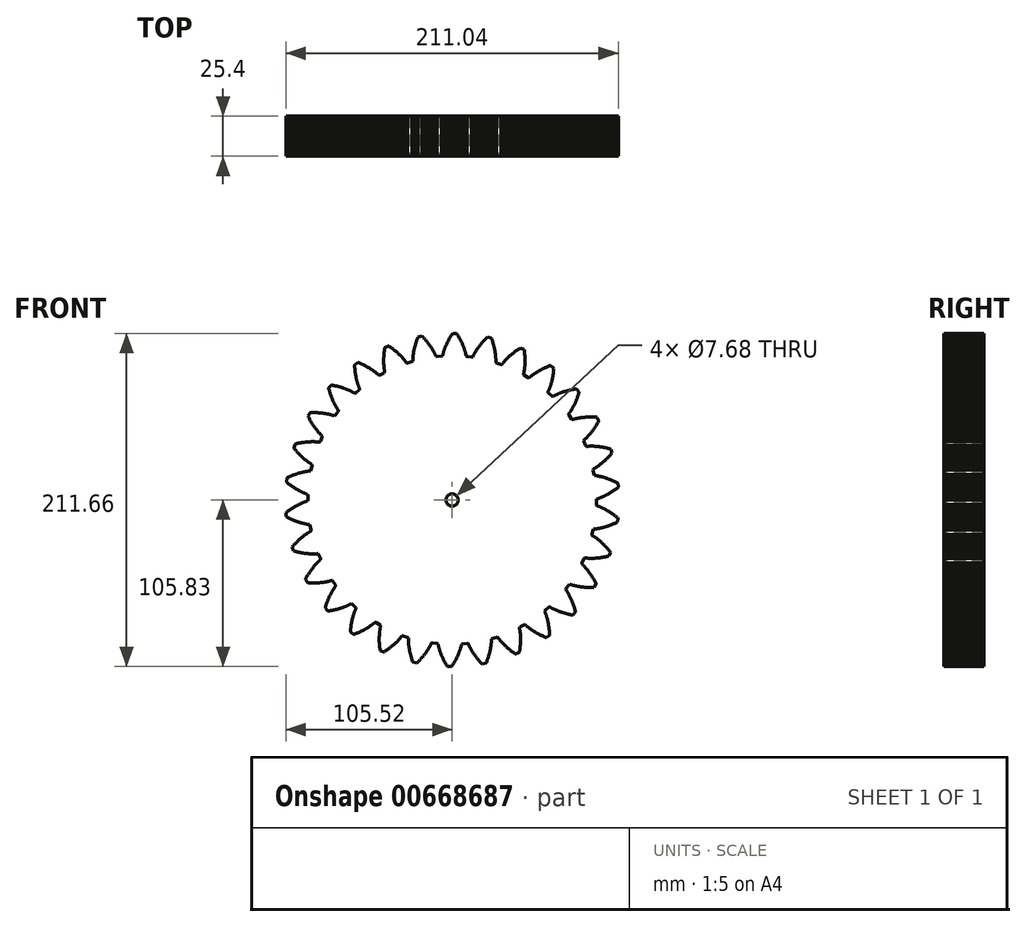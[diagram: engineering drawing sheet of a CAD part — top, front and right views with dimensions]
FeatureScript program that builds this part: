
annotation { "Feature Type Name" : "Feature", "Feature Type Description" : "" }
export const myFeature = defineFeature(function(context is Context, id is Id, definition is map)
    precondition{}
    {
        {
            var Q0;
            Q0=qCreatedBy(makeId("Front.planeOp"),FACE);
            var sketch = newSketch(context, id + "F0", { "sketchPlane" : qUnion([Q0])});
            skLineSegment(sketch, "E0", {"start": v(91.61, 0) * mm, "end": v(91.78, 0.64) * mm});
            skLineSegment(sketch, "E1", {"start": v(91.78, 0.64) * mm, "end": v(92.07, 0.72) * mm});
            skLineSegment(sketch, "E2", {"start": v(92.07, 0.72) * mm, "end": v(92.36, 0.8) * mm});
            skLineSegment(sketch, "E3", {"start": v(92.36, 0.8) * mm, "end": v(92.66, 0.9) * mm});
            skLineSegment(sketch, "E4", {"start": v(92.66, 0.9) * mm, "end": v(92.97, 1) * mm});
            skLineSegment(sketch, "E5", {"start": v(92.97, 1) * mm, "end": v(93.3, 1.12) * mm});
            skLineSegment(sketch, "E6", {"start": v(93.3, 1.12) * mm, "end": v(93.63, 1.24) * mm});
            skLineSegment(sketch, "E7", {"start": v(93.63, 1.24) * mm, "end": v(93.97, 1.37) * mm});
            skLineSegment(sketch, "E8", {"start": v(93.97, 1.37) * mm, "end": v(94.32, 1.5) * mm});
            skLineSegment(sketch, "E9", {"start": v(94.32, 1.5) * mm, "end": v(94.68, 1.64) * mm});
            skLineSegment(sketch, "E10", {"start": v(94.68, 1.64) * mm, "end": v(95.05, 1.8) * mm});
            skLineSegment(sketch, "E11", {"start": v(95.05, 1.8) * mm, "end": v(95.43, 1.96) * mm});
            skLineSegment(sketch, "E12", {"start": v(95.43, 1.96) * mm, "end": v(95.82, 2.13) * mm});
            skLineSegment(sketch, "E13", {"start": v(95.82, 2.13) * mm, "end": v(96.22, 2.3) * mm});
            skLineSegment(sketch, "E14", {"start": v(96.22, 2.3) * mm, "end": v(96.63, 2.5) * mm});
            skLineSegment(sketch, "E15", {"start": v(96.63, 2.5) * mm, "end": v(97.04, 2.7) * mm});
            skLineSegment(sketch, "E16", {"start": v(97.04, 2.7) * mm, "end": v(97.47, 2.9) * mm});
            skLineSegment(sketch, "E17", {"start": v(97.47, 2.9) * mm, "end": v(97.9, 3.13) * mm});
            skLineSegment(sketch, "E18", {"start": v(97.9, 3.13) * mm, "end": v(98.34, 3.36) * mm});
            skLineSegment(sketch, "E19", {"start": v(98.34, 3.36) * mm, "end": v(98.79, 3.6) * mm});
            skLineSegment(sketch, "E20", {"start": v(98.79, 3.6) * mm, "end": v(99.24, 3.85) * mm});
            skLineSegment(sketch, "E21", {"start": v(99.24, 3.85) * mm, "end": v(99.7, 4.11) * mm});
            skLineSegment(sketch, "E22", {"start": v(99.7, 4.11) * mm, "end": v(100.18, 4.4) * mm});
            skLineSegment(sketch, "E23", {"start": v(100.18, 4.4) * mm, "end": v(100.65, 4.68) * mm});
            skLineSegment(sketch, "E24", {"start": v(100.65, 4.68) * mm, "end": v(101.14, 4.97) * mm});
            skLineSegment(sketch, "E25", {"start": v(101.14, 4.97) * mm, "end": v(101.63, 5.29) * mm});
            skLineSegment(sketch, "E26", {"start": v(101.63, 5.29) * mm, "end": v(102.12, 5.6) * mm});
            skLineSegment(sketch, "E27", {"start": v(102.12, 5.6) * mm, "end": v(102.63, 5.94) * mm});
            skLineSegment(sketch, "E28", {"start": v(102.63, 5.94) * mm, "end": v(103.14, 6.3) * mm});
            skLineSegment(sketch, "E29", {"start": v(103.14, 6.3) * mm, "end": v(103.65, 6.65) * mm});
            skLineSegment(sketch, "E30", {"start": v(103.65, 6.65) * mm, "end": v(104.17, 7.03) * mm});
            skLineSegment(sketch, "E31", {"start": v(104.17, 7.03) * mm, "end": v(104.7, 7.41) * mm});
            skLineSegment(sketch, "E32", {"start": v(104.7, 7.41) * mm, "end": v(105.23, 7.81) * mm});
            skLineSegment(sketch, "E33", {"start": v(105.23, 7.81) * mm, "end": v(105.52, 8.2) * mm});
            skLineSegment(sketch, "E34", {"start": v(105.52, 8.2) * mm, "end": v(105.3, 10.56) * mm});
            skLineSegment(sketch, "E35", {"start": v(105.3, 10.56) * mm, "end": v(104.95, 10.9) * mm});
            skLineSegment(sketch, "E36", {"start": v(104.95, 10.9) * mm, "end": v(104.36, 11.2) * mm});
            skLineSegment(sketch, "E37", {"start": v(104.36, 11.2) * mm, "end": v(103.77, 11.48) * mm});
            skLineSegment(sketch, "E38", {"start": v(103.77, 11.48) * mm, "end": v(103.2, 11.76) * mm});
            skLineSegment(sketch, "E39", {"start": v(103.2, 11.76) * mm, "end": v(102.63, 12.02) * mm});
            skLineSegment(sketch, "E40", {"start": v(102.63, 12.02) * mm, "end": v(102.06, 12.28) * mm});
            skLineSegment(sketch, "E41", {"start": v(102.06, 12.28) * mm, "end": v(101.5, 12.52) * mm});
            skLineSegment(sketch, "E42", {"start": v(101.5, 12.52) * mm, "end": v(100.96, 12.75) * mm});
            skLineSegment(sketch, "E43", {"start": v(100.96, 12.75) * mm, "end": v(100.42, 12.97) * mm});
            skLineSegment(sketch, "E44", {"start": v(100.42, 12.97) * mm, "end": v(99.9, 13.17) * mm});
            skLineSegment(sketch, "E45", {"start": v(99.9, 13.17) * mm, "end": v(99.38, 13.37) * mm});
            skLineSegment(sketch, "E46", {"start": v(99.38, 13.37) * mm, "end": v(98.86, 13.56) * mm});
            skLineSegment(sketch, "E47", {"start": v(98.86, 13.56) * mm, "end": v(98.36, 13.74) * mm});
            skLineSegment(sketch, "E48", {"start": v(98.36, 13.74) * mm, "end": v(97.87, 13.9) * mm});
            skLineSegment(sketch, "E49", {"start": v(97.87, 13.9) * mm, "end": v(97.39, 14.06) * mm});
            skLineSegment(sketch, "E50", {"start": v(97.39, 14.06) * mm, "end": v(96.91, 14.21) * mm});
            skLineSegment(sketch, "E51", {"start": v(96.91, 14.21) * mm, "end": v(96.45, 14.35) * mm});
            skLineSegment(sketch, "E52", {"start": v(96.45, 14.35) * mm, "end": v(96, 14.49) * mm});
            skLineSegment(sketch, "E53", {"start": v(96, 14.49) * mm, "end": v(95.55, 14.6) * mm});
            skLineSegment(sketch, "E54", {"start": v(95.55, 14.6) * mm, "end": v(95.12, 14.72) * mm});
            skLineSegment(sketch, "E55", {"start": v(95.12, 14.72) * mm, "end": v(94.7, 14.83) * mm});
            skLineSegment(sketch, "E56", {"start": v(94.7, 14.83) * mm, "end": v(94.28, 14.93) * mm});
            skLineSegment(sketch, "E57", {"start": v(94.28, 14.93) * mm, "end": v(93.88, 15.02) * mm});
            skLineSegment(sketch, "E58", {"start": v(93.88, 15.02) * mm, "end": v(93.48, 15.1) * mm});
            skLineSegment(sketch, "E59", {"start": v(93.48, 15.1) * mm, "end": v(93.1, 15.18) * mm});
            skLineSegment(sketch, "E60", {"start": v(93.1, 15.18) * mm, "end": v(92.73, 15.25) * mm});
            skLineSegment(sketch, "E61", {"start": v(92.73, 15.25) * mm, "end": v(92.37, 15.32) * mm});
            skLineSegment(sketch, "E62", {"start": v(92.37, 15.32) * mm, "end": v(92.03, 15.38) * mm});
            skLineSegment(sketch, "E63", {"start": v(92.03, 15.38) * mm, "end": v(91.69, 15.43) * mm});
            skLineSegment(sketch, "E64", {"start": v(91.69, 15.43) * mm, "end": v(91.36, 15.48) * mm});
            skLineSegment(sketch, "E65", {"start": v(91.36, 15.48) * mm, "end": v(91.05, 15.52) * mm});
            skLineSegment(sketch, "E66", {"start": v(91.05, 15.52) * mm, "end": v(90.75, 15.55) * mm});
            skLineSegment(sketch, "E67", {"start": v(90.75, 15.55) * mm, "end": v(90.45, 15.58) * mm});
            skLineSegment(sketch, "E68", {"start": v(90.45, 15.58) * mm, "end": v(90.17, 16.18) * mm});
            skLineSegment(sketch, "E69", {"start": v(90.17, 16.18) * mm, "end": v(89.6, 19.05) * mm});
            skLineSegment(sketch, "E70", {"start": v(89.6, 19.05) * mm, "end": v(89.65, 19.7) * mm});
            skLineSegment(sketch, "E71", {"start": v(89.65, 19.7) * mm, "end": v(89.9, 19.85) * mm});
            skLineSegment(sketch, "E72", {"start": v(89.9, 19.85) * mm, "end": v(90.17, 20) * mm});
            skLineSegment(sketch, "E73", {"start": v(90.17, 20) * mm, "end": v(90.45, 20.15) * mm});
            skLineSegment(sketch, "E74", {"start": v(90.45, 20.15) * mm, "end": v(90.73, 20.32) * mm});
            skLineSegment(sketch, "E75", {"start": v(90.73, 20.32) * mm, "end": v(91.02, 20.5) * mm});
            skLineSegment(sketch, "E76", {"start": v(91.02, 20.5) * mm, "end": v(91.32, 20.68) * mm});
            skLineSegment(sketch, "E77", {"start": v(91.32, 20.68) * mm, "end": v(91.63, 20.87) * mm});
            skLineSegment(sketch, "E78", {"start": v(91.63, 20.87) * mm, "end": v(91.95, 21.08) * mm});
            skLineSegment(sketch, "E79", {"start": v(91.95, 21.08) * mm, "end": v(92.27, 21.3) * mm});
            skLineSegment(sketch, "E80", {"start": v(92.27, 21.3) * mm, "end": v(92.6, 21.52) * mm});
            skLineSegment(sketch, "E81", {"start": v(92.6, 21.52) * mm, "end": v(92.94, 21.76) * mm});
            skLineSegment(sketch, "E82", {"start": v(92.94, 21.76) * mm, "end": v(93.29, 22) * mm});
            skLineSegment(sketch, "E83", {"start": v(93.29, 22) * mm, "end": v(93.64, 22.26) * mm});
            skLineSegment(sketch, "E84", {"start": v(93.64, 22.26) * mm, "end": v(94, 22.53) * mm});
            skLineSegment(sketch, "E85", {"start": v(94, 22.53) * mm, "end": v(94.36, 22.81) * mm});
            skLineSegment(sketch, "E86", {"start": v(94.36, 22.81) * mm, "end": v(94.73, 23.1) * mm});
            skLineSegment(sketch, "E87", {"start": v(94.73, 23.1) * mm, "end": v(95.1, 23.41) * mm});
            skLineSegment(sketch, "E88", {"start": v(95.1, 23.41) * mm, "end": v(95.5, 23.73) * mm});
            skLineSegment(sketch, "E89", {"start": v(95.5, 23.73) * mm, "end": v(95.88, 24.06) * mm});
            skLineSegment(sketch, "E90", {"start": v(95.88, 24.06) * mm, "end": v(96.27, 24.4) * mm});
            skLineSegment(sketch, "E91", {"start": v(96.27, 24.4) * mm, "end": v(96.67, 24.76) * mm});
            skLineSegment(sketch, "E92", {"start": v(96.67, 24.76) * mm, "end": v(97.07, 25.12) * mm});
            skLineSegment(sketch, "E93", {"start": v(97.07, 25.12) * mm, "end": v(97.48, 25.5) * mm});
            skLineSegment(sketch, "E94", {"start": v(97.48, 25.5) * mm, "end": v(97.9, 25.9) * mm});
            skLineSegment(sketch, "E95", {"start": v(97.9, 25.9) * mm, "end": v(98.3, 26.3) * mm});
            skLineSegment(sketch, "E96", {"start": v(98.3, 26.3) * mm, "end": v(98.73, 26.72) * mm});
            skLineSegment(sketch, "E97", {"start": v(98.73, 26.72) * mm, "end": v(99.15, 27.15) * mm});
            skLineSegment(sketch, "E98", {"start": v(99.15, 27.15) * mm, "end": v(99.57, 27.6) * mm});
            skLineSegment(sketch, "E99", {"start": v(99.57, 27.6) * mm, "end": v(100, 28.06) * mm});
            skLineSegment(sketch, "E100", {"start": v(100, 28.06) * mm, "end": v(100.43, 28.53) * mm});
            skLineSegment(sketch, "E101", {"start": v(100.43, 28.53) * mm, "end": v(100.87, 29.02) * mm});
            skLineSegment(sketch, "E102", {"start": v(100.87, 29.02) * mm, "end": v(101.3, 29.52) * mm});
            skLineSegment(sketch, "E103", {"start": v(101.3, 29.52) * mm, "end": v(101.5, 29.96) * mm});
            skLineSegment(sketch, "E104", {"start": v(101.5, 29.96) * mm, "end": v(100.8, 32.22) * mm});
            skLineSegment(sketch, "E105", {"start": v(100.8, 32.22) * mm, "end": v(100.4, 32.48) * mm});
            skLineSegment(sketch, "E106", {"start": v(100.4, 32.48) * mm, "end": v(99.75, 32.65) * mm});
            skLineSegment(sketch, "E107", {"start": v(99.75, 32.65) * mm, "end": v(99.12, 32.8) * mm});
            skLineSegment(sketch, "E108", {"start": v(99.12, 32.8) * mm, "end": v(98.5, 32.96) * mm});
            skLineSegment(sketch, "E109", {"start": v(98.5, 32.96) * mm, "end": v(97.88, 33.1) * mm});
            skLineSegment(sketch, "E110", {"start": v(97.88, 33.1) * mm, "end": v(97.28, 33.23) * mm});
            skLineSegment(sketch, "E111", {"start": v(97.28, 33.23) * mm, "end": v(96.69, 33.35) * mm});
            skLineSegment(sketch, "E112", {"start": v(96.69, 33.35) * mm, "end": v(96.1, 33.46) * mm});
            skLineSegment(sketch, "E113", {"start": v(96.1, 33.46) * mm, "end": v(95.53, 33.56) * mm});
            skLineSegment(sketch, "E114", {"start": v(95.53, 33.56) * mm, "end": v(94.97, 33.66) * mm});
            skLineSegment(sketch, "E115", {"start": v(94.97, 33.66) * mm, "end": v(94.42, 33.74) * mm});
            skLineSegment(sketch, "E116", {"start": v(94.42, 33.74) * mm, "end": v(93.88, 33.82) * mm});
            skLineSegment(sketch, "E117", {"start": v(93.88, 33.82) * mm, "end": v(93.36, 33.89) * mm});
            skLineSegment(sketch, "E118", {"start": v(93.36, 33.89) * mm, "end": v(92.84, 33.95) * mm});
            skLineSegment(sketch, "E119", {"start": v(92.84, 33.95) * mm, "end": v(92.33, 34) * mm});
            skLineSegment(sketch, "E120", {"start": v(92.33, 34) * mm, "end": v(91.84, 34.05) * mm});
            skLineSegment(sketch, "E121", {"start": v(91.84, 34.05) * mm, "end": v(91.36, 34.1) * mm});
            skLineSegment(sketch, "E122", {"start": v(91.36, 34.1) * mm, "end": v(90.88, 34.13) * mm});
            skLineSegment(sketch, "E123", {"start": v(90.88, 34.13) * mm, "end": v(90.43, 34.15) * mm});
            skLineSegment(sketch, "E124", {"start": v(90.43, 34.15) * mm, "end": v(89.98, 34.18) * mm});
            skLineSegment(sketch, "E125", {"start": v(89.98, 34.18) * mm, "end": v(89.54, 34.2) * mm});
            skLineSegment(sketch, "E126", {"start": v(89.54, 34.2) * mm, "end": v(89.11, 34.2) * mm});
            skLineSegment(sketch, "E127", {"start": v(89.11, 34.2) * mm, "end": v(88.7, 34.21) * mm});
            skLineSegment(sketch, "E128", {"start": v(88.7, 34.21) * mm, "end": v(88.3, 34.21) * mm});
            skLineSegment(sketch, "E129", {"start": v(88.3, 34.21) * mm, "end": v(87.91, 34.2) * mm});
            skLineSegment(sketch, "E130", {"start": v(87.91, 34.2) * mm, "end": v(87.54, 34.2) * mm});
            skLineSegment(sketch, "E131", {"start": v(87.54, 34.2) * mm, "end": v(87.17, 34.19) * mm});
            skLineSegment(sketch, "E132", {"start": v(87.17, 34.19) * mm, "end": v(86.82, 34.17) * mm});
            skLineSegment(sketch, "E133", {"start": v(86.82, 34.17) * mm, "end": v(86.48, 34.15) * mm});
            skLineSegment(sketch, "E134", {"start": v(86.48, 34.15) * mm, "end": v(86.15, 34.13) * mm});
            skLineSegment(sketch, "E135", {"start": v(86.15, 34.13) * mm, "end": v(85.83, 34.1) * mm});
            skLineSegment(sketch, "E136", {"start": v(85.83, 34.1) * mm, "end": v(85.53, 34.08) * mm});
            skLineSegment(sketch, "E137", {"start": v(85.53, 34.08) * mm, "end": v(85.24, 34.05) * mm});
            skLineSegment(sketch, "E138", {"start": v(85.24, 34.05) * mm, "end": v(84.84, 34.58) * mm});
            skLineSegment(sketch, "E139", {"start": v(84.84, 34.58) * mm, "end": v(83.7, 37.26) * mm});
            skLineSegment(sketch, "E140", {"start": v(83.7, 37.26) * mm, "end": v(83.6, 37.91) * mm});
            skLineSegment(sketch, "E141", {"start": v(83.6, 37.91) * mm, "end": v(83.81, 38.1) * mm});
            skLineSegment(sketch, "E142", {"start": v(83.81, 38.1) * mm, "end": v(84.04, 38.3) * mm});
            skLineSegment(sketch, "E143", {"start": v(84.04, 38.3) * mm, "end": v(84.28, 38.51) * mm});
            skLineSegment(sketch, "E144", {"start": v(84.28, 38.51) * mm, "end": v(84.52, 38.74) * mm});
            skLineSegment(sketch, "E145", {"start": v(84.52, 38.74) * mm, "end": v(84.77, 38.97) * mm});
            skLineSegment(sketch, "E146", {"start": v(84.77, 38.97) * mm, "end": v(85.03, 39.21) * mm});
            skLineSegment(sketch, "E147", {"start": v(85.03, 39.21) * mm, "end": v(85.3, 39.47) * mm});
            skLineSegment(sketch, "E148", {"start": v(85.3, 39.47) * mm, "end": v(85.56, 39.73) * mm});
            skLineSegment(sketch, "E149", {"start": v(85.56, 39.73) * mm, "end": v(85.83, 40.01) * mm});
            skLineSegment(sketch, "E150", {"start": v(85.83, 40.01) * mm, "end": v(86.1, 40.3) * mm});
            skLineSegment(sketch, "E151", {"start": v(86.1, 40.3) * mm, "end": v(86.39, 40.6) * mm});
            skLineSegment(sketch, "E152", {"start": v(86.39, 40.6) * mm, "end": v(86.67, 40.92) * mm});
            skLineSegment(sketch, "E153", {"start": v(86.67, 40.92) * mm, "end": v(86.96, 41.24) * mm});
            skLineSegment(sketch, "E154", {"start": v(86.96, 41.24) * mm, "end": v(87.26, 41.58) * mm});
            skLineSegment(sketch, "E155", {"start": v(87.26, 41.58) * mm, "end": v(87.56, 41.93) * mm});
            skLineSegment(sketch, "E156", {"start": v(87.56, 41.93) * mm, "end": v(87.86, 42.3) * mm});
            skLineSegment(sketch, "E157", {"start": v(87.86, 42.3) * mm, "end": v(88.16, 42.68) * mm});
            skLineSegment(sketch, "E158", {"start": v(88.16, 42.68) * mm, "end": v(88.47, 43.07) * mm});
            skLineSegment(sketch, "E159", {"start": v(88.47, 43.07) * mm, "end": v(88.78, 43.47) * mm});
            skLineSegment(sketch, "E160", {"start": v(88.78, 43.47) * mm, "end": v(89.1, 43.88) * mm});
            skLineSegment(sketch, "E161", {"start": v(89.1, 43.88) * mm, "end": v(89.41, 44.31) * mm});
            skLineSegment(sketch, "E162", {"start": v(89.41, 44.31) * mm, "end": v(89.73, 44.76) * mm});
            skLineSegment(sketch, "E163", {"start": v(89.73, 44.76) * mm, "end": v(90.05, 45.21) * mm});
            skLineSegment(sketch, "E164", {"start": v(90.05, 45.21) * mm, "end": v(90.37, 45.68) * mm});
            skLineSegment(sketch, "E165", {"start": v(90.37, 45.68) * mm, "end": v(90.69, 46.16) * mm});
            skLineSegment(sketch, "E166", {"start": v(90.69, 46.16) * mm, "end": v(91.01, 46.66) * mm});
            skLineSegment(sketch, "E167", {"start": v(91.01, 46.66) * mm, "end": v(91.34, 47.17) * mm});
            skLineSegment(sketch, "E168", {"start": v(91.34, 47.17) * mm, "end": v(91.66, 47.7) * mm});
            skLineSegment(sketch, "E169", {"start": v(91.66, 47.7) * mm, "end": v(91.98, 48.24) * mm});
            skLineSegment(sketch, "E170", {"start": v(91.98, 48.24) * mm, "end": v(92.3, 48.79) * mm});
            skLineSegment(sketch, "E171", {"start": v(92.3, 48.79) * mm, "end": v(92.63, 49.35) * mm});
            skLineSegment(sketch, "E172", {"start": v(92.63, 49.35) * mm, "end": v(92.95, 49.93) * mm});
            skLineSegment(sketch, "E173", {"start": v(92.95, 49.93) * mm, "end": v(93.05, 50.41) * mm});
            skLineSegment(sketch, "E174", {"start": v(93.05, 50.41) * mm, "end": v(91.9, 52.48) * mm});
            skLineSegment(sketch, "E175", {"start": v(91.9, 52.48) * mm, "end": v(91.45, 52.64) * mm});
            skLineSegment(sketch, "E176", {"start": v(91.45, 52.64) * mm, "end": v(90.78, 52.68) * mm});
            skLineSegment(sketch, "E177", {"start": v(90.78, 52.68) * mm, "end": v(90.13, 52.7) * mm});
            skLineSegment(sketch, "E178", {"start": v(90.13, 52.7) * mm, "end": v(89.49, 52.72) * mm});
            skLineSegment(sketch, "E179", {"start": v(89.49, 52.72) * mm, "end": v(88.86, 52.73) * mm});
            skLineSegment(sketch, "E180", {"start": v(88.86, 52.73) * mm, "end": v(88.25, 52.73) * mm});
            skLineSegment(sketch, "E181", {"start": v(88.25, 52.73) * mm, "end": v(87.64, 52.72) * mm});
            skLineSegment(sketch, "E182", {"start": v(87.64, 52.72) * mm, "end": v(87.05, 52.7) * mm});
            skLineSegment(sketch, "E183", {"start": v(87.05, 52.7) * mm, "end": v(86.47, 52.7) * mm});
            skLineSegment(sketch, "E184", {"start": v(86.47, 52.7) * mm, "end": v(85.9, 52.67) * mm});
            skLineSegment(sketch, "E185", {"start": v(85.9, 52.67) * mm, "end": v(85.34, 52.64) * mm});
            skLineSegment(sketch, "E186", {"start": v(85.34, 52.64) * mm, "end": v(84.8, 52.6) * mm});
            skLineSegment(sketch, "E187", {"start": v(84.8, 52.6) * mm, "end": v(84.27, 52.56) * mm});
            skLineSegment(sketch, "E188", {"start": v(84.27, 52.56) * mm, "end": v(83.75, 52.51) * mm});
            skLineSegment(sketch, "E189", {"start": v(83.75, 52.51) * mm, "end": v(83.25, 52.46) * mm});
            skLineSegment(sketch, "E190", {"start": v(83.25, 52.46) * mm, "end": v(82.75, 52.4) * mm});
            skLineSegment(sketch, "E191", {"start": v(82.75, 52.4) * mm, "end": v(82.27, 52.34) * mm});
            skLineSegment(sketch, "E192", {"start": v(82.27, 52.34) * mm, "end": v(81.8, 52.28) * mm});
            skLineSegment(sketch, "E193", {"start": v(81.8, 52.28) * mm, "end": v(81.35, 52.2) * mm});
            skLineSegment(sketch, "E194", {"start": v(81.35, 52.2) * mm, "end": v(80.9, 52.14) * mm});
            skLineSegment(sketch, "E195", {"start": v(80.9, 52.14) * mm, "end": v(80.47, 52.06) * mm});
            skLineSegment(sketch, "E196", {"start": v(80.47, 52.06) * mm, "end": v(80.06, 51.98) * mm});
            skLineSegment(sketch, "E197", {"start": v(80.06, 51.98) * mm, "end": v(79.65, 51.9) * mm});
            skLineSegment(sketch, "E198", {"start": v(79.65, 51.9) * mm, "end": v(79.26, 51.82) * mm});
            skLineSegment(sketch, "E199", {"start": v(79.26, 51.82) * mm, "end": v(78.88, 51.74) * mm});
            skLineSegment(sketch, "E200", {"start": v(78.88, 51.74) * mm, "end": v(78.51, 51.65) * mm});
            skLineSegment(sketch, "E201", {"start": v(78.51, 51.65) * mm, "end": v(78.16, 51.57) * mm});
            skLineSegment(sketch, "E202", {"start": v(78.16, 51.57) * mm, "end": v(77.82, 51.48) * mm});
            skLineSegment(sketch, "E203", {"start": v(77.82, 51.48) * mm, "end": v(77.49, 51.39) * mm});
            skLineSegment(sketch, "E204", {"start": v(77.49, 51.39) * mm, "end": v(77.17, 51.3) * mm});
            skLineSegment(sketch, "E205", {"start": v(77.17, 51.3) * mm, "end": v(76.87, 51.2) * mm});
            skLineSegment(sketch, "E206", {"start": v(76.87, 51.2) * mm, "end": v(76.57, 51.12) * mm});
            skLineSegment(sketch, "E207", {"start": v(76.57, 51.12) * mm, "end": v(76.3, 51.03) * mm});
            skLineSegment(sketch, "E208", {"start": v(76.3, 51.03) * mm, "end": v(75.8, 51.46) * mm});
            skLineSegment(sketch, "E209", {"start": v(75.8, 51.46) * mm, "end": v(74.11, 53.85) * mm});
            skLineSegment(sketch, "E210", {"start": v(74.11, 53.85) * mm, "end": v(73.88, 54.46) * mm});
            skLineSegment(sketch, "E211", {"start": v(73.88, 54.46) * mm, "end": v(74.06, 54.7) * mm});
            skLineSegment(sketch, "E212", {"start": v(74.06, 54.7) * mm, "end": v(74.24, 54.94) * mm});
            skLineSegment(sketch, "E213", {"start": v(74.24, 54.94) * mm, "end": v(74.43, 55.2) * mm});
            skLineSegment(sketch, "E214", {"start": v(74.43, 55.2) * mm, "end": v(74.62, 55.46) * mm});
            skLineSegment(sketch, "E215", {"start": v(74.62, 55.46) * mm, "end": v(74.82, 55.74) * mm});
            skLineSegment(sketch, "E216", {"start": v(74.82, 55.74) * mm, "end": v(75.02, 56.04) * mm});
            skLineSegment(sketch, "E217", {"start": v(75.02, 56.04) * mm, "end": v(75.22, 56.34) * mm});
            skLineSegment(sketch, "E218", {"start": v(75.22, 56.34) * mm, "end": v(75.43, 56.65) * mm});
            skLineSegment(sketch, "E219", {"start": v(75.43, 56.65) * mm, "end": v(75.63, 56.98) * mm});
            skLineSegment(sketch, "E220", {"start": v(75.63, 56.98) * mm, "end": v(75.84, 57.33) * mm});
            skLineSegment(sketch, "E221", {"start": v(75.84, 57.33) * mm, "end": v(76.06, 57.68) * mm});
            skLineSegment(sketch, "E222", {"start": v(76.06, 57.68) * mm, "end": v(76.27, 58.05) * mm});
            skLineSegment(sketch, "E223", {"start": v(76.27, 58.05) * mm, "end": v(76.49, 58.42) * mm});
            skLineSegment(sketch, "E224", {"start": v(76.49, 58.42) * mm, "end": v(76.7, 58.82) * mm});
            skLineSegment(sketch, "E225", {"start": v(76.7, 58.82) * mm, "end": v(76.92, 59.22) * mm});
            skLineSegment(sketch, "E226", {"start": v(76.92, 59.22) * mm, "end": v(77.14, 59.64) * mm});
            skLineSegment(sketch, "E227", {"start": v(77.14, 59.64) * mm, "end": v(77.36, 60.07) * mm});
            skLineSegment(sketch, "E228", {"start": v(77.36, 60.07) * mm, "end": v(77.58, 60.52) * mm});
            skLineSegment(sketch, "E229", {"start": v(77.58, 60.52) * mm, "end": v(77.8, 60.98) * mm});
            skLineSegment(sketch, "E230", {"start": v(77.8, 60.98) * mm, "end": v(78.02, 61.45) * mm});
            skLineSegment(sketch, "E231", {"start": v(78.02, 61.45) * mm, "end": v(78.24, 61.93) * mm});
            skLineSegment(sketch, "E232", {"start": v(78.24, 61.93) * mm, "end": v(78.46, 62.43) * mm});
            skLineSegment(sketch, "E233", {"start": v(78.46, 62.43) * mm, "end": v(78.68, 62.95) * mm});
            skLineSegment(sketch, "E234", {"start": v(78.68, 62.95) * mm, "end": v(78.9, 63.47) * mm});
            skLineSegment(sketch, "E235", {"start": v(78.9, 63.47) * mm, "end": v(79.11, 64.01) * mm});
            skLineSegment(sketch, "E236", {"start": v(79.11, 64.01) * mm, "end": v(79.32, 64.56) * mm});
            skLineSegment(sketch, "E237", {"start": v(79.32, 64.56) * mm, "end": v(79.53, 65.13) * mm});
            skLineSegment(sketch, "E238", {"start": v(79.53, 65.13) * mm, "end": v(79.74, 65.71) * mm});
            skLineSegment(sketch, "E239", {"start": v(79.74, 65.71) * mm, "end": v(79.94, 66.3) * mm});
            skLineSegment(sketch, "E240", {"start": v(79.94, 66.3) * mm, "end": v(80.15, 66.91) * mm});
            skLineSegment(sketch, "E241", {"start": v(80.15, 66.91) * mm, "end": v(80.34, 67.54) * mm});
            skLineSegment(sketch, "E242", {"start": v(80.34, 67.54) * mm, "end": v(80.54, 68.17) * mm});
            skLineSegment(sketch, "E243", {"start": v(80.54, 68.17) * mm, "end": v(80.54, 68.66) * mm});
            skLineSegment(sketch, "E244", {"start": v(80.54, 68.66) * mm, "end": v(78.99, 70.44) * mm});
            skLineSegment(sketch, "E245", {"start": v(78.99, 70.44) * mm, "end": v(78.5, 70.5) * mm});
            skLineSegment(sketch, "E246", {"start": v(78.5, 70.5) * mm, "end": v(77.85, 70.4) * mm});
            skLineSegment(sketch, "E247", {"start": v(77.85, 70.4) * mm, "end": v(77.2, 70.29) * mm});
            skLineSegment(sketch, "E248", {"start": v(77.2, 70.29) * mm, "end": v(76.57, 70.17) * mm});
            skLineSegment(sketch, "E249", {"start": v(76.57, 70.17) * mm, "end": v(75.96, 70.05) * mm});
            skLineSegment(sketch, "E250", {"start": v(75.96, 70.05) * mm, "end": v(75.35, 69.92) * mm});
            skLineSegment(sketch, "E251", {"start": v(75.35, 69.92) * mm, "end": v(74.76, 69.8) * mm});
            skLineSegment(sketch, "E252", {"start": v(74.76, 69.8) * mm, "end": v(74.19, 69.66) * mm});
            skLineSegment(sketch, "E253", {"start": v(74.19, 69.66) * mm, "end": v(73.62, 69.52) * mm});
            skLineSegment(sketch, "E254", {"start": v(73.62, 69.52) * mm, "end": v(73.07, 69.37) * mm});
            skLineSegment(sketch, "E255", {"start": v(73.07, 69.37) * mm, "end": v(72.54, 69.23) * mm});
            skLineSegment(sketch, "E256", {"start": v(72.54, 69.23) * mm, "end": v(72.01, 69.08) * mm});
            skLineSegment(sketch, "E257", {"start": v(72.01, 69.08) * mm, "end": v(71.5, 68.93) * mm});
            skLineSegment(sketch, "E258", {"start": v(71.5, 68.93) * mm, "end": v(71, 68.78) * mm});
            skLineSegment(sketch, "E259", {"start": v(71, 68.78) * mm, "end": v(70.52, 68.62) * mm});
            skLineSegment(sketch, "E260", {"start": v(70.52, 68.62) * mm, "end": v(70.05, 68.46) * mm});
            skLineSegment(sketch, "E261", {"start": v(70.05, 68.46) * mm, "end": v(69.6, 68.3) * mm});
            skLineSegment(sketch, "E262", {"start": v(69.6, 68.3) * mm, "end": v(69.15, 68.14) * mm});
            skLineSegment(sketch, "E263", {"start": v(69.15, 68.14) * mm, "end": v(68.71, 67.98) * mm});
            skLineSegment(sketch, "E264", {"start": v(68.71, 67.98) * mm, "end": v(68.3, 67.82) * mm});
            skLineSegment(sketch, "E265", {"start": v(68.3, 67.82) * mm, "end": v(67.9, 67.66) * mm});
            skLineSegment(sketch, "E266", {"start": v(67.9, 67.66) * mm, "end": v(67.5, 67.5) * mm});
            skLineSegment(sketch, "E267", {"start": v(67.5, 67.5) * mm, "end": v(67.12, 67.33) * mm});
            skLineSegment(sketch, "E268", {"start": v(67.12, 67.33) * mm, "end": v(66.75, 67.17) * mm});
            skLineSegment(sketch, "E269", {"start": v(66.75, 67.17) * mm, "end": v(66.4, 67) * mm});
            skLineSegment(sketch, "E270", {"start": v(66.4, 67) * mm, "end": v(66.06, 66.85) * mm});
            skLineSegment(sketch, "E271", {"start": v(66.06, 66.85) * mm, "end": v(65.73, 66.69) * mm});
            skLineSegment(sketch, "E272", {"start": v(65.73, 66.69) * mm, "end": v(65.41, 66.53) * mm});
            skLineSegment(sketch, "E273", {"start": v(65.41, 66.53) * mm, "end": v(65.1, 66.38) * mm});
            skLineSegment(sketch, "E274", {"start": v(65.1, 66.38) * mm, "end": v(64.82, 66.22) * mm});
            skLineSegment(sketch, "E275", {"start": v(64.82, 66.22) * mm, "end": v(64.54, 66.07) * mm});
            skLineSegment(sketch, "E276", {"start": v(64.54, 66.07) * mm, "end": v(64.27, 65.92) * mm});
            skLineSegment(sketch, "E277", {"start": v(64.27, 65.92) * mm, "end": v(64.02, 65.78) * mm});
            skLineSegment(sketch, "E278", {"start": v(64.02, 65.78) * mm, "end": v(63.44, 66.1) * mm});
            skLineSegment(sketch, "E279", {"start": v(63.44, 66.1) * mm, "end": v(61.3, 68.08) * mm});
            skLineSegment(sketch, "E280", {"start": v(61.3, 68.08) * mm, "end": v(60.94, 68.64) * mm});
            skLineSegment(sketch, "E281", {"start": v(60.94, 68.64) * mm, "end": v(61.07, 68.9) * mm});
            skLineSegment(sketch, "E282", {"start": v(61.07, 68.9) * mm, "end": v(61.2, 69.18) * mm});
            skLineSegment(sketch, "E283", {"start": v(61.2, 69.18) * mm, "end": v(61.33, 69.47) * mm});
            skLineSegment(sketch, "E284", {"start": v(61.33, 69.47) * mm, "end": v(61.46, 69.77) * mm});
            skLineSegment(sketch, "E285", {"start": v(61.46, 69.77) * mm, "end": v(61.6, 70.08) * mm});
            skLineSegment(sketch, "E286", {"start": v(61.6, 70.08) * mm, "end": v(61.73, 70.4) * mm});
            skLineSegment(sketch, "E287", {"start": v(61.73, 70.4) * mm, "end": v(61.86, 70.75) * mm});
            skLineSegment(sketch, "E288", {"start": v(61.86, 70.75) * mm, "end": v(62, 71.1) * mm});
            skLineSegment(sketch, "E289", {"start": v(62, 71.1) * mm, "end": v(62.13, 71.46) * mm});
            skLineSegment(sketch, "E290", {"start": v(62.13, 71.46) * mm, "end": v(62.27, 71.84) * mm});
            skLineSegment(sketch, "E291", {"start": v(62.27, 71.84) * mm, "end": v(62.4, 72.23) * mm});
            skLineSegment(sketch, "E292", {"start": v(62.4, 72.23) * mm, "end": v(62.54, 72.64) * mm});
            skLineSegment(sketch, "E293", {"start": v(62.54, 72.64) * mm, "end": v(62.67, 73.05) * mm});
            skLineSegment(sketch, "E294", {"start": v(62.67, 73.05) * mm, "end": v(62.8, 73.48) * mm});
            skLineSegment(sketch, "E295", {"start": v(62.8, 73.48) * mm, "end": v(62.93, 73.92) * mm});
            skLineSegment(sketch, "E296", {"start": v(62.93, 73.92) * mm, "end": v(63.06, 74.38) * mm});
            skLineSegment(sketch, "E297", {"start": v(63.06, 74.38) * mm, "end": v(63.18, 74.85) * mm});
            skLineSegment(sketch, "E298", {"start": v(63.18, 74.85) * mm, "end": v(63.3, 75.33) * mm});
            skLineSegment(sketch, "E299", {"start": v(63.3, 75.33) * mm, "end": v(63.43, 75.82) * mm});
            skLineSegment(sketch, "E300", {"start": v(63.43, 75.82) * mm, "end": v(63.54, 76.33) * mm});
            skLineSegment(sketch, "E301", {"start": v(63.54, 76.33) * mm, "end": v(63.66, 76.85) * mm});
            skLineSegment(sketch, "E302", {"start": v(63.66, 76.85) * mm, "end": v(63.77, 77.38) * mm});
            skLineSegment(sketch, "E303", {"start": v(63.77, 77.38) * mm, "end": v(63.87, 77.93) * mm});
            skLineSegment(sketch, "E304", {"start": v(63.87, 77.93) * mm, "end": v(63.98, 78.49) * mm});
            skLineSegment(sketch, "E305", {"start": v(63.98, 78.49) * mm, "end": v(64.07, 79.06) * mm});
            skLineSegment(sketch, "E306", {"start": v(64.07, 79.06) * mm, "end": v(64.17, 79.65) * mm});
            skLineSegment(sketch, "E307", {"start": v(64.17, 79.65) * mm, "end": v(64.25, 80.24) * mm});
            skLineSegment(sketch, "E308", {"start": v(64.25, 80.24) * mm, "end": v(64.33, 80.85) * mm});
            skLineSegment(sketch, "E309", {"start": v(64.33, 80.85) * mm, "end": v(64.41, 81.48) * mm});
            skLineSegment(sketch, "E310", {"start": v(64.41, 81.48) * mm, "end": v(64.48, 82.11) * mm});
            skLineSegment(sketch, "E311", {"start": v(64.48, 82.11) * mm, "end": v(64.55, 82.76) * mm});
            skLineSegment(sketch, "E312", {"start": v(64.55, 82.76) * mm, "end": v(64.6, 83.42) * mm});
            skLineSegment(sketch, "E313", {"start": v(64.6, 83.42) * mm, "end": v(64.5, 83.9) * mm});
            skLineSegment(sketch, "E314", {"start": v(64.5, 83.9) * mm, "end": v(62.62, 85.32) * mm});
            skLineSegment(sketch, "E315", {"start": v(62.62, 85.32) * mm, "end": v(62.13, 85.29) * mm});
            skLineSegment(sketch, "E316", {"start": v(62.13, 85.29) * mm, "end": v(61.5, 85.05) * mm});
            skLineSegment(sketch, "E317", {"start": v(61.5, 85.05) * mm, "end": v(60.9, 84.8) * mm});
            skLineSegment(sketch, "E318", {"start": v(60.9, 84.8) * mm, "end": v(60.31, 84.56) * mm});
            skLineSegment(sketch, "E319", {"start": v(60.31, 84.56) * mm, "end": v(59.73, 84.31) * mm});
            skLineSegment(sketch, "E320", {"start": v(59.73, 84.31) * mm, "end": v(59.17, 84.06) * mm});
            skLineSegment(sketch, "E321", {"start": v(59.17, 84.06) * mm, "end": v(58.62, 83.81) * mm});
            skLineSegment(sketch, "E322", {"start": v(58.62, 83.81) * mm, "end": v(58.08, 83.56) * mm});
            skLineSegment(sketch, "E323", {"start": v(58.08, 83.56) * mm, "end": v(57.56, 83.3) * mm});
            skLineSegment(sketch, "E324", {"start": v(57.56, 83.3) * mm, "end": v(57.05, 83.05) * mm});
            skLineSegment(sketch, "E325", {"start": v(57.05, 83.05) * mm, "end": v(56.56, 82.8) * mm});
            skLineSegment(sketch, "E326", {"start": v(56.56, 82.8) * mm, "end": v(56.08, 82.54) * mm});
            skLineSegment(sketch, "E327", {"start": v(56.08, 82.54) * mm, "end": v(55.6, 82.29) * mm});
            skLineSegment(sketch, "E328", {"start": v(55.6, 82.29) * mm, "end": v(55.15, 82.04) * mm});
            skLineSegment(sketch, "E329", {"start": v(55.15, 82.04) * mm, "end": v(54.71, 81.78) * mm});
            skLineSegment(sketch, "E330", {"start": v(54.71, 81.78) * mm, "end": v(54.29, 81.53) * mm});
            skLineSegment(sketch, "E331", {"start": v(54.29, 81.53) * mm, "end": v(53.87, 81.28) * mm});
            skLineSegment(sketch, "E332", {"start": v(53.87, 81.28) * mm, "end": v(53.47, 81.03) * mm});
            skLineSegment(sketch, "E333", {"start": v(53.47, 81.03) * mm, "end": v(53.08, 80.78) * mm});
            skLineSegment(sketch, "E334", {"start": v(53.08, 80.78) * mm, "end": v(52.7, 80.54) * mm});
            skLineSegment(sketch, "E335", {"start": v(52.7, 80.54) * mm, "end": v(52.34, 80.3) * mm});
            skLineSegment(sketch, "E336", {"start": v(52.34, 80.3) * mm, "end": v(52, 80.05) * mm});
            skLineSegment(sketch, "E337", {"start": v(52, 80.05) * mm, "end": v(51.65, 79.81) * mm});
            skLineSegment(sketch, "E338", {"start": v(51.65, 79.81) * mm, "end": v(51.33, 79.58) * mm});
            skLineSegment(sketch, "E339", {"start": v(51.33, 79.58) * mm, "end": v(51.01, 79.35) * mm});
            skLineSegment(sketch, "E340", {"start": v(51.01, 79.35) * mm, "end": v(50.71, 79.12) * mm});
            skLineSegment(sketch, "E341", {"start": v(50.71, 79.12) * mm, "end": v(50.43, 78.9) * mm});
            skLineSegment(sketch, "E342", {"start": v(50.43, 78.9) * mm, "end": v(50.15, 78.68) * mm});
            skLineSegment(sketch, "E343", {"start": v(50.15, 78.68) * mm, "end": v(49.89, 78.46) * mm});
            skLineSegment(sketch, "E344", {"start": v(49.89, 78.46) * mm, "end": v(49.63, 78.25) * mm});
            skLineSegment(sketch, "E345", {"start": v(49.63, 78.25) * mm, "end": v(49.4, 78.05) * mm});
            skLineSegment(sketch, "E346", {"start": v(49.4, 78.05) * mm, "end": v(49.16, 77.84) * mm});
            skLineSegment(sketch, "E347", {"start": v(49.16, 77.84) * mm, "end": v(48.94, 77.65) * mm});
            skLineSegment(sketch, "E348", {"start": v(48.94, 77.65) * mm, "end": v(48.31, 77.84) * mm});
            skLineSegment(sketch, "E349", {"start": v(48.31, 77.84) * mm, "end": v(45.8, 79.34) * mm});
            skLineSegment(sketch, "E350", {"start": v(45.8, 79.34) * mm, "end": v(45.34, 79.8) * mm});
            skLineSegment(sketch, "E351", {"start": v(45.34, 79.8) * mm, "end": v(45.41, 80.1) * mm});
            skLineSegment(sketch, "E352", {"start": v(45.41, 80.1) * mm, "end": v(45.48, 80.39) * mm});
            skLineSegment(sketch, "E353", {"start": v(45.48, 80.39) * mm, "end": v(45.55, 80.7) * mm});
            skLineSegment(sketch, "E354", {"start": v(45.55, 80.7) * mm, "end": v(45.61, 81.02) * mm});
            skLineSegment(sketch, "E355", {"start": v(45.61, 81.02) * mm, "end": v(45.68, 81.36) * mm});
            skLineSegment(sketch, "E356", {"start": v(45.68, 81.36) * mm, "end": v(45.74, 81.7) * mm});
            skLineSegment(sketch, "E357", {"start": v(45.74, 81.7) * mm, "end": v(45.8, 82.06) * mm});
            skLineSegment(sketch, "E358", {"start": v(45.8, 82.06) * mm, "end": v(45.86, 82.44) * mm});
            skLineSegment(sketch, "E359", {"start": v(45.86, 82.44) * mm, "end": v(45.92, 82.82) * mm});
            skLineSegment(sketch, "E360", {"start": v(45.92, 82.82) * mm, "end": v(45.97, 83.22) * mm});
            skLineSegment(sketch, "E361", {"start": v(45.97, 83.22) * mm, "end": v(46.02, 83.63) * mm});
            skLineSegment(sketch, "E362", {"start": v(46.02, 83.63) * mm, "end": v(46.07, 84.05) * mm});
            skLineSegment(sketch, "E363", {"start": v(46.07, 84.05) * mm, "end": v(46.11, 84.48) * mm});
            skLineSegment(sketch, "E364", {"start": v(46.11, 84.48) * mm, "end": v(46.15, 84.93) * mm});
            skLineSegment(sketch, "E365", {"start": v(46.15, 84.93) * mm, "end": v(46.19, 85.4) * mm});
            skLineSegment(sketch, "E366", {"start": v(46.19, 85.4) * mm, "end": v(46.22, 85.86) * mm});
            skLineSegment(sketch, "E367", {"start": v(46.22, 85.86) * mm, "end": v(46.24, 86.35) * mm});
            skLineSegment(sketch, "E368", {"start": v(46.24, 86.35) * mm, "end": v(46.26, 86.84) * mm});
            skLineSegment(sketch, "E369", {"start": v(46.26, 86.84) * mm, "end": v(46.28, 87.35) * mm});
            skLineSegment(sketch, "E370", {"start": v(46.28, 87.35) * mm, "end": v(46.29, 87.87) * mm});
            skLineSegment(sketch, "E371", {"start": v(46.29, 87.87) * mm, "end": v(46.29, 88.4) * mm});
            skLineSegment(sketch, "E372", {"start": v(46.29, 88.4) * mm, "end": v(46.29, 88.95) * mm});
            skLineSegment(sketch, "E373", {"start": v(46.29, 88.95) * mm, "end": v(46.28, 89.5) * mm});
            skLineSegment(sketch, "E374", {"start": v(46.28, 89.5) * mm, "end": v(46.26, 90.07) * mm});
            skLineSegment(sketch, "E375", {"start": v(46.26, 90.07) * mm, "end": v(46.24, 90.65) * mm});
            skLineSegment(sketch, "E376", {"start": v(46.24, 90.65) * mm, "end": v(46.2, 91.25) * mm});
            skLineSegment(sketch, "E377", {"start": v(46.2, 91.25) * mm, "end": v(46.17, 91.85) * mm});
            skLineSegment(sketch, "E378", {"start": v(46.17, 91.85) * mm, "end": v(46.12, 92.46) * mm});
            skLineSegment(sketch, "E379", {"start": v(46.12, 92.46) * mm, "end": v(46.06, 93.09) * mm});
            skLineSegment(sketch, "E380", {"start": v(46.06, 93.09) * mm, "end": v(46, 93.73) * mm});
            skLineSegment(sketch, "E381", {"start": v(46, 93.73) * mm, "end": v(45.93, 94.38) * mm});
            skLineSegment(sketch, "E382", {"start": v(45.93, 94.38) * mm, "end": v(45.85, 95.03) * mm});
            skLineSegment(sketch, "E383", {"start": v(45.85, 95.03) * mm, "end": v(45.65, 95.48) * mm});
            skLineSegment(sketch, "E384", {"start": v(45.65, 95.48) * mm, "end": v(43.5, 96.48) * mm});
            skLineSegment(sketch, "E385", {"start": v(43.5, 96.48) * mm, "end": v(43.04, 96.34) * mm});
            skLineSegment(sketch, "E386", {"start": v(43.04, 96.34) * mm, "end": v(42.48, 95.98) * mm});
            skLineSegment(sketch, "E387", {"start": v(42.48, 95.98) * mm, "end": v(41.94, 95.61) * mm});
            skLineSegment(sketch, "E388", {"start": v(41.94, 95.61) * mm, "end": v(41.41, 95.25) * mm});
            skLineSegment(sketch, "E389", {"start": v(41.41, 95.25) * mm, "end": v(40.9, 94.89) * mm});
            skLineSegment(sketch, "E390", {"start": v(40.9, 94.89) * mm, "end": v(40.4, 94.53) * mm});
            skLineSegment(sketch, "E391", {"start": v(40.4, 94.53) * mm, "end": v(39.91, 94.17) * mm});
            skLineSegment(sketch, "E392", {"start": v(39.91, 94.17) * mm, "end": v(39.44, 93.8) * mm});
            skLineSegment(sketch, "E393", {"start": v(39.44, 93.8) * mm, "end": v(38.98, 93.45) * mm});
            skLineSegment(sketch, "E394", {"start": v(38.98, 93.45) * mm, "end": v(38.54, 93.1) * mm});
            skLineSegment(sketch, "E395", {"start": v(38.54, 93.1) * mm, "end": v(38.1, 92.75) * mm});
            skLineSegment(sketch, "E396", {"start": v(38.1, 92.75) * mm, "end": v(37.69, 92.4) * mm});
            skLineSegment(sketch, "E397", {"start": v(37.69, 92.4) * mm, "end": v(37.28, 92.05) * mm});
            skLineSegment(sketch, "E398", {"start": v(37.28, 92.05) * mm, "end": v(36.9, 91.7) * mm});
            skLineSegment(sketch, "E399", {"start": v(36.9, 91.7) * mm, "end": v(36.51, 91.37) * mm});
            skLineSegment(sketch, "E400", {"start": v(36.51, 91.37) * mm, "end": v(36.15, 91.03) * mm});
            skLineSegment(sketch, "E401", {"start": v(36.15, 91.03) * mm, "end": v(35.8, 90.7) * mm});
            skLineSegment(sketch, "E402", {"start": v(35.8, 90.7) * mm, "end": v(35.45, 90.38) * mm});
            skLineSegment(sketch, "E403", {"start": v(35.45, 90.38) * mm, "end": v(35.12, 90.05) * mm});
            skLineSegment(sketch, "E404", {"start": v(35.12, 90.05) * mm, "end": v(34.8, 89.73) * mm});
            skLineSegment(sketch, "E405", {"start": v(34.8, 89.73) * mm, "end": v(34.5, 89.42) * mm});
            skLineSegment(sketch, "E406", {"start": v(34.5, 89.42) * mm, "end": v(34.21, 89.11) * mm});
            skLineSegment(sketch, "E407", {"start": v(34.21, 89.11) * mm, "end": v(33.93, 88.81) * mm});
            skLineSegment(sketch, "E408", {"start": v(33.93, 88.81) * mm, "end": v(33.66, 88.51) * mm});
            skLineSegment(sketch, "E409", {"start": v(33.66, 88.51) * mm, "end": v(33.4, 88.22) * mm});
            skLineSegment(sketch, "E410", {"start": v(33.4, 88.22) * mm, "end": v(33.16, 87.94) * mm});
            skLineSegment(sketch, "E411", {"start": v(33.16, 87.94) * mm, "end": v(32.92, 87.66) * mm});
            skLineSegment(sketch, "E412", {"start": v(32.92, 87.66) * mm, "end": v(32.7, 87.39) * mm});
            skLineSegment(sketch, "E413", {"start": v(32.7, 87.39) * mm, "end": v(32.48, 87.12) * mm});
            skLineSegment(sketch, "E414", {"start": v(32.48, 87.12) * mm, "end": v(32.28, 86.86) * mm});
            skLineSegment(sketch, "E415", {"start": v(32.28, 86.86) * mm, "end": v(32.09, 86.6) * mm});
            skLineSegment(sketch, "E416", {"start": v(32.09, 86.6) * mm, "end": v(31.9, 86.36) * mm});
            skLineSegment(sketch, "E417", {"start": v(31.9, 86.36) * mm, "end": v(31.73, 86.13) * mm});
            skLineSegment(sketch, "E418", {"start": v(31.73, 86.13) * mm, "end": v(31.07, 86.18) * mm});
            skLineSegment(sketch, "E419", {"start": v(31.07, 86.18) * mm, "end": v(28.3, 87.13) * mm});
            skLineSegment(sketch, "E420", {"start": v(28.3, 87.13) * mm, "end": v(27.76, 87.49) * mm});
            skLineSegment(sketch, "E421", {"start": v(27.76, 87.49) * mm, "end": v(27.77, 87.78) * mm});
            skLineSegment(sketch, "E422", {"start": v(27.77, 87.78) * mm, "end": v(27.77, 88.09) * mm});
            skLineSegment(sketch, "E423", {"start": v(27.77, 88.09) * mm, "end": v(27.77, 88.4) * mm});
            skLineSegment(sketch, "E424", {"start": v(27.77, 88.4) * mm, "end": v(27.77, 88.73) * mm});
            skLineSegment(sketch, "E425", {"start": v(27.77, 88.73) * mm, "end": v(27.76, 89.08) * mm});
            skLineSegment(sketch, "E426", {"start": v(27.76, 89.08) * mm, "end": v(27.76, 89.43) * mm});
            skLineSegment(sketch, "E427", {"start": v(27.76, 89.43) * mm, "end": v(27.74, 89.8) * mm});
            skLineSegment(sketch, "E428", {"start": v(27.74, 89.8) * mm, "end": v(27.72, 90.17) * mm});
            skLineSegment(sketch, "E429", {"start": v(27.72, 90.17) * mm, "end": v(27.7, 90.56) * mm});
            skLineSegment(sketch, "E430", {"start": v(27.7, 90.56) * mm, "end": v(27.67, 90.96) * mm});
            skLineSegment(sketch, "E431", {"start": v(27.67, 90.96) * mm, "end": v(27.63, 91.37) * mm});
            skLineSegment(sketch, "E432", {"start": v(27.63, 91.37) * mm, "end": v(27.59, 91.8) * mm});
            skLineSegment(sketch, "E433", {"start": v(27.59, 91.8) * mm, "end": v(27.54, 92.23) * mm});
            skLineSegment(sketch, "E434", {"start": v(27.54, 92.23) * mm, "end": v(27.48, 92.67) * mm});
            skLineSegment(sketch, "E435", {"start": v(27.48, 92.67) * mm, "end": v(27.42, 93.13) * mm});
            skLineSegment(sketch, "E436", {"start": v(27.42, 93.13) * mm, "end": v(27.35, 93.6) * mm});
            skLineSegment(sketch, "E437", {"start": v(27.35, 93.6) * mm, "end": v(27.28, 94.07) * mm});
            skLineSegment(sketch, "E438", {"start": v(27.28, 94.07) * mm, "end": v(27.2, 94.56) * mm});
            skLineSegment(sketch, "E439", {"start": v(27.2, 94.56) * mm, "end": v(27.1, 95.06) * mm});
            skLineSegment(sketch, "E440", {"start": v(27.1, 95.06) * mm, "end": v(27, 95.58) * mm});
            skLineSegment(sketch, "E441", {"start": v(27, 95.58) * mm, "end": v(26.9, 96.1) * mm});
            skLineSegment(sketch, "E442", {"start": v(26.9, 96.1) * mm, "end": v(26.78, 96.63) * mm});
            skLineSegment(sketch, "E443", {"start": v(26.78, 96.63) * mm, "end": v(26.66, 97.17) * mm});
            skLineSegment(sketch, "E444", {"start": v(26.66, 97.17) * mm, "end": v(26.52, 97.72) * mm});
            skLineSegment(sketch, "E445", {"start": v(26.52, 97.72) * mm, "end": v(26.38, 98.29) * mm});
            skLineSegment(sketch, "E446", {"start": v(26.38, 98.29) * mm, "end": v(26.22, 98.86) * mm});
            skLineSegment(sketch, "E447", {"start": v(26.22, 98.86) * mm, "end": v(26.06, 99.44) * mm});
            skLineSegment(sketch, "E448", {"start": v(26.06, 99.44) * mm, "end": v(25.89, 100.03) * mm});
            skLineSegment(sketch, "E449", {"start": v(25.89, 100.03) * mm, "end": v(25.7, 100.63) * mm});
            skLineSegment(sketch, "E450", {"start": v(25.7, 100.63) * mm, "end": v(25.5, 101.24) * mm});
            skLineSegment(sketch, "E451", {"start": v(25.5, 101.24) * mm, "end": v(25.3, 101.86) * mm});
            skLineSegment(sketch, "E452", {"start": v(25.3, 101.86) * mm, "end": v(25.09, 102.5) * mm});
            skLineSegment(sketch, "E453", {"start": v(25.09, 102.5) * mm, "end": v(24.8, 102.89) * mm});
            skLineSegment(sketch, "E454", {"start": v(24.8, 102.89) * mm, "end": v(22.5, 103.42) * mm});
            skLineSegment(sketch, "E455", {"start": v(22.5, 103.42) * mm, "end": v(22.07, 103.18) * mm});
            skLineSegment(sketch, "E456", {"start": v(22.07, 103.18) * mm, "end": v(21.6, 102.71) * mm});
            skLineSegment(sketch, "E457", {"start": v(21.6, 102.71) * mm, "end": v(21.15, 102.24) * mm});
            skLineSegment(sketch, "E458", {"start": v(21.15, 102.24) * mm, "end": v(20.7, 101.78) * mm});
            skLineSegment(sketch, "E459", {"start": v(20.7, 101.78) * mm, "end": v(20.28, 101.32) * mm});
            skLineSegment(sketch, "E460", {"start": v(20.28, 101.32) * mm, "end": v(19.86, 100.86) * mm});
            skLineSegment(sketch, "E461", {"start": v(19.86, 100.86) * mm, "end": v(19.46, 100.4) * mm});
            skLineSegment(sketch, "E462", {"start": v(19.46, 100.4) * mm, "end": v(19.08, 99.96) * mm});
            skLineSegment(sketch, "E463", {"start": v(19.08, 99.96) * mm, "end": v(18.7, 99.52) * mm});
            skLineSegment(sketch, "E464", {"start": v(18.7, 99.52) * mm, "end": v(18.34, 99.08) * mm});
            skLineSegment(sketch, "E465", {"start": v(18.34, 99.08) * mm, "end": v(18, 98.64) * mm});
            skLineSegment(sketch, "E466", {"start": v(18, 98.64) * mm, "end": v(17.65, 98.22) * mm});
            skLineSegment(sketch, "E467", {"start": v(17.65, 98.22) * mm, "end": v(17.33, 97.8) * mm});
            skLineSegment(sketch, "E468", {"start": v(17.33, 97.8) * mm, "end": v(17.02, 97.38) * mm});
            skLineSegment(sketch, "E469", {"start": v(17.02, 97.38) * mm, "end": v(16.72, 96.97) * mm});
            skLineSegment(sketch, "E470", {"start": v(16.72, 96.97) * mm, "end": v(16.43, 96.56) * mm});
            skLineSegment(sketch, "E471", {"start": v(16.43, 96.56) * mm, "end": v(16.15, 96.16) * mm});
            skLineSegment(sketch, "E472", {"start": v(16.15, 96.16) * mm, "end": v(15.89, 95.77) * mm});
            skLineSegment(sketch, "E473", {"start": v(15.89, 95.77) * mm, "end": v(15.63, 95.39) * mm});
            skLineSegment(sketch, "E474", {"start": v(15.63, 95.39) * mm, "end": v(15.39, 95.01) * mm});
            skLineSegment(sketch, "E475", {"start": v(15.39, 95.01) * mm, "end": v(15.16, 94.64) * mm});
            skLineSegment(sketch, "E476", {"start": v(15.16, 94.64) * mm, "end": v(14.94, 94.28) * mm});
            skLineSegment(sketch, "E477", {"start": v(14.94, 94.28) * mm, "end": v(14.72, 93.92) * mm});
            skLineSegment(sketch, "E478", {"start": v(14.72, 93.92) * mm, "end": v(14.52, 93.58) * mm});
            skLineSegment(sketch, "E479", {"start": v(14.52, 93.58) * mm, "end": v(14.33, 93.24) * mm});
            skLineSegment(sketch, "E480", {"start": v(14.33, 93.24) * mm, "end": v(14.15, 92.9) * mm});
            skLineSegment(sketch, "E481", {"start": v(14.15, 92.9) * mm, "end": v(13.98, 92.59) * mm});
            skLineSegment(sketch, "E482", {"start": v(13.98, 92.59) * mm, "end": v(13.81, 92.27) * mm});
            skLineSegment(sketch, "E483", {"start": v(13.81, 92.27) * mm, "end": v(13.66, 91.97) * mm});
            skLineSegment(sketch, "E484", {"start": v(13.66, 91.97) * mm, "end": v(13.51, 91.67) * mm});
            skLineSegment(sketch, "E485", {"start": v(13.51, 91.67) * mm, "end": v(13.38, 91.39) * mm});
            skLineSegment(sketch, "E486", {"start": v(13.38, 91.39) * mm, "end": v(13.25, 91.11) * mm});
            skLineSegment(sketch, "E487", {"start": v(13.25, 91.11) * mm, "end": v(13.13, 90.84) * mm});
            skLineSegment(sketch, "E488", {"start": v(13.13, 90.84) * mm, "end": v(12.48, 90.76) * mm});
            skLineSegment(sketch, "E489", {"start": v(12.48, 90.76) * mm, "end": v(9.58, 91.11) * mm});
            skLineSegment(sketch, "E490", {"start": v(9.58, 91.11) * mm, "end": v(8.96, 91.35) * mm});
            skLineSegment(sketch, "E491", {"start": v(8.96, 91.35) * mm, "end": v(8.9, 91.64) * mm});
            skLineSegment(sketch, "E492", {"start": v(8.9, 91.64) * mm, "end": v(8.85, 91.94) * mm});
            skLineSegment(sketch, "E493", {"start": v(8.85, 91.94) * mm, "end": v(8.79, 92.25) * mm});
            skLineSegment(sketch, "E494", {"start": v(8.79, 92.25) * mm, "end": v(8.72, 92.57) * mm});
            skLineSegment(sketch, "E495", {"start": v(8.72, 92.57) * mm, "end": v(8.64, 92.9) * mm});
            skLineSegment(sketch, "E496", {"start": v(8.64, 92.9) * mm, "end": v(8.55, 93.24) * mm});
            skLineSegment(sketch, "E497", {"start": v(8.55, 93.24) * mm, "end": v(8.47, 93.6) * mm});
            skLineSegment(sketch, "E498", {"start": v(8.47, 93.6) * mm, "end": v(8.37, 93.96) * mm});
            skLineSegment(sketch, "E499", {"start": v(8.37, 93.96) * mm, "end": v(8.26, 94.34) * mm});
            skLineSegment(sketch, "E500", {"start": v(8.26, 94.34) * mm, "end": v(8.15, 94.72) * mm});
            skLineSegment(sketch, "E501", {"start": v(8.15, 94.72) * mm, "end": v(8.03, 95.12) * mm});
            skLineSegment(sketch, "E502", {"start": v(8.03, 95.12) * mm, "end": v(7.9, 95.52) * mm});
            skLineSegment(sketch, "E503", {"start": v(7.9, 95.52) * mm, "end": v(7.76, 95.93) * mm});
            skLineSegment(sketch, "E504", {"start": v(7.76, 95.93) * mm, "end": v(7.62, 96.36) * mm});
            skLineSegment(sketch, "E505", {"start": v(7.62, 96.36) * mm, "end": v(7.46, 96.8) * mm});
            skLineSegment(sketch, "E506", {"start": v(7.46, 96.8) * mm, "end": v(7.3, 97.24) * mm});
            skLineSegment(sketch, "E507", {"start": v(7.3, 97.24) * mm, "end": v(7.12, 97.69) * mm});
            skLineSegment(sketch, "E508", {"start": v(7.12, 97.69) * mm, "end": v(6.94, 98.15) * mm});
            skLineSegment(sketch, "E509", {"start": v(6.94, 98.15) * mm, "end": v(6.75, 98.62) * mm});
            skLineSegment(sketch, "E510", {"start": v(6.75, 98.62) * mm, "end": v(6.54, 99.1) * mm});
            skLineSegment(sketch, "E511", {"start": v(6.54, 99.1) * mm, "end": v(6.33, 99.59) * mm});
            skLineSegment(sketch, "E512", {"start": v(6.33, 99.59) * mm, "end": v(6.1, 100.09) * mm});
            skLineSegment(sketch, "E513", {"start": v(6.1, 100.09) * mm, "end": v(5.87, 100.59) * mm});
            skLineSegment(sketch, "E514", {"start": v(5.87, 100.59) * mm, "end": v(5.62, 101.1) * mm});
            skLineSegment(sketch, "E515", {"start": v(5.62, 101.1) * mm, "end": v(5.37, 101.62) * mm});
            skLineSegment(sketch, "E516", {"start": v(5.37, 101.62) * mm, "end": v(5.1, 102.15) * mm});
            skLineSegment(sketch, "E517", {"start": v(5.1, 102.15) * mm, "end": v(4.82, 102.69) * mm});
            skLineSegment(sketch, "E518", {"start": v(4.82, 102.69) * mm, "end": v(4.52, 103.23) * mm});
            skLineSegment(sketch, "E519", {"start": v(4.52, 103.23) * mm, "end": v(4.22, 103.78) * mm});
            skLineSegment(sketch, "E520", {"start": v(4.22, 103.78) * mm, "end": v(3.9, 104.33) * mm});
            skLineSegment(sketch, "E521", {"start": v(3.9, 104.33) * mm, "end": v(3.57, 104.9) * mm});
            skLineSegment(sketch, "E522", {"start": v(3.57, 104.9) * mm, "end": v(3.23, 105.47) * mm});
            skLineSegment(sketch, "E523", {"start": v(3.23, 105.47) * mm, "end": v(2.87, 105.8) * mm});
            skLineSegment(sketch, "E524", {"start": v(2.87, 105.8) * mm, "end": v(0.5, 105.83) * mm});
            skLineSegment(sketch, "E525", {"start": v(0.5, 105.83) * mm, "end": v(0.13, 105.52) * mm});
            skLineSegment(sketch, "E526", {"start": v(0.13, 105.52) * mm, "end": v(-0.23, 104.96) * mm});
            skLineSegment(sketch, "E527", {"start": v(-0.23, 104.96) * mm, "end": v(-0.57, 104.4) * mm});
            skLineSegment(sketch, "E528", {"start": v(-0.57, 104.4) * mm, "end": v(-0.9, 103.86) * mm});
            skLineSegment(sketch, "E529", {"start": v(-0.9, 103.86) * mm, "end": v(-1.23, 103.32) * mm});
            skLineSegment(sketch, "E530", {"start": v(-1.23, 103.32) * mm, "end": v(-1.54, 102.79) * mm});
            skLineSegment(sketch, "E531", {"start": v(-1.54, 102.79) * mm, "end": v(-1.84, 102.26) * mm});
            skLineSegment(sketch, "E532", {"start": v(-1.84, 102.26) * mm, "end": v(-2.12, 101.74) * mm});
            skLineSegment(sketch, "E533", {"start": v(-2.12, 101.74) * mm, "end": v(-2.4, 101.23) * mm});
            skLineSegment(sketch, "E534", {"start": v(-2.4, 101.23) * mm, "end": v(-2.66, 100.73) * mm});
            skLineSegment(sketch, "E535", {"start": v(-2.66, 100.73) * mm, "end": v(-2.91, 100.23) * mm});
            skLineSegment(sketch, "E536", {"start": v(-2.91, 100.23) * mm, "end": v(-3.15, 99.74) * mm});
            skLineSegment(sketch, "E537", {"start": v(-3.15, 99.74) * mm, "end": v(-3.38, 99.26) * mm});
            skLineSegment(sketch, "E538", {"start": v(-3.38, 99.26) * mm, "end": v(-3.6, 98.79) * mm});
            skLineSegment(sketch, "E539", {"start": v(-3.6, 98.79) * mm, "end": v(-3.8, 98.32) * mm});
            skLineSegment(sketch, "E540", {"start": v(-3.8, 98.32) * mm, "end": v(-4, 97.87) * mm});
            skLineSegment(sketch, "E541", {"start": v(-4, 97.87) * mm, "end": v(-4.2, 97.42) * mm});
            skLineSegment(sketch, "E542", {"start": v(-4.2, 97.42) * mm, "end": v(-4.37, 96.98) * mm});
            skLineSegment(sketch, "E543", {"start": v(-4.37, 96.98) * mm, "end": v(-4.54, 96.55) * mm});
            skLineSegment(sketch, "E544", {"start": v(-4.54, 96.55) * mm, "end": v(-4.7, 96.13) * mm});
            skLineSegment(sketch, "E545", {"start": v(-4.7, 96.13) * mm, "end": v(-4.85, 95.72) * mm});
            skLineSegment(sketch, "E546", {"start": v(-4.85, 95.72) * mm, "end": v(-5, 95.32) * mm});
            skLineSegment(sketch, "E547", {"start": v(-5, 95.32) * mm, "end": v(-5.13, 94.93) * mm});
            skLineSegment(sketch, "E548", {"start": v(-5.13, 94.93) * mm, "end": v(-5.25, 94.55) * mm});
            skLineSegment(sketch, "E549", {"start": v(-5.25, 94.55) * mm, "end": v(-5.37, 94.18) * mm});
            skLineSegment(sketch, "E550", {"start": v(-5.37, 94.18) * mm, "end": v(-5.48, 93.82) * mm});
            skLineSegment(sketch, "E551", {"start": v(-5.48, 93.82) * mm, "end": v(-5.58, 93.47) * mm});
            skLineSegment(sketch, "E552", {"start": v(-5.58, 93.47) * mm, "end": v(-5.67, 93.13) * mm});
            skLineSegment(sketch, "E553", {"start": v(-5.67, 93.13) * mm, "end": v(-5.76, 92.8) * mm});
            skLineSegment(sketch, "E554", {"start": v(-5.76, 92.8) * mm, "end": v(-5.84, 92.48) * mm});
            skLineSegment(sketch, "E555", {"start": v(-5.84, 92.48) * mm, "end": v(-5.91, 92.17) * mm});
            skLineSegment(sketch, "E556", {"start": v(-5.91, 92.17) * mm, "end": v(-5.98, 91.87) * mm});
            skLineSegment(sketch, "E557", {"start": v(-5.98, 91.87) * mm, "end": v(-6.04, 91.59) * mm});
            skLineSegment(sketch, "E558", {"start": v(-6.04, 91.59) * mm, "end": v(-6.67, 91.37) * mm});
            skLineSegment(sketch, "E559", {"start": v(-6.67, 91.37) * mm, "end": v(-9.58, 91.11) * mm});
            skLineSegment(sketch, "E560", {"start": v(-9.58, 91.11) * mm, "end": v(-10.23, 91.22) * mm});
            skLineSegment(sketch, "E561", {"start": v(-10.23, 91.22) * mm, "end": v(-10.34, 91.49) * mm});
            skLineSegment(sketch, "E562", {"start": v(-10.34, 91.49) * mm, "end": v(-10.46, 91.77) * mm});
            skLineSegment(sketch, "E563", {"start": v(-10.46, 91.77) * mm, "end": v(-10.58, 92.06) * mm});
            skLineSegment(sketch, "E564", {"start": v(-10.58, 92.06) * mm, "end": v(-10.72, 92.36) * mm});
            skLineSegment(sketch, "E565", {"start": v(-10.72, 92.36) * mm, "end": v(-10.87, 92.67) * mm});
            skLineSegment(sketch, "E566", {"start": v(-10.87, 92.67) * mm, "end": v(-11.02, 92.98) * mm});
            skLineSegment(sketch, "E567", {"start": v(-11.02, 92.98) * mm, "end": v(-11.18, 93.31) * mm});
            skLineSegment(sketch, "E568", {"start": v(-11.18, 93.31) * mm, "end": v(-11.35, 93.65) * mm});
            skLineSegment(sketch, "E569", {"start": v(-11.35, 93.65) * mm, "end": v(-11.53, 94) * mm});
            skLineSegment(sketch, "E570", {"start": v(-11.53, 94) * mm, "end": v(-11.72, 94.35) * mm});
            skLineSegment(sketch, "E571", {"start": v(-11.72, 94.35) * mm, "end": v(-11.92, 94.7) * mm});
            skLineSegment(sketch, "E572", {"start": v(-11.92, 94.7) * mm, "end": v(-12.13, 95.08) * mm});
            skLineSegment(sketch, "E573", {"start": v(-12.13, 95.08) * mm, "end": v(-12.35, 95.45) * mm});
            skLineSegment(sketch, "E574", {"start": v(-12.35, 95.45) * mm, "end": v(-12.58, 95.84) * mm});
            skLineSegment(sketch, "E575", {"start": v(-12.58, 95.84) * mm, "end": v(-12.83, 96.23) * mm});
            skLineSegment(sketch, "E576", {"start": v(-12.83, 96.23) * mm, "end": v(-13.08, 96.63) * mm});
            skLineSegment(sketch, "E577", {"start": v(-13.08, 96.63) * mm, "end": v(-13.34, 97.04) * mm});
            skLineSegment(sketch, "E578", {"start": v(-13.34, 97.04) * mm, "end": v(-13.62, 97.45) * mm});
            skLineSegment(sketch, "E579", {"start": v(-13.62, 97.45) * mm, "end": v(-13.9, 97.87) * mm});
            skLineSegment(sketch, "E580", {"start": v(-13.9, 97.87) * mm, "end": v(-14.2, 98.3) * mm});
            skLineSegment(sketch, "E581", {"start": v(-14.2, 98.3) * mm, "end": v(-14.52, 98.73) * mm});
            skLineSegment(sketch, "E582", {"start": v(-14.52, 98.73) * mm, "end": v(-14.84, 99.17) * mm});
            skLineSegment(sketch, "E583", {"start": v(-14.84, 99.17) * mm, "end": v(-15.17, 99.61) * mm});
            skLineSegment(sketch, "E584", {"start": v(-15.17, 99.61) * mm, "end": v(-15.52, 100.06) * mm});
            skLineSegment(sketch, "E585", {"start": v(-15.52, 100.06) * mm, "end": v(-15.88, 100.52) * mm});
            skLineSegment(sketch, "E586", {"start": v(-15.88, 100.52) * mm, "end": v(-16.25, 100.98) * mm});
            skLineSegment(sketch, "E587", {"start": v(-16.25, 100.98) * mm, "end": v(-16.64, 101.44) * mm});
            skLineSegment(sketch, "E588", {"start": v(-16.64, 101.44) * mm, "end": v(-17.04, 101.91) * mm});
            skLineSegment(sketch, "E589", {"start": v(-17.04, 101.91) * mm, "end": v(-17.45, 102.39) * mm});
            skLineSegment(sketch, "E590", {"start": v(-17.45, 102.39) * mm, "end": v(-17.88, 102.86) * mm});
            skLineSegment(sketch, "E591", {"start": v(-17.88, 102.86) * mm, "end": v(-18.31, 103.35) * mm});
            skLineSegment(sketch, "E592", {"start": v(-18.31, 103.35) * mm, "end": v(-18.77, 103.83) * mm});
            skLineSegment(sketch, "E593", {"start": v(-18.77, 103.83) * mm, "end": v(-19.19, 104.08) * mm});
            skLineSegment(sketch, "E594", {"start": v(-19.19, 104.08) * mm, "end": v(-21.51, 103.62) * mm});
            skLineSegment(sketch, "E595", {"start": v(-21.51, 103.62) * mm, "end": v(-21.8, 103.24) * mm});
            skLineSegment(sketch, "E596", {"start": v(-21.8, 103.24) * mm, "end": v(-22.04, 102.62) * mm});
            skLineSegment(sketch, "E597", {"start": v(-22.04, 102.62) * mm, "end": v(-22.27, 102) * mm});
            skLineSegment(sketch, "E598", {"start": v(-22.27, 102) * mm, "end": v(-22.48, 101.4) * mm});
            skLineSegment(sketch, "E599", {"start": v(-22.48, 101.4) * mm, "end": v(-22.69, 100.8) * mm});
            skLineSegment(sketch, "E600", {"start": v(-22.69, 100.8) * mm, "end": v(-22.88, 100.22) * mm});
            skLineSegment(sketch, "E601", {"start": v(-22.88, 100.22) * mm, "end": v(-23.06, 99.64) * mm});
            skLineSegment(sketch, "E602", {"start": v(-23.06, 99.64) * mm, "end": v(-23.23, 99.08) * mm});
            skLineSegment(sketch, "E603", {"start": v(-23.23, 99.08) * mm, "end": v(-23.4, 98.52) * mm});
            skLineSegment(sketch, "E604", {"start": v(-23.4, 98.52) * mm, "end": v(-23.54, 97.97) * mm});
            skLineSegment(sketch, "E605", {"start": v(-23.54, 97.97) * mm, "end": v(-23.69, 97.43) * mm});
            skLineSegment(sketch, "E606", {"start": v(-23.69, 97.43) * mm, "end": v(-23.82, 96.9) * mm});
            skLineSegment(sketch, "E607", {"start": v(-23.82, 96.9) * mm, "end": v(-23.94, 96.39) * mm});
            skLineSegment(sketch, "E608", {"start": v(-23.94, 96.39) * mm, "end": v(-24.06, 95.88) * mm});
            skLineSegment(sketch, "E609", {"start": v(-24.06, 95.88) * mm, "end": v(-24.17, 95.38) * mm});
            skLineSegment(sketch, "E610", {"start": v(-24.17, 95.38) * mm, "end": v(-24.27, 94.9) * mm});
            skLineSegment(sketch, "E611", {"start": v(-24.27, 94.9) * mm, "end": v(-24.36, 94.42) * mm});
            skLineSegment(sketch, "E612", {"start": v(-24.36, 94.42) * mm, "end": v(-24.44, 93.95) * mm});
            skLineSegment(sketch, "E613", {"start": v(-24.44, 93.95) * mm, "end": v(-24.52, 93.5) * mm});
            skLineSegment(sketch, "E614", {"start": v(-24.52, 93.5) * mm, "end": v(-24.59, 93.06) * mm});
            skLineSegment(sketch, "E615", {"start": v(-24.59, 93.06) * mm, "end": v(-24.65, 92.62) * mm});
            skLineSegment(sketch, "E616", {"start": v(-24.65, 92.62) * mm, "end": v(-24.7, 92.2) * mm});
            skLineSegment(sketch, "E617", {"start": v(-24.7, 92.2) * mm, "end": v(-24.75, 91.8) * mm});
            skLineSegment(sketch, "E618", {"start": v(-24.75, 91.8) * mm, "end": v(-24.8, 91.4) * mm});
            skLineSegment(sketch, "E619", {"start": v(-24.8, 91.4) * mm, "end": v(-24.83, 91) * mm});
            skLineSegment(sketch, "E620", {"start": v(-24.83, 91) * mm, "end": v(-24.86, 90.63) * mm});
            skLineSegment(sketch, "E621", {"start": v(-24.86, 90.63) * mm, "end": v(-24.9, 90.27) * mm});
            skLineSegment(sketch, "E622", {"start": v(-24.9, 90.27) * mm, "end": v(-24.91, 89.91) * mm});
            skLineSegment(sketch, "E623", {"start": v(-24.91, 89.91) * mm, "end": v(-24.93, 89.57) * mm});
            skLineSegment(sketch, "E624", {"start": v(-24.93, 89.57) * mm, "end": v(-24.94, 89.24) * mm});
            skLineSegment(sketch, "E625", {"start": v(-24.94, 89.24) * mm, "end": v(-24.95, 88.93) * mm});
            skLineSegment(sketch, "E626", {"start": v(-24.95, 88.93) * mm, "end": v(-24.95, 88.62) * mm});
            skLineSegment(sketch, "E627", {"start": v(-24.95, 88.62) * mm, "end": v(-24.96, 88.33) * mm});
            skLineSegment(sketch, "E628", {"start": v(-24.96, 88.33) * mm, "end": v(-25.52, 87.99) * mm});
            skLineSegment(sketch, "E629", {"start": v(-25.52, 87.99) * mm, "end": v(-28.3, 87.13) * mm});
            skLineSegment(sketch, "E630", {"start": v(-28.3, 87.13) * mm, "end": v(-28.97, 87.1) * mm});
            skLineSegment(sketch, "E631", {"start": v(-28.97, 87.1) * mm, "end": v(-29.13, 87.34) * mm});
            skLineSegment(sketch, "E632", {"start": v(-29.13, 87.34) * mm, "end": v(-29.3, 87.59) * mm});
            skLineSegment(sketch, "E633", {"start": v(-29.3, 87.59) * mm, "end": v(-29.5, 87.85) * mm});
            skLineSegment(sketch, "E634", {"start": v(-29.5, 87.85) * mm, "end": v(-29.69, 88.11) * mm});
            skLineSegment(sketch, "E635", {"start": v(-29.69, 88.11) * mm, "end": v(-29.9, 88.38) * mm});
            skLineSegment(sketch, "E636", {"start": v(-29.9, 88.38) * mm, "end": v(-30.11, 88.66) * mm});
            skLineSegment(sketch, "E637", {"start": v(-30.11, 88.66) * mm, "end": v(-30.34, 88.95) * mm});
            skLineSegment(sketch, "E638", {"start": v(-30.34, 88.95) * mm, "end": v(-30.57, 89.24) * mm});
            skLineSegment(sketch, "E639", {"start": v(-30.57, 89.24) * mm, "end": v(-30.82, 89.54) * mm});
            skLineSegment(sketch, "E640", {"start": v(-30.82, 89.54) * mm, "end": v(-31.08, 89.85) * mm});
            skLineSegment(sketch, "E641", {"start": v(-31.08, 89.85) * mm, "end": v(-31.35, 90.16) * mm});
            skLineSegment(sketch, "E642", {"start": v(-31.35, 90.16) * mm, "end": v(-31.63, 90.48) * mm});
            skLineSegment(sketch, "E643", {"start": v(-31.63, 90.48) * mm, "end": v(-31.93, 90.8) * mm});
            skLineSegment(sketch, "E644", {"start": v(-31.93, 90.8) * mm, "end": v(-32.24, 91.13) * mm});
            skLineSegment(sketch, "E645", {"start": v(-32.24, 91.13) * mm, "end": v(-32.55, 91.46) * mm});
            skLineSegment(sketch, "E646", {"start": v(-32.55, 91.46) * mm, "end": v(-32.88, 91.8) * mm});
            skLineSegment(sketch, "E647", {"start": v(-32.88, 91.8) * mm, "end": v(-33.23, 92.14) * mm});
            skLineSegment(sketch, "E648", {"start": v(-33.23, 92.14) * mm, "end": v(-33.58, 92.49) * mm});
            skLineSegment(sketch, "E649", {"start": v(-33.58, 92.49) * mm, "end": v(-33.95, 92.84) * mm});
            skLineSegment(sketch, "E650", {"start": v(-33.95, 92.84) * mm, "end": v(-34.33, 93.2) * mm});
            skLineSegment(sketch, "E651", {"start": v(-34.33, 93.2) * mm, "end": v(-34.72, 93.55) * mm});
            skLineSegment(sketch, "E652", {"start": v(-34.72, 93.55) * mm, "end": v(-35.13, 93.91) * mm});
            skLineSegment(sketch, "E653", {"start": v(-35.13, 93.91) * mm, "end": v(-35.55, 94.28) * mm});
            skLineSegment(sketch, "E654", {"start": v(-35.55, 94.28) * mm, "end": v(-35.98, 94.65) * mm});
            skLineSegment(sketch, "E655", {"start": v(-35.98, 94.65) * mm, "end": v(-36.43, 95.02) * mm});
            skLineSegment(sketch, "E656", {"start": v(-36.43, 95.02) * mm, "end": v(-36.9, 95.4) * mm});
            skLineSegment(sketch, "E657", {"start": v(-36.9, 95.4) * mm, "end": v(-37.37, 95.77) * mm});
            skLineSegment(sketch, "E658", {"start": v(-37.37, 95.77) * mm, "end": v(-37.85, 96.14) * mm});
            skLineSegment(sketch, "E659", {"start": v(-37.85, 96.14) * mm, "end": v(-38.36, 96.52) * mm});
            skLineSegment(sketch, "E660", {"start": v(-38.36, 96.52) * mm, "end": v(-38.87, 96.9) * mm});
            skLineSegment(sketch, "E661", {"start": v(-38.87, 96.9) * mm, "end": v(-39.4, 97.28) * mm});
            skLineSegment(sketch, "E662", {"start": v(-39.4, 97.28) * mm, "end": v(-39.95, 97.66) * mm});
            skLineSegment(sketch, "E663", {"start": v(-39.95, 97.66) * mm, "end": v(-40.4, 97.81) * mm});
            skLineSegment(sketch, "E664", {"start": v(-40.4, 97.81) * mm, "end": v(-42.58, 96.89) * mm});
            skLineSegment(sketch, "E665", {"start": v(-42.58, 96.89) * mm, "end": v(-42.8, 96.45) * mm});
            skLineSegment(sketch, "E666", {"start": v(-42.8, 96.45) * mm, "end": v(-42.9, 95.8) * mm});
            skLineSegment(sketch, "E667", {"start": v(-42.9, 95.8) * mm, "end": v(-42.99, 95.15) * mm});
            skLineSegment(sketch, "E668", {"start": v(-42.99, 95.15) * mm, "end": v(-43.07, 94.5) * mm});
            skLineSegment(sketch, "E669", {"start": v(-43.07, 94.5) * mm, "end": v(-43.15, 93.89) * mm});
            skLineSegment(sketch, "E670", {"start": v(-43.15, 93.89) * mm, "end": v(-43.21, 93.27) * mm});
            skLineSegment(sketch, "E671", {"start": v(-43.21, 93.27) * mm, "end": v(-43.27, 92.67) * mm});
            skLineSegment(sketch, "E672", {"start": v(-43.27, 92.67) * mm, "end": v(-43.32, 92.08) * mm});
            skLineSegment(sketch, "E673", {"start": v(-43.32, 92.08) * mm, "end": v(-43.36, 91.5) * mm});
            skLineSegment(sketch, "E674", {"start": v(-43.36, 91.5) * mm, "end": v(-43.4, 90.94) * mm});
            skLineSegment(sketch, "E675", {"start": v(-43.4, 90.94) * mm, "end": v(-43.43, 90.38) * mm});
            skLineSegment(sketch, "E676", {"start": v(-43.43, 90.38) * mm, "end": v(-43.45, 89.84) * mm});
            skLineSegment(sketch, "E677", {"start": v(-43.45, 89.84) * mm, "end": v(-43.46, 89.3) * mm});
            skLineSegment(sketch, "E678", {"start": v(-43.46, 89.3) * mm, "end": v(-43.47, 88.78) * mm});
            skLineSegment(sketch, "E679", {"start": v(-43.47, 88.78) * mm, "end": v(-43.47, 88.27) * mm});
            skLineSegment(sketch, "E680", {"start": v(-43.47, 88.27) * mm, "end": v(-43.46, 87.78) * mm});
            skLineSegment(sketch, "E681", {"start": v(-43.46, 87.78) * mm, "end": v(-43.46, 87.3) * mm});
            skLineSegment(sketch, "E682", {"start": v(-43.46, 87.3) * mm, "end": v(-43.44, 86.82) * mm});
            skLineSegment(sketch, "E683", {"start": v(-43.44, 86.82) * mm, "end": v(-43.42, 86.36) * mm});
            skLineSegment(sketch, "E684", {"start": v(-43.42, 86.36) * mm, "end": v(-43.4, 85.91) * mm});
            skLineSegment(sketch, "E685", {"start": v(-43.4, 85.91) * mm, "end": v(-43.37, 85.48) * mm});
            skLineSegment(sketch, "E686", {"start": v(-43.37, 85.48) * mm, "end": v(-43.33, 85.05) * mm});
            skLineSegment(sketch, "E687", {"start": v(-43.33, 85.05) * mm, "end": v(-43.3, 84.64) * mm});
            skLineSegment(sketch, "E688", {"start": v(-43.3, 84.64) * mm, "end": v(-43.26, 84.24) * mm});
            skLineSegment(sketch, "E689", {"start": v(-43.26, 84.24) * mm, "end": v(-43.21, 83.85) * mm});
            skLineSegment(sketch, "E690", {"start": v(-43.21, 83.85) * mm, "end": v(-43.16, 83.48) * mm});
            skLineSegment(sketch, "E691", {"start": v(-43.16, 83.48) * mm, "end": v(-43.11, 83.12) * mm});
            skLineSegment(sketch, "E692", {"start": v(-43.11, 83.12) * mm, "end": v(-43.06, 82.77) * mm});
            skLineSegment(sketch, "E693", {"start": v(-43.06, 82.77) * mm, "end": v(-43, 82.43) * mm});
            skLineSegment(sketch, "E694", {"start": v(-43, 82.43) * mm, "end": v(-42.95, 82.1) * mm});
            skLineSegment(sketch, "E695", {"start": v(-42.95, 82.1) * mm, "end": v(-42.9, 81.8) * mm});
            skLineSegment(sketch, "E696", {"start": v(-42.9, 81.8) * mm, "end": v(-42.83, 81.5) * mm});
            skLineSegment(sketch, "E697", {"start": v(-42.83, 81.5) * mm, "end": v(-42.77, 81.21) * mm});
            skLineSegment(sketch, "E698", {"start": v(-42.77, 81.21) * mm, "end": v(-43.25, 80.76) * mm});
            skLineSegment(sketch, "E699", {"start": v(-43.25, 80.76) * mm, "end": v(-45.8, 79.34) * mm});
            skLineSegment(sketch, "E700", {"start": v(-45.8, 79.34) * mm, "end": v(-46.44, 79.17) * mm});
            skLineSegment(sketch, "E701", {"start": v(-46.44, 79.17) * mm, "end": v(-46.66, 79.37) * mm});
            skLineSegment(sketch, "E702", {"start": v(-46.66, 79.37) * mm, "end": v(-46.88, 79.58) * mm});
            skLineSegment(sketch, "E703", {"start": v(-46.88, 79.58) * mm, "end": v(-47.11, 79.8) * mm});
            skLineSegment(sketch, "E704", {"start": v(-47.11, 79.8) * mm, "end": v(-47.36, 80.01) * mm});
            skLineSegment(sketch, "E705", {"start": v(-47.36, 80.01) * mm, "end": v(-47.62, 80.24) * mm});
            skLineSegment(sketch, "E706", {"start": v(-47.62, 80.24) * mm, "end": v(-47.89, 80.46) * mm});
            skLineSegment(sketch, "E707", {"start": v(-47.89, 80.46) * mm, "end": v(-48.17, 80.7) * mm});
            skLineSegment(sketch, "E708", {"start": v(-48.17, 80.7) * mm, "end": v(-48.46, 80.93) * mm});
            skLineSegment(sketch, "E709", {"start": v(-48.46, 80.93) * mm, "end": v(-48.76, 81.18) * mm});
            skLineSegment(sketch, "E710", {"start": v(-48.76, 81.18) * mm, "end": v(-49.08, 81.42) * mm});
            skLineSegment(sketch, "E711", {"start": v(-49.08, 81.42) * mm, "end": v(-49.41, 81.67) * mm});
            skLineSegment(sketch, "E712", {"start": v(-49.41, 81.67) * mm, "end": v(-49.75, 81.92) * mm});
            skLineSegment(sketch, "E713", {"start": v(-49.75, 81.92) * mm, "end": v(-50.1, 82.18) * mm});
            skLineSegment(sketch, "E714", {"start": v(-50.1, 82.18) * mm, "end": v(-50.48, 82.43) * mm});
            skLineSegment(sketch, "E715", {"start": v(-50.48, 82.43) * mm, "end": v(-50.86, 82.7) * mm});
            skLineSegment(sketch, "E716", {"start": v(-50.86, 82.7) * mm, "end": v(-51.25, 82.95) * mm});
            skLineSegment(sketch, "E717", {"start": v(-51.25, 82.95) * mm, "end": v(-51.66, 83.22) * mm});
            skLineSegment(sketch, "E718", {"start": v(-51.66, 83.22) * mm, "end": v(-52.08, 83.49) * mm});
            skLineSegment(sketch, "E719", {"start": v(-52.08, 83.49) * mm, "end": v(-52.51, 83.75) * mm});
            skLineSegment(sketch, "E720", {"start": v(-52.51, 83.75) * mm, "end": v(-52.96, 84.02) * mm});
            skLineSegment(sketch, "E721", {"start": v(-52.96, 84.02) * mm, "end": v(-53.42, 84.29) * mm});
            skLineSegment(sketch, "E722", {"start": v(-53.42, 84.29) * mm, "end": v(-53.89, 84.56) * mm});
            skLineSegment(sketch, "E723", {"start": v(-53.89, 84.56) * mm, "end": v(-54.38, 84.83) * mm});
            skLineSegment(sketch, "E724", {"start": v(-54.38, 84.83) * mm, "end": v(-54.88, 85.1) * mm});
            skLineSegment(sketch, "E725", {"start": v(-54.88, 85.1) * mm, "end": v(-55.4, 85.37) * mm});
            skLineSegment(sketch, "E726", {"start": v(-55.4, 85.37) * mm, "end": v(-55.92, 85.64) * mm});
            skLineSegment(sketch, "E727", {"start": v(-55.92, 85.64) * mm, "end": v(-56.46, 85.9) * mm});
            skLineSegment(sketch, "E728", {"start": v(-56.46, 85.9) * mm, "end": v(-57.02, 86.17) * mm});
            skLineSegment(sketch, "E729", {"start": v(-57.02, 86.17) * mm, "end": v(-57.59, 86.44) * mm});
            skLineSegment(sketch, "E730", {"start": v(-57.59, 86.44) * mm, "end": v(-58.17, 86.7) * mm});
            skLineSegment(sketch, "E731", {"start": v(-58.17, 86.7) * mm, "end": v(-58.77, 86.96) * mm});
            skLineSegment(sketch, "E732", {"start": v(-58.77, 86.96) * mm, "end": v(-59.38, 87.22) * mm});
            skLineSegment(sketch, "E733", {"start": v(-59.38, 87.22) * mm, "end": v(-59.86, 87.28) * mm});
            skLineSegment(sketch, "E734", {"start": v(-59.86, 87.28) * mm, "end": v(-61.8, 85.92) * mm});
            skLineSegment(sketch, "E735", {"start": v(-61.8, 85.92) * mm, "end": v(-61.91, 85.44) * mm});
            skLineSegment(sketch, "E736", {"start": v(-61.91, 85.44) * mm, "end": v(-61.88, 84.78) * mm});
            skLineSegment(sketch, "E737", {"start": v(-61.88, 84.78) * mm, "end": v(-61.83, 84.13) * mm});
            skLineSegment(sketch, "E738", {"start": v(-61.83, 84.13) * mm, "end": v(-61.78, 83.49) * mm});
            skLineSegment(sketch, "E739", {"start": v(-61.78, 83.49) * mm, "end": v(-61.73, 82.86) * mm});
            skLineSegment(sketch, "E740", {"start": v(-61.73, 82.86) * mm, "end": v(-61.66, 82.25) * mm});
            skLineSegment(sketch, "E741", {"start": v(-61.66, 82.25) * mm, "end": v(-61.6, 81.65) * mm});
            skLineSegment(sketch, "E742", {"start": v(-61.6, 81.65) * mm, "end": v(-61.52, 81.06) * mm});
            skLineSegment(sketch, "E743", {"start": v(-61.52, 81.06) * mm, "end": v(-61.44, 80.49) * mm});
            skLineSegment(sketch, "E744", {"start": v(-61.44, 80.49) * mm, "end": v(-61.36, 79.92) * mm});
            skLineSegment(sketch, "E745", {"start": v(-61.36, 79.92) * mm, "end": v(-61.27, 79.38) * mm});
            skLineSegment(sketch, "E746", {"start": v(-61.27, 79.38) * mm, "end": v(-61.18, 78.84) * mm});
            skLineSegment(sketch, "E747", {"start": v(-61.18, 78.84) * mm, "end": v(-61.08, 78.32) * mm});
            skLineSegment(sketch, "E748", {"start": v(-61.08, 78.32) * mm, "end": v(-60.98, 77.8) * mm});
            skLineSegment(sketch, "E749", {"start": v(-60.98, 77.8) * mm, "end": v(-60.87, 77.3) * mm});
            skLineSegment(sketch, "E750", {"start": v(-60.87, 77.3) * mm, "end": v(-60.77, 76.82) * mm});
            skLineSegment(sketch, "E751", {"start": v(-60.77, 76.82) * mm, "end": v(-60.65, 76.35) * mm});
            skLineSegment(sketch, "E752", {"start": v(-60.65, 76.35) * mm, "end": v(-60.54, 75.9) * mm});
            skLineSegment(sketch, "E753", {"start": v(-60.54, 75.9) * mm, "end": v(-60.43, 75.44) * mm});
            skLineSegment(sketch, "E754", {"start": v(-60.43, 75.44) * mm, "end": v(-60.3, 75.01) * mm});
            skLineSegment(sketch, "E755", {"start": v(-60.3, 75.01) * mm, "end": v(-60.19, 74.6) * mm});
            skLineSegment(sketch, "E756", {"start": v(-60.19, 74.6) * mm, "end": v(-60.07, 74.18) * mm});
            skLineSegment(sketch, "E757", {"start": v(-60.07, 74.18) * mm, "end": v(-59.95, 73.79) * mm});
            skLineSegment(sketch, "E758", {"start": v(-59.95, 73.79) * mm, "end": v(-59.82, 73.4) * mm});
            skLineSegment(sketch, "E759", {"start": v(-59.82, 73.4) * mm, "end": v(-59.7, 73.04) * mm});
            skLineSegment(sketch, "E760", {"start": v(-59.7, 73.04) * mm, "end": v(-59.58, 72.68) * mm});
            skLineSegment(sketch, "E761", {"start": v(-59.58, 72.68) * mm, "end": v(-59.45, 72.34) * mm});
            skLineSegment(sketch, "E762", {"start": v(-59.45, 72.34) * mm, "end": v(-59.33, 72) * mm});
            skLineSegment(sketch, "E763", {"start": v(-59.33, 72) * mm, "end": v(-59.2, 71.7) * mm});
            skLineSegment(sketch, "E764", {"start": v(-59.2, 71.7) * mm, "end": v(-59.08, 71.39) * mm});
            skLineSegment(sketch, "E765", {"start": v(-59.08, 71.39) * mm, "end": v(-58.96, 71.1) * mm});
            skLineSegment(sketch, "E766", {"start": v(-58.96, 71.1) * mm, "end": v(-58.84, 70.81) * mm});
            skLineSegment(sketch, "E767", {"start": v(-58.84, 70.81) * mm, "end": v(-58.72, 70.54) * mm});
            skLineSegment(sketch, "E768", {"start": v(-58.72, 70.54) * mm, "end": v(-59.1, 70) * mm});
            skLineSegment(sketch, "E769", {"start": v(-59.1, 70) * mm, "end": v(-61.3, 68.08) * mm});
            skLineSegment(sketch, "E770", {"start": v(-61.3, 68.08) * mm, "end": v(-61.89, 67.78) * mm});
            skLineSegment(sketch, "E771", {"start": v(-61.89, 67.78) * mm, "end": v(-62.14, 67.94) * mm});
            skLineSegment(sketch, "E772", {"start": v(-62.14, 67.94) * mm, "end": v(-62.4, 68.1) * mm});
            skLineSegment(sketch, "E773", {"start": v(-62.4, 68.1) * mm, "end": v(-62.67, 68.25) * mm});
            skLineSegment(sketch, "E774", {"start": v(-62.67, 68.25) * mm, "end": v(-62.96, 68.42) * mm});
            skLineSegment(sketch, "E775", {"start": v(-62.96, 68.42) * mm, "end": v(-63.26, 68.58) * mm});
            skLineSegment(sketch, "E776", {"start": v(-63.26, 68.58) * mm, "end": v(-63.57, 68.75) * mm});
            skLineSegment(sketch, "E777", {"start": v(-63.57, 68.75) * mm, "end": v(-63.9, 68.92) * mm});
            skLineSegment(sketch, "E778", {"start": v(-63.9, 68.92) * mm, "end": v(-64.23, 69.1) * mm});
            skLineSegment(sketch, "E779", {"start": v(-64.23, 69.1) * mm, "end": v(-64.58, 69.26) * mm});
            skLineSegment(sketch, "E780", {"start": v(-64.58, 69.26) * mm, "end": v(-64.94, 69.44) * mm});
            skLineSegment(sketch, "E781", {"start": v(-64.94, 69.44) * mm, "end": v(-65.31, 69.61) * mm});
            skLineSegment(sketch, "E782", {"start": v(-65.31, 69.61) * mm, "end": v(-65.7, 69.79) * mm});
            skLineSegment(sketch, "E783", {"start": v(-65.7, 69.79) * mm, "end": v(-66.1, 69.96) * mm});
            skLineSegment(sketch, "E784", {"start": v(-66.1, 69.96) * mm, "end": v(-66.51, 70.14) * mm});
            skLineSegment(sketch, "E785", {"start": v(-66.51, 70.14) * mm, "end": v(-66.94, 70.31) * mm});
            skLineSegment(sketch, "E786", {"start": v(-66.94, 70.31) * mm, "end": v(-67.38, 70.49) * mm});
            skLineSegment(sketch, "E787", {"start": v(-67.38, 70.49) * mm, "end": v(-67.83, 70.66) * mm});
            skLineSegment(sketch, "E788", {"start": v(-67.83, 70.66) * mm, "end": v(-68.3, 70.83) * mm});
            skLineSegment(sketch, "E789", {"start": v(-68.3, 70.83) * mm, "end": v(-68.78, 71) * mm});
            skLineSegment(sketch, "E790", {"start": v(-68.78, 71) * mm, "end": v(-69.27, 71.17) * mm});
            skLineSegment(sketch, "E791", {"start": v(-69.27, 71.17) * mm, "end": v(-69.77, 71.34) * mm});
            skLineSegment(sketch, "E792", {"start": v(-69.77, 71.34) * mm, "end": v(-70.3, 71.5) * mm});
            skLineSegment(sketch, "E793", {"start": v(-70.3, 71.5) * mm, "end": v(-70.82, 71.67) * mm});
            skLineSegment(sketch, "E794", {"start": v(-70.82, 71.67) * mm, "end": v(-71.37, 71.83) * mm});
            skLineSegment(sketch, "E795", {"start": v(-71.37, 71.83) * mm, "end": v(-71.93, 71.99) * mm});
            skLineSegment(sketch, "E796", {"start": v(-71.93, 71.99) * mm, "end": v(-72.5, 72.14) * mm});
            skLineSegment(sketch, "E797", {"start": v(-72.5, 72.14) * mm, "end": v(-73.09, 72.29) * mm});
            skLineSegment(sketch, "E798", {"start": v(-73.09, 72.29) * mm, "end": v(-73.69, 72.44) * mm});
            skLineSegment(sketch, "E799", {"start": v(-73.69, 72.44) * mm, "end": v(-74.3, 72.58) * mm});
            skLineSegment(sketch, "E800", {"start": v(-74.3, 72.58) * mm, "end": v(-74.92, 72.71) * mm});
            skLineSegment(sketch, "E801", {"start": v(-74.92, 72.71) * mm, "end": v(-75.56, 72.84) * mm});
            skLineSegment(sketch, "E802", {"start": v(-75.56, 72.84) * mm, "end": v(-76.22, 72.97) * mm});
            skLineSegment(sketch, "E803", {"start": v(-76.22, 72.97) * mm, "end": v(-76.7, 72.92) * mm});
            skLineSegment(sketch, "E804", {"start": v(-76.7, 72.92) * mm, "end": v(-78.31, 71.2) * mm});
            skLineSegment(sketch, "E805", {"start": v(-78.31, 71.2) * mm, "end": v(-78.32, 70.7) * mm});
            skLineSegment(sketch, "E806", {"start": v(-78.32, 70.7) * mm, "end": v(-78.15, 70.06) * mm});
            skLineSegment(sketch, "E807", {"start": v(-78.15, 70.06) * mm, "end": v(-77.97, 69.43) * mm});
            skLineSegment(sketch, "E808", {"start": v(-77.97, 69.43) * mm, "end": v(-77.8, 68.82) * mm});
            skLineSegment(sketch, "E809", {"start": v(-77.8, 68.82) * mm, "end": v(-77.6, 68.22) * mm});
            skLineSegment(sketch, "E810", {"start": v(-77.6, 68.22) * mm, "end": v(-77.42, 67.63) * mm});
            skLineSegment(sketch, "E811", {"start": v(-77.42, 67.63) * mm, "end": v(-77.22, 67.06) * mm});
            skLineSegment(sketch, "E812", {"start": v(-77.22, 67.06) * mm, "end": v(-77.03, 66.5) * mm});
            skLineSegment(sketch, "E813", {"start": v(-77.03, 66.5) * mm, "end": v(-76.83, 65.95) * mm});
            skLineSegment(sketch, "E814", {"start": v(-76.83, 65.95) * mm, "end": v(-76.63, 65.42) * mm});
            skLineSegment(sketch, "E815", {"start": v(-76.63, 65.42) * mm, "end": v(-76.43, 64.9) * mm});
            skLineSegment(sketch, "E816", {"start": v(-76.43, 64.9) * mm, "end": v(-76.23, 64.4) * mm});
            skLineSegment(sketch, "E817", {"start": v(-76.23, 64.4) * mm, "end": v(-76.03, 63.9) * mm});
            skLineSegment(sketch, "E818", {"start": v(-76.03, 63.9) * mm, "end": v(-75.82, 63.43) * mm});
            skLineSegment(sketch, "E819", {"start": v(-75.82, 63.43) * mm, "end": v(-75.62, 62.96) * mm});
            skLineSegment(sketch, "E820", {"start": v(-75.62, 62.96) * mm, "end": v(-75.4, 62.5) * mm});
            skLineSegment(sketch, "E821", {"start": v(-75.4, 62.5) * mm, "end": v(-75.2, 62.07) * mm});
            skLineSegment(sketch, "E822", {"start": v(-75.2, 62.07) * mm, "end": v(-75, 61.65) * mm});
            skLineSegment(sketch, "E823", {"start": v(-75, 61.65) * mm, "end": v(-74.8, 61.23) * mm});
            skLineSegment(sketch, "E824", {"start": v(-74.8, 61.23) * mm, "end": v(-74.59, 60.83) * mm});
            skLineSegment(sketch, "E825", {"start": v(-74.59, 60.83) * mm, "end": v(-74.38, 60.45) * mm});
            skLineSegment(sketch, "E826", {"start": v(-74.38, 60.45) * mm, "end": v(-74.18, 60.07) * mm});
            skLineSegment(sketch, "E827", {"start": v(-74.18, 60.07) * mm, "end": v(-73.98, 59.71) * mm});
            skLineSegment(sketch, "E828", {"start": v(-73.98, 59.71) * mm, "end": v(-73.78, 59.37) * mm});
            skLineSegment(sketch, "E829", {"start": v(-73.78, 59.37) * mm, "end": v(-73.58, 59.03) * mm});
            skLineSegment(sketch, "E830", {"start": v(-73.58, 59.03) * mm, "end": v(-73.39, 58.7) * mm});
            skLineSegment(sketch, "E831", {"start": v(-73.39, 58.7) * mm, "end": v(-73.2, 58.4) * mm});
            skLineSegment(sketch, "E832", {"start": v(-73.2, 58.4) * mm, "end": v(-73, 58.1) * mm});
            skLineSegment(sketch, "E833", {"start": v(-73, 58.1) * mm, "end": v(-72.82, 57.81) * mm});
            skLineSegment(sketch, "E834", {"start": v(-72.82, 57.81) * mm, "end": v(-72.64, 57.54) * mm});
            skLineSegment(sketch, "E835", {"start": v(-72.64, 57.54) * mm, "end": v(-72.45, 57.28) * mm});
            skLineSegment(sketch, "E836", {"start": v(-72.45, 57.28) * mm, "end": v(-72.28, 57.03) * mm});
            skLineSegment(sketch, "E837", {"start": v(-72.28, 57.03) * mm, "end": v(-72.1, 56.8) * mm});
            skLineSegment(sketch, "E838", {"start": v(-72.1, 56.8) * mm, "end": v(-72.36, 56.18) * mm});
            skLineSegment(sketch, "E839", {"start": v(-72.36, 56.18) * mm, "end": v(-74.12, 53.85) * mm});
            skLineSegment(sketch, "E840", {"start": v(-74.12, 53.85) * mm, "end": v(-74.63, 53.43) * mm});
            skLineSegment(sketch, "E841", {"start": v(-74.63, 53.43) * mm, "end": v(-74.9, 53.53) * mm});
            skLineSegment(sketch, "E842", {"start": v(-74.9, 53.53) * mm, "end": v(-75.2, 53.63) * mm});
            skLineSegment(sketch, "E843", {"start": v(-75.2, 53.63) * mm, "end": v(-75.5, 53.73) * mm});
            skLineSegment(sketch, "E844", {"start": v(-75.5, 53.73) * mm, "end": v(-75.8, 53.83) * mm});
            skLineSegment(sketch, "E845", {"start": v(-75.8, 53.83) * mm, "end": v(-76.14, 53.93) * mm});
            skLineSegment(sketch, "E846", {"start": v(-76.14, 53.93) * mm, "end": v(-76.47, 54.03) * mm});
            skLineSegment(sketch, "E847", {"start": v(-76.47, 54.03) * mm, "end": v(-76.83, 54.13) * mm});
            skLineSegment(sketch, "E848", {"start": v(-76.83, 54.13) * mm, "end": v(-77.19, 54.23) * mm});
            skLineSegment(sketch, "E849", {"start": v(-77.19, 54.23) * mm, "end": v(-77.57, 54.32) * mm});
            skLineSegment(sketch, "E850", {"start": v(-77.57, 54.32) * mm, "end": v(-77.96, 54.42) * mm});
            skLineSegment(sketch, "E851", {"start": v(-77.96, 54.42) * mm, "end": v(-78.36, 54.51) * mm});
            skLineSegment(sketch, "E852", {"start": v(-78.36, 54.51) * mm, "end": v(-78.77, 54.6) * mm});
            skLineSegment(sketch, "E853", {"start": v(-78.77, 54.6) * mm, "end": v(-79.2, 54.7) * mm});
            skLineSegment(sketch, "E854", {"start": v(-79.2, 54.7) * mm, "end": v(-79.64, 54.78) * mm});
            skLineSegment(sketch, "E855", {"start": v(-79.64, 54.78) * mm, "end": v(-80.1, 54.86) * mm});
            skLineSegment(sketch, "E856", {"start": v(-80.1, 54.86) * mm, "end": v(-80.56, 54.94) * mm});
            skLineSegment(sketch, "E857", {"start": v(-80.56, 54.94) * mm, "end": v(-81.04, 55.01) * mm});
            skLineSegment(sketch, "E858", {"start": v(-81.04, 55.01) * mm, "end": v(-81.53, 55.09) * mm});
            skLineSegment(sketch, "E859", {"start": v(-81.53, 55.09) * mm, "end": v(-82.04, 55.15) * mm});
            skLineSegment(sketch, "E860", {"start": v(-82.04, 55.15) * mm, "end": v(-82.55, 55.22) * mm});
            skLineSegment(sketch, "E861", {"start": v(-82.55, 55.22) * mm, "end": v(-83.08, 55.28) * mm});
            skLineSegment(sketch, "E862", {"start": v(-83.08, 55.28) * mm, "end": v(-83.62, 55.33) * mm});
            skLineSegment(sketch, "E863", {"start": v(-83.62, 55.33) * mm, "end": v(-84.18, 55.38) * mm});
            skLineSegment(sketch, "E864", {"start": v(-84.18, 55.38) * mm, "end": v(-84.75, 55.42) * mm});
            skLineSegment(sketch, "E865", {"start": v(-84.75, 55.42) * mm, "end": v(-85.32, 55.46) * mm});
            skLineSegment(sketch, "E866", {"start": v(-85.32, 55.46) * mm, "end": v(-85.92, 55.49) * mm});
            skLineSegment(sketch, "E867", {"start": v(-85.92, 55.49) * mm, "end": v(-86.52, 55.51) * mm});
            skLineSegment(sketch, "E868", {"start": v(-86.52, 55.51) * mm, "end": v(-87.14, 55.53) * mm});
            skLineSegment(sketch, "E869", {"start": v(-87.14, 55.53) * mm, "end": v(-87.76, 55.54) * mm});
            skLineSegment(sketch, "E870", {"start": v(-87.76, 55.54) * mm, "end": v(-88.4, 55.55) * mm});
            skLineSegment(sketch, "E871", {"start": v(-88.4, 55.55) * mm, "end": v(-89.06, 55.54) * mm});
            skLineSegment(sketch, "E872", {"start": v(-89.06, 55.54) * mm, "end": v(-89.72, 55.53) * mm});
            skLineSegment(sketch, "E873", {"start": v(-89.72, 55.53) * mm, "end": v(-90.19, 55.38) * mm});
            skLineSegment(sketch, "E874", {"start": v(-90.19, 55.38) * mm, "end": v(-91.4, 53.35) * mm});
            skLineSegment(sketch, "E875", {"start": v(-91.4, 53.35) * mm, "end": v(-91.31, 52.87) * mm});
            skLineSegment(sketch, "E876", {"start": v(-91.31, 52.87) * mm, "end": v(-91, 52.28) * mm});
            skLineSegment(sketch, "E877", {"start": v(-91, 52.28) * mm, "end": v(-90.7, 51.7) * mm});
            skLineSegment(sketch, "E878", {"start": v(-90.7, 51.7) * mm, "end": v(-90.4, 51.14) * mm});
            skLineSegment(sketch, "E879", {"start": v(-90.4, 51.14) * mm, "end": v(-90.1, 50.6) * mm});
            skLineSegment(sketch, "E880", {"start": v(-90.1, 50.6) * mm, "end": v(-89.79, 50.06) * mm});
            skLineSegment(sketch, "E881", {"start": v(-89.79, 50.06) * mm, "end": v(-89.48, 49.54) * mm});
            skLineSegment(sketch, "E882", {"start": v(-89.48, 49.54) * mm, "end": v(-89.17, 49.03) * mm});
            skLineSegment(sketch, "E883", {"start": v(-89.17, 49.03) * mm, "end": v(-88.87, 48.54) * mm});
            skLineSegment(sketch, "E884", {"start": v(-88.87, 48.54) * mm, "end": v(-88.56, 48.06) * mm});
            skLineSegment(sketch, "E885", {"start": v(-88.56, 48.06) * mm, "end": v(-88.26, 47.6) * mm});
            skLineSegment(sketch, "E886", {"start": v(-88.26, 47.6) * mm, "end": v(-87.95, 47.14) * mm});
            skLineSegment(sketch, "E887", {"start": v(-87.95, 47.14) * mm, "end": v(-87.65, 46.7) * mm});
            skLineSegment(sketch, "E888", {"start": v(-87.65, 46.7) * mm, "end": v(-87.35, 46.28) * mm});
            skLineSegment(sketch, "E889", {"start": v(-87.35, 46.28) * mm, "end": v(-87.05, 45.86) * mm});
            skLineSegment(sketch, "E890", {"start": v(-87.05, 45.86) * mm, "end": v(-86.76, 45.46) * mm});
            skLineSegment(sketch, "E891", {"start": v(-86.76, 45.46) * mm, "end": v(-86.47, 45.08) * mm});
            skLineSegment(sketch, "E892", {"start": v(-86.47, 45.08) * mm, "end": v(-86.18, 44.7) * mm});
            skLineSegment(sketch, "E893", {"start": v(-86.18, 44.7) * mm, "end": v(-85.89, 44.34) * mm});
            skLineSegment(sketch, "E894", {"start": v(-85.89, 44.34) * mm, "end": v(-85.6, 44) * mm});
            skLineSegment(sketch, "E895", {"start": v(-85.6, 44) * mm, "end": v(-85.33, 43.66) * mm});
            skLineSegment(sketch, "E896", {"start": v(-85.33, 43.66) * mm, "end": v(-85.05, 43.34) * mm});
            skLineSegment(sketch, "E897", {"start": v(-85.05, 43.34) * mm, "end": v(-84.78, 43.03) * mm});
            skLineSegment(sketch, "E898", {"start": v(-84.78, 43.03) * mm, "end": v(-84.5, 42.73) * mm});
            skLineSegment(sketch, "E899", {"start": v(-84.5, 42.73) * mm, "end": v(-84.25, 42.44) * mm});
            skLineSegment(sketch, "E900", {"start": v(-84.25, 42.44) * mm, "end": v(-83.99, 42.17) * mm});
            skLineSegment(sketch, "E901", {"start": v(-83.99, 42.17) * mm, "end": v(-83.74, 41.9) * mm});
            skLineSegment(sketch, "E902", {"start": v(-83.74, 41.9) * mm, "end": v(-83.49, 41.65) * mm});
            skLineSegment(sketch, "E903", {"start": v(-83.49, 41.65) * mm, "end": v(-83.25, 41.41) * mm});
            skLineSegment(sketch, "E904", {"start": v(-83.25, 41.41) * mm, "end": v(-83.01, 41.18) * mm});
            skLineSegment(sketch, "E905", {"start": v(-83.01, 41.18) * mm, "end": v(-82.78, 40.96) * mm});
            skLineSegment(sketch, "E906", {"start": v(-82.78, 40.96) * mm, "end": v(-82.56, 40.76) * mm});
            skLineSegment(sketch, "E907", {"start": v(-82.56, 40.76) * mm, "end": v(-82.34, 40.56) * mm});
            skLineSegment(sketch, "E908", {"start": v(-82.34, 40.56) * mm, "end": v(-82.46, 39.91) * mm});
            skLineSegment(sketch, "E909", {"start": v(-82.46, 39.91) * mm, "end": v(-83.7, 37.26) * mm});
            skLineSegment(sketch, "E910", {"start": v(-83.7, 37.26) * mm, "end": v(-84.1, 36.75) * mm});
            skLineSegment(sketch, "E911", {"start": v(-84.1, 36.75) * mm, "end": v(-84.4, 36.79) * mm});
            skLineSegment(sketch, "E912", {"start": v(-84.4, 36.79) * mm, "end": v(-84.7, 36.83) * mm});
            skLineSegment(sketch, "E913", {"start": v(-84.7, 36.83) * mm, "end": v(-85.02, 36.86) * mm});
            skLineSegment(sketch, "E914", {"start": v(-85.02, 36.86) * mm, "end": v(-85.34, 36.9) * mm});
            skLineSegment(sketch, "E915", {"start": v(-85.34, 36.9) * mm, "end": v(-85.69, 36.92) * mm});
            skLineSegment(sketch, "E916", {"start": v(-85.69, 36.92) * mm, "end": v(-86.04, 36.95) * mm});
            skLineSegment(sketch, "E917", {"start": v(-86.04, 36.95) * mm, "end": v(-86.4, 36.97) * mm});
            skLineSegment(sketch, "E918", {"start": v(-86.4, 36.97) * mm, "end": v(-86.78, 37) * mm});
            skLineSegment(sketch, "E919", {"start": v(-86.78, 37) * mm, "end": v(-87.17, 37) * mm});
            skLineSegment(sketch, "E920", {"start": v(-87.17, 37) * mm, "end": v(-87.57, 37.02) * mm});
            skLineSegment(sketch, "E921", {"start": v(-87.57, 37.02) * mm, "end": v(-87.98, 37.03) * mm});
            skLineSegment(sketch, "E922", {"start": v(-87.98, 37.03) * mm, "end": v(-88.4, 37.03) * mm});
            skLineSegment(sketch, "E923", {"start": v(-88.4, 37.03) * mm, "end": v(-88.84, 37.03) * mm});
            skLineSegment(sketch, "E924", {"start": v(-88.84, 37.03) * mm, "end": v(-89.3, 37.02) * mm});
            skLineSegment(sketch, "E925", {"start": v(-89.3, 37.02) * mm, "end": v(-89.75, 37) * mm});
            skLineSegment(sketch, "E926", {"start": v(-89.75, 37) * mm, "end": v(-90.22, 36.99) * mm});
            skLineSegment(sketch, "E927", {"start": v(-90.22, 36.99) * mm, "end": v(-90.7, 36.96) * mm});
            skLineSegment(sketch, "E928", {"start": v(-90.7, 36.96) * mm, "end": v(-91.2, 36.93) * mm});
            skLineSegment(sketch, "E929", {"start": v(-91.2, 36.93) * mm, "end": v(-91.7, 36.9) * mm});
            skLineSegment(sketch, "E930", {"start": v(-91.7, 36.9) * mm, "end": v(-92.23, 36.85) * mm});
            skLineSegment(sketch, "E931", {"start": v(-92.23, 36.85) * mm, "end": v(-92.76, 36.8) * mm});
            skLineSegment(sketch, "E932", {"start": v(-92.76, 36.8) * mm, "end": v(-93.3, 36.73) * mm});
            skLineSegment(sketch, "E933", {"start": v(-93.3, 36.73) * mm, "end": v(-93.85, 36.67) * mm});
            skLineSegment(sketch, "E934", {"start": v(-93.85, 36.67) * mm, "end": v(-94.42, 36.6) * mm});
            skLineSegment(sketch, "E935", {"start": v(-94.42, 36.6) * mm, "end": v(-94.99, 36.5) * mm});
            skLineSegment(sketch, "E936", {"start": v(-94.99, 36.5) * mm, "end": v(-95.58, 36.41) * mm});
            skLineSegment(sketch, "E937", {"start": v(-95.58, 36.41) * mm, "end": v(-96.17, 36.31) * mm});
            skLineSegment(sketch, "E938", {"start": v(-96.17, 36.31) * mm, "end": v(-96.78, 36.2) * mm});
            skLineSegment(sketch, "E939", {"start": v(-96.78, 36.2) * mm, "end": v(-97.4, 36.08) * mm});
            skLineSegment(sketch, "E940", {"start": v(-97.4, 36.08) * mm, "end": v(-98.02, 35.95) * mm});
            skLineSegment(sketch, "E941", {"start": v(-98.02, 35.95) * mm, "end": v(-98.66, 35.81) * mm});
            skLineSegment(sketch, "E942", {"start": v(-98.66, 35.81) * mm, "end": v(-99.3, 35.66) * mm});
            skLineSegment(sketch, "E943", {"start": v(-99.3, 35.66) * mm, "end": v(-99.73, 35.42) * mm});
            skLineSegment(sketch, "E944", {"start": v(-99.73, 35.42) * mm, "end": v(-100.5, 33.18) * mm});
            skLineSegment(sketch, "E945", {"start": v(-100.5, 33.18) * mm, "end": v(-100.31, 32.73) * mm});
            skLineSegment(sketch, "E946", {"start": v(-100.31, 32.73) * mm, "end": v(-99.89, 32.22) * mm});
            skLineSegment(sketch, "E947", {"start": v(-99.89, 32.22) * mm, "end": v(-99.47, 31.72) * mm});
            skLineSegment(sketch, "E948", {"start": v(-99.47, 31.72) * mm, "end": v(-99.06, 31.23) * mm});
            skLineSegment(sketch, "E949", {"start": v(-99.06, 31.23) * mm, "end": v(-98.64, 30.76) * mm});
            skLineSegment(sketch, "E950", {"start": v(-98.64, 30.76) * mm, "end": v(-98.23, 30.3) * mm});
            skLineSegment(sketch, "E951", {"start": v(-98.23, 30.3) * mm, "end": v(-97.82, 29.85) * mm});
            skLineSegment(sketch, "E952", {"start": v(-97.82, 29.85) * mm, "end": v(-97.42, 29.42) * mm});
            skLineSegment(sketch, "E953", {"start": v(-97.42, 29.42) * mm, "end": v(-97.02, 29) * mm});
            skLineSegment(sketch, "E954", {"start": v(-97.02, 29) * mm, "end": v(-96.62, 28.6) * mm});
            skLineSegment(sketch, "E955", {"start": v(-96.62, 28.6) * mm, "end": v(-96.22, 28.2) * mm});
            skLineSegment(sketch, "E956", {"start": v(-96.22, 28.2) * mm, "end": v(-95.83, 27.82) * mm});
            skLineSegment(sketch, "E957", {"start": v(-95.83, 27.82) * mm, "end": v(-95.45, 27.46) * mm});
            skLineSegment(sketch, "E958", {"start": v(-95.45, 27.46) * mm, "end": v(-95.06, 27.1) * mm});
            skLineSegment(sketch, "E959", {"start": v(-95.06, 27.1) * mm, "end": v(-94.69, 26.76) * mm});
            skLineSegment(sketch, "E960", {"start": v(-94.69, 26.76) * mm, "end": v(-94.31, 26.43) * mm});
            skLineSegment(sketch, "E961", {"start": v(-94.31, 26.43) * mm, "end": v(-93.95, 26.12) * mm});
            skLineSegment(sketch, "E962", {"start": v(-93.95, 26.12) * mm, "end": v(-93.59, 25.81) * mm});
            skLineSegment(sketch, "E963", {"start": v(-93.59, 25.81) * mm, "end": v(-93.23, 25.52) * mm});
            skLineSegment(sketch, "E964", {"start": v(-93.23, 25.52) * mm, "end": v(-92.88, 25.24) * mm});
            skLineSegment(sketch, "E965", {"start": v(-92.88, 25.24) * mm, "end": v(-92.54, 24.97) * mm});
            skLineSegment(sketch, "E966", {"start": v(-92.54, 24.97) * mm, "end": v(-92.2, 24.7) * mm});
            skLineSegment(sketch, "E967", {"start": v(-92.2, 24.7) * mm, "end": v(-91.87, 24.46) * mm});
            skLineSegment(sketch, "E968", {"start": v(-91.87, 24.46) * mm, "end": v(-91.55, 24.22) * mm});
            skLineSegment(sketch, "E969", {"start": v(-91.55, 24.22) * mm, "end": v(-91.23, 24) * mm});
            skLineSegment(sketch, "E970", {"start": v(-91.23, 24) * mm, "end": v(-90.92, 23.78) * mm});
            skLineSegment(sketch, "E971", {"start": v(-90.92, 23.78) * mm, "end": v(-90.62, 23.58) * mm});
            skLineSegment(sketch, "E972", {"start": v(-90.62, 23.58) * mm, "end": v(-90.32, 23.38) * mm});
            skLineSegment(sketch, "E973", {"start": v(-90.32, 23.38) * mm, "end": v(-90.04, 23.2) * mm});
            skLineSegment(sketch, "E974", {"start": v(-90.04, 23.2) * mm, "end": v(-89.76, 23.02) * mm});
            skLineSegment(sketch, "E975", {"start": v(-89.76, 23.02) * mm, "end": v(-89.49, 22.86) * mm});
            skLineSegment(sketch, "E976", {"start": v(-89.49, 22.86) * mm, "end": v(-89.23, 22.7) * mm});
            skLineSegment(sketch, "E977", {"start": v(-89.23, 22.7) * mm, "end": v(-88.97, 22.55) * mm});
            skLineSegment(sketch, "E978", {"start": v(-88.97, 22.55) * mm, "end": v(-88.96, 21.9) * mm});
            skLineSegment(sketch, "E979", {"start": v(-88.96, 21.9) * mm, "end": v(-89.6, 19.05) * mm});
            skLineSegment(sketch, "E980", {"start": v(-89.6, 19.05) * mm, "end": v(-89.91, 18.46) * mm});
            skLineSegment(sketch, "E981", {"start": v(-89.91, 18.46) * mm, "end": v(-90.2, 18.44) * mm});
            skLineSegment(sketch, "E982", {"start": v(-90.2, 18.44) * mm, "end": v(-90.5, 18.41) * mm});
            skLineSegment(sketch, "E983", {"start": v(-90.5, 18.41) * mm, "end": v(-90.82, 18.38) * mm});
            skLineSegment(sketch, "E984", {"start": v(-90.82, 18.38) * mm, "end": v(-91.15, 18.34) * mm});
            skLineSegment(sketch, "E985", {"start": v(-91.15, 18.34) * mm, "end": v(-91.49, 18.3) * mm});
            skLineSegment(sketch, "E986", {"start": v(-91.49, 18.3) * mm, "end": v(-91.84, 18.25) * mm});
            skLineSegment(sketch, "E987", {"start": v(-91.84, 18.25) * mm, "end": v(-92.2, 18.2) * mm});
            skLineSegment(sketch, "E988", {"start": v(-92.2, 18.2) * mm, "end": v(-92.57, 18.14) * mm});
            skLineSegment(sketch, "E989", {"start": v(-92.57, 18.14) * mm, "end": v(-92.96, 18.08) * mm});
            skLineSegment(sketch, "E990", {"start": v(-92.96, 18.08) * mm, "end": v(-93.35, 18) * mm});
            skLineSegment(sketch, "E991", {"start": v(-93.35, 18) * mm, "end": v(-93.76, 17.93) * mm});
            skLineSegment(sketch, "E992", {"start": v(-93.76, 17.93) * mm, "end": v(-94.17, 17.84) * mm});
            skLineSegment(sketch, "E993", {"start": v(-94.17, 17.84) * mm, "end": v(-94.6, 17.75) * mm});
            skLineSegment(sketch, "E994", {"start": v(-94.6, 17.75) * mm, "end": v(-95.04, 17.65) * mm});
            skLineSegment(sketch, "E995", {"start": v(-95.04, 17.65) * mm, "end": v(-95.48, 17.54) * mm});
            skLineSegment(sketch, "E996", {"start": v(-95.48, 17.54) * mm, "end": v(-95.94, 17.42) * mm});
            skLineSegment(sketch, "E997", {"start": v(-95.94, 17.42) * mm, "end": v(-96.41, 17.3) * mm});
            skLineSegment(sketch, "E998", {"start": v(-96.41, 17.3) * mm, "end": v(-96.89, 17.16) * mm});
            skLineSegment(sketch, "E999", {"start": v(-96.89, 17.16) * mm, "end": v(-97.38, 17.02) * mm});
            skLineSegment(sketch, "E1000", {"start": v(-97.38, 17.02) * mm, "end": v(-97.87, 16.87) * mm});
            skLineSegment(sketch, "E1001", {"start": v(-97.87, 16.87) * mm, "end": v(-98.38, 16.7) * mm});
            skLineSegment(sketch, "E1002", {"start": v(-98.38, 16.7) * mm, "end": v(-98.9, 16.53) * mm});
            skLineSegment(sketch, "E1003", {"start": v(-98.9, 16.53) * mm, "end": v(-99.43, 16.35) * mm});
            skLineSegment(sketch, "E1004", {"start": v(-99.43, 16.35) * mm, "end": v(-99.96, 16.16) * mm});
            skLineSegment(sketch, "E1005", {"start": v(-99.96, 16.16) * mm, "end": v(-100.5, 15.96) * mm});
            skLineSegment(sketch, "E1006", {"start": v(-100.5, 15.96) * mm, "end": v(-101.06, 15.75) * mm});
            skLineSegment(sketch, "E1007", {"start": v(-101.06, 15.75) * mm, "end": v(-101.62, 15.52) * mm});
            skLineSegment(sketch, "E1008", {"start": v(-101.62, 15.52) * mm, "end": v(-102.19, 15.29) * mm});
            skLineSegment(sketch, "E1009", {"start": v(-102.19, 15.29) * mm, "end": v(-102.77, 15.04) * mm});
            skLineSegment(sketch, "E1010", {"start": v(-102.77, 15.04) * mm, "end": v(-103.35, 14.79) * mm});
            skLineSegment(sketch, "E1011", {"start": v(-103.35, 14.79) * mm, "end": v(-103.95, 14.52) * mm});
            skLineSegment(sketch, "E1012", {"start": v(-103.95, 14.52) * mm, "end": v(-104.55, 14.24) * mm});
            skLineSegment(sketch, "E1013", {"start": v(-104.55, 14.24) * mm, "end": v(-104.92, 13.91) * mm});
            skLineSegment(sketch, "E1014", {"start": v(-104.92, 13.91) * mm, "end": v(-105.2, 11.56) * mm});
            skLineSegment(sketch, "E1015", {"start": v(-105.2, 11.56) * mm, "end": v(-104.92, 11.16) * mm});
            skLineSegment(sketch, "E1016", {"start": v(-104.92, 11.16) * mm, "end": v(-104.4, 10.75) * mm});
            skLineSegment(sketch, "E1017", {"start": v(-104.4, 10.75) * mm, "end": v(-103.9, 10.34) * mm});
            skLineSegment(sketch, "E1018", {"start": v(-103.9, 10.34) * mm, "end": v(-103.38, 9.95) * mm});
            skLineSegment(sketch, "E1019", {"start": v(-103.38, 9.95) * mm, "end": v(-102.88, 9.58) * mm});
            skLineSegment(sketch, "E1020", {"start": v(-102.88, 9.58) * mm, "end": v(-102.38, 9.21) * mm});
            skLineSegment(sketch, "E1021", {"start": v(-102.38, 9.21) * mm, "end": v(-101.9, 8.86) * mm});
            skLineSegment(sketch, "E1022", {"start": v(-101.9, 8.86) * mm, "end": v(-101.4, 8.52) * mm});
            skLineSegment(sketch, "E1023", {"start": v(-101.4, 8.52) * mm, "end": v(-100.93, 8.2) * mm});
            skLineSegment(sketch, "E1024", {"start": v(-100.93, 8.2) * mm, "end": v(-100.45, 7.88) * mm});
            skLineSegment(sketch, "E1025", {"start": v(-100.45, 7.88) * mm, "end": v(-99.98, 7.58) * mm});
            skLineSegment(sketch, "E1026", {"start": v(-99.98, 7.58) * mm, "end": v(-99.52, 7.3) * mm});
            skLineSegment(sketch, "E1027", {"start": v(-99.52, 7.3) * mm, "end": v(-99.07, 7.01) * mm});
            skLineSegment(sketch, "E1028", {"start": v(-99.07, 7.01) * mm, "end": v(-98.62, 6.75) * mm});
            skLineSegment(sketch, "E1029", {"start": v(-98.62, 6.75) * mm, "end": v(-98.18, 6.5) * mm});
            skLineSegment(sketch, "E1030", {"start": v(-98.18, 6.5) * mm, "end": v(-97.75, 6.25) * mm});
            skLineSegment(sketch, "E1031", {"start": v(-97.75, 6.25) * mm, "end": v(-97.33, 6.01) * mm});
            skLineSegment(sketch, "E1032", {"start": v(-97.33, 6.01) * mm, "end": v(-96.9, 5.79) * mm});
            skLineSegment(sketch, "E1033", {"start": v(-96.9, 5.79) * mm, "end": v(-96.5, 5.58) * mm});
            skLineSegment(sketch, "E1034", {"start": v(-96.5, 5.58) * mm, "end": v(-96.1, 5.37) * mm});
            skLineSegment(sketch, "E1035", {"start": v(-96.1, 5.37) * mm, "end": v(-95.7, 5.18) * mm});
            skLineSegment(sketch, "E1036", {"start": v(-95.7, 5.18) * mm, "end": v(-95.32, 5) * mm});
            skLineSegment(sketch, "E1037", {"start": v(-95.32, 5) * mm, "end": v(-94.95, 4.83) * mm});
            skLineSegment(sketch, "E1038", {"start": v(-94.95, 4.83) * mm, "end": v(-94.58, 4.66) * mm});
            skLineSegment(sketch, "E1039", {"start": v(-94.58, 4.66) * mm, "end": v(-94.23, 4.5) * mm});
            skLineSegment(sketch, "E1040", {"start": v(-94.23, 4.5) * mm, "end": v(-93.88, 4.36) * mm});
            skLineSegment(sketch, "E1041", {"start": v(-93.88, 4.36) * mm, "end": v(-93.54, 4.22) * mm});
            skLineSegment(sketch, "E1042", {"start": v(-93.54, 4.22) * mm, "end": v(-93.21, 4.1) * mm});
            skLineSegment(sketch, "E1043", {"start": v(-93.21, 4.1) * mm, "end": v(-92.9, 3.97) * mm});
            skLineSegment(sketch, "E1044", {"start": v(-92.9, 3.97) * mm, "end": v(-92.58, 3.86) * mm});
            skLineSegment(sketch, "E1045", {"start": v(-92.58, 3.86) * mm, "end": v(-92.29, 3.75) * mm});
            skLineSegment(sketch, "E1046", {"start": v(-92.29, 3.75) * mm, "end": v(-92, 3.65) * mm});
            skLineSegment(sketch, "E1047", {"start": v(-92, 3.65) * mm, "end": v(-91.72, 3.56) * mm});
            skLineSegment(sketch, "E1048", {"start": v(-91.72, 3.56) * mm, "end": v(-91.57, 2.92) * mm});
            skLineSegment(sketch, "E1049", {"start": v(-91.57, 2.92) * mm, "end": v(-91.61, 0) * mm});
            skLineSegment(sketch, "E1050", {"start": v(-91.61, 0) * mm, "end": v(-91.78, -0.64) * mm});
            skLineSegment(sketch, "E1051", {"start": v(-91.78, -0.64) * mm, "end": v(-92.07, -0.72) * mm});
            skLineSegment(sketch, "E1052", {"start": v(-92.07, -0.72) * mm, "end": v(-92.36, -0.8) * mm});
            skLineSegment(sketch, "E1053", {"start": v(-92.36, -0.8) * mm, "end": v(-92.66, -0.9) * mm});
            skLineSegment(sketch, "E1054", {"start": v(-92.66, -0.9) * mm, "end": v(-92.97, -1) * mm});
            skLineSegment(sketch, "E1055", {"start": v(-92.97, -1) * mm, "end": v(-93.3, -1.12) * mm});
            skLineSegment(sketch, "E1056", {"start": v(-93.3, -1.12) * mm, "end": v(-93.63, -1.24) * mm});
            skLineSegment(sketch, "E1057", {"start": v(-93.63, -1.24) * mm, "end": v(-93.97, -1.37) * mm});
            skLineSegment(sketch, "E1058", {"start": v(-93.97, -1.37) * mm, "end": v(-94.32, -1.5) * mm});
            skLineSegment(sketch, "E1059", {"start": v(-94.32, -1.5) * mm, "end": v(-94.68, -1.64) * mm});
            skLineSegment(sketch, "E1060", {"start": v(-94.68, -1.64) * mm, "end": v(-95.05, -1.8) * mm});
            skLineSegment(sketch, "E1061", {"start": v(-95.05, -1.8) * mm, "end": v(-95.43, -1.96) * mm});
            skLineSegment(sketch, "E1062", {"start": v(-95.43, -1.96) * mm, "end": v(-95.82, -2.13) * mm});
            skLineSegment(sketch, "E1063", {"start": v(-95.82, -2.13) * mm, "end": v(-96.22, -2.3) * mm});
            skLineSegment(sketch, "E1064", {"start": v(-96.22, -2.3) * mm, "end": v(-96.63, -2.5) * mm});
            skLineSegment(sketch, "E1065", {"start": v(-96.63, -2.5) * mm, "end": v(-97.04, -2.7) * mm});
            skLineSegment(sketch, "E1066", {"start": v(-97.04, -2.7) * mm, "end": v(-97.47, -2.9) * mm});
            skLineSegment(sketch, "E1067", {"start": v(-97.47, -2.9) * mm, "end": v(-97.9, -3.13) * mm});
            skLineSegment(sketch, "E1068", {"start": v(-97.9, -3.13) * mm, "end": v(-98.34, -3.36) * mm});
            skLineSegment(sketch, "E1069", {"start": v(-98.34, -3.36) * mm, "end": v(-98.79, -3.6) * mm});
            skLineSegment(sketch, "E1070", {"start": v(-98.79, -3.6) * mm, "end": v(-99.24, -3.85) * mm});
            skLineSegment(sketch, "E1071", {"start": v(-99.24, -3.85) * mm, "end": v(-99.7, -4.11) * mm});
            skLineSegment(sketch, "E1072", {"start": v(-99.7, -4.11) * mm, "end": v(-100.18, -4.4) * mm});
            skLineSegment(sketch, "E1073", {"start": v(-100.18, -4.4) * mm, "end": v(-100.65, -4.68) * mm});
            skLineSegment(sketch, "E1074", {"start": v(-100.65, -4.68) * mm, "end": v(-101.14, -4.97) * mm});
            skLineSegment(sketch, "E1075", {"start": v(-101.14, -4.97) * mm, "end": v(-101.63, -5.29) * mm});
            skLineSegment(sketch, "E1076", {"start": v(-101.63, -5.29) * mm, "end": v(-102.12, -5.6) * mm});
            skLineSegment(sketch, "E1077", {"start": v(-102.12, -5.6) * mm, "end": v(-102.63, -5.94) * mm});
            skLineSegment(sketch, "E1078", {"start": v(-102.63, -5.94) * mm, "end": v(-103.14, -6.3) * mm});
            skLineSegment(sketch, "E1079", {"start": v(-103.14, -6.3) * mm, "end": v(-103.65, -6.65) * mm});
            skLineSegment(sketch, "E1080", {"start": v(-103.65, -6.65) * mm, "end": v(-104.17, -7.03) * mm});
            skLineSegment(sketch, "E1081", {"start": v(-104.17, -7.03) * mm, "end": v(-104.7, -7.41) * mm});
            skLineSegment(sketch, "E1082", {"start": v(-104.7, -7.41) * mm, "end": v(-105.23, -7.81) * mm});
            skLineSegment(sketch, "E1083", {"start": v(-105.23, -7.81) * mm, "end": v(-105.52, -8.2) * mm});
            skLineSegment(sketch, "E1084", {"start": v(-105.52, -8.2) * mm, "end": v(-105.3, -10.56) * mm});
            skLineSegment(sketch, "E1085", {"start": v(-105.3, -10.56) * mm, "end": v(-104.95, -10.9) * mm});
            skLineSegment(sketch, "E1086", {"start": v(-104.95, -10.9) * mm, "end": v(-104.36, -11.2) * mm});
            skLineSegment(sketch, "E1087", {"start": v(-104.36, -11.2) * mm, "end": v(-103.77, -11.48) * mm});
            skLineSegment(sketch, "E1088", {"start": v(-103.77, -11.48) * mm, "end": v(-103.2, -11.76) * mm});
            skLineSegment(sketch, "E1089", {"start": v(-103.2, -11.76) * mm, "end": v(-102.63, -12.02) * mm});
            skLineSegment(sketch, "E1090", {"start": v(-102.63, -12.02) * mm, "end": v(-102.06, -12.28) * mm});
            skLineSegment(sketch, "E1091", {"start": v(-102.06, -12.28) * mm, "end": v(-101.5, -12.52) * mm});
            skLineSegment(sketch, "E1092", {"start": v(-101.5, -12.52) * mm, "end": v(-100.96, -12.75) * mm});
            skLineSegment(sketch, "E1093", {"start": v(-100.96, -12.75) * mm, "end": v(-100.42, -12.97) * mm});
            skLineSegment(sketch, "E1094", {"start": v(-100.42, -12.97) * mm, "end": v(-99.9, -13.17) * mm});
            skLineSegment(sketch, "E1095", {"start": v(-99.9, -13.17) * mm, "end": v(-99.38, -13.37) * mm});
            skLineSegment(sketch, "E1096", {"start": v(-99.38, -13.37) * mm, "end": v(-98.86, -13.56) * mm});
            skLineSegment(sketch, "E1097", {"start": v(-98.86, -13.56) * mm, "end": v(-98.36, -13.74) * mm});
            skLineSegment(sketch, "E1098", {"start": v(-98.36, -13.74) * mm, "end": v(-97.87, -13.9) * mm});
            skLineSegment(sketch, "E1099", {"start": v(-97.87, -13.9) * mm, "end": v(-97.39, -14.06) * mm});
            skLineSegment(sketch, "E1100", {"start": v(-97.39, -14.06) * mm, "end": v(-96.91, -14.21) * mm});
            skLineSegment(sketch, "E1101", {"start": v(-96.91, -14.21) * mm, "end": v(-96.45, -14.35) * mm});
            skLineSegment(sketch, "E1102", {"start": v(-96.45, -14.35) * mm, "end": v(-96, -14.49) * mm});
            skLineSegment(sketch, "E1103", {"start": v(-96, -14.49) * mm, "end": v(-95.55, -14.6) * mm});
            skLineSegment(sketch, "E1104", {"start": v(-95.55, -14.6) * mm, "end": v(-95.12, -14.72) * mm});
            skLineSegment(sketch, "E1105", {"start": v(-95.12, -14.72) * mm, "end": v(-94.7, -14.83) * mm});
            skLineSegment(sketch, "E1106", {"start": v(-94.7, -14.83) * mm, "end": v(-94.28, -14.93) * mm});
            skLineSegment(sketch, "E1107", {"start": v(-94.28, -14.93) * mm, "end": v(-93.88, -15.02) * mm});
            skLineSegment(sketch, "E1108", {"start": v(-93.88, -15.02) * mm, "end": v(-93.48, -15.1) * mm});
            skLineSegment(sketch, "E1109", {"start": v(-93.48, -15.1) * mm, "end": v(-93.1, -15.18) * mm});
            skLineSegment(sketch, "E1110", {"start": v(-93.1, -15.18) * mm, "end": v(-92.73, -15.25) * mm});
            skLineSegment(sketch, "E1111", {"start": v(-92.73, -15.25) * mm, "end": v(-92.37, -15.32) * mm});
            skLineSegment(sketch, "E1112", {"start": v(-92.37, -15.32) * mm, "end": v(-92.03, -15.38) * mm});
            skLineSegment(sketch, "E1113", {"start": v(-92.03, -15.38) * mm, "end": v(-91.69, -15.43) * mm});
            skLineSegment(sketch, "E1114", {"start": v(-91.69, -15.43) * mm, "end": v(-91.36, -15.48) * mm});
            skLineSegment(sketch, "E1115", {"start": v(-91.36, -15.48) * mm, "end": v(-91.05, -15.52) * mm});
            skLineSegment(sketch, "E1116", {"start": v(-91.05, -15.52) * mm, "end": v(-90.75, -15.55) * mm});
            skLineSegment(sketch, "E1117", {"start": v(-90.75, -15.55) * mm, "end": v(-90.45, -15.58) * mm});
            skLineSegment(sketch, "E1118", {"start": v(-90.45, -15.58) * mm, "end": v(-90.17, -16.18) * mm});
            skLineSegment(sketch, "E1119", {"start": v(-90.17, -16.18) * mm, "end": v(-89.6, -19.05) * mm});
            skLineSegment(sketch, "E1120", {"start": v(-89.6, -19.05) * mm, "end": v(-89.65, -19.7) * mm});
            skLineSegment(sketch, "E1121", {"start": v(-89.65, -19.7) * mm, "end": v(-89.9, -19.85) * mm});
            skLineSegment(sketch, "E1122", {"start": v(-89.9, -19.85) * mm, "end": v(-90.17, -20) * mm});
            skLineSegment(sketch, "E1123", {"start": v(-90.17, -20) * mm, "end": v(-90.45, -20.15) * mm});
            skLineSegment(sketch, "E1124", {"start": v(-90.45, -20.15) * mm, "end": v(-90.73, -20.32) * mm});
            skLineSegment(sketch, "E1125", {"start": v(-90.73, -20.32) * mm, "end": v(-91.02, -20.5) * mm});
            skLineSegment(sketch, "E1126", {"start": v(-91.02, -20.5) * mm, "end": v(-91.32, -20.68) * mm});
            skLineSegment(sketch, "E1127", {"start": v(-91.32, -20.68) * mm, "end": v(-91.63, -20.87) * mm});
            skLineSegment(sketch, "E1128", {"start": v(-91.63, -20.87) * mm, "end": v(-91.95, -21.08) * mm});
            skLineSegment(sketch, "E1129", {"start": v(-91.95, -21.08) * mm, "end": v(-92.27, -21.3) * mm});
            skLineSegment(sketch, "E1130", {"start": v(-92.27, -21.3) * mm, "end": v(-92.6, -21.52) * mm});
            skLineSegment(sketch, "E1131", {"start": v(-92.6, -21.52) * mm, "end": v(-92.94, -21.76) * mm});
            skLineSegment(sketch, "E1132", {"start": v(-92.94, -21.76) * mm, "end": v(-93.29, -22) * mm});
            skLineSegment(sketch, "E1133", {"start": v(-93.29, -22) * mm, "end": v(-93.64, -22.26) * mm});
            skLineSegment(sketch, "E1134", {"start": v(-93.64, -22.26) * mm, "end": v(-94, -22.53) * mm});
            skLineSegment(sketch, "E1135", {"start": v(-94, -22.53) * mm, "end": v(-94.36, -22.81) * mm});
            skLineSegment(sketch, "E1136", {"start": v(-94.36, -22.81) * mm, "end": v(-94.73, -23.1) * mm});
            skLineSegment(sketch, "E1137", {"start": v(-94.73, -23.1) * mm, "end": v(-95.1, -23.41) * mm});
            skLineSegment(sketch, "E1138", {"start": v(-95.1, -23.41) * mm, "end": v(-95.5, -23.73) * mm});
            skLineSegment(sketch, "E1139", {"start": v(-95.5, -23.73) * mm, "end": v(-95.88, -24.06) * mm});
            skLineSegment(sketch, "E1140", {"start": v(-95.88, -24.06) * mm, "end": v(-96.27, -24.4) * mm});
            skLineSegment(sketch, "E1141", {"start": v(-96.27, -24.4) * mm, "end": v(-96.67, -24.76) * mm});
            skLineSegment(sketch, "E1142", {"start": v(-96.67, -24.76) * mm, "end": v(-97.07, -25.12) * mm});
            skLineSegment(sketch, "E1143", {"start": v(-97.07, -25.12) * mm, "end": v(-97.48, -25.5) * mm});
            skLineSegment(sketch, "E1144", {"start": v(-97.48, -25.5) * mm, "end": v(-97.9, -25.9) * mm});
            skLineSegment(sketch, "E1145", {"start": v(-97.9, -25.9) * mm, "end": v(-98.3, -26.3) * mm});
            skLineSegment(sketch, "E1146", {"start": v(-98.3, -26.3) * mm, "end": v(-98.73, -26.72) * mm});
            skLineSegment(sketch, "E1147", {"start": v(-98.73, -26.72) * mm, "end": v(-99.15, -27.15) * mm});
            skLineSegment(sketch, "E1148", {"start": v(-99.15, -27.15) * mm, "end": v(-99.57, -27.6) * mm});
            skLineSegment(sketch, "E1149", {"start": v(-99.57, -27.6) * mm, "end": v(-100, -28.06) * mm});
            skLineSegment(sketch, "E1150", {"start": v(-100, -28.06) * mm, "end": v(-100.43, -28.53) * mm});
            skLineSegment(sketch, "E1151", {"start": v(-100.43, -28.53) * mm, "end": v(-100.87, -29.02) * mm});
            skLineSegment(sketch, "E1152", {"start": v(-100.87, -29.02) * mm, "end": v(-101.3, -29.52) * mm});
            skLineSegment(sketch, "E1153", {"start": v(-101.3, -29.52) * mm, "end": v(-101.5, -29.96) * mm});
            skLineSegment(sketch, "E1154", {"start": v(-101.5, -29.96) * mm, "end": v(-100.8, -32.22) * mm});
            skLineSegment(sketch, "E1155", {"start": v(-100.8, -32.22) * mm, "end": v(-100.4, -32.48) * mm});
            skLineSegment(sketch, "E1156", {"start": v(-100.4, -32.48) * mm, "end": v(-99.75, -32.65) * mm});
            skLineSegment(sketch, "E1157", {"start": v(-99.75, -32.65) * mm, "end": v(-99.12, -32.8) * mm});
            skLineSegment(sketch, "E1158", {"start": v(-99.12, -32.8) * mm, "end": v(-98.5, -32.96) * mm});
            skLineSegment(sketch, "E1159", {"start": v(-98.5, -32.96) * mm, "end": v(-97.88, -33.1) * mm});
            skLineSegment(sketch, "E1160", {"start": v(-97.88, -33.1) * mm, "end": v(-97.28, -33.23) * mm});
            skLineSegment(sketch, "E1161", {"start": v(-97.28, -33.23) * mm, "end": v(-96.69, -33.35) * mm});
            skLineSegment(sketch, "E1162", {"start": v(-96.69, -33.35) * mm, "end": v(-96.1, -33.46) * mm});
            skLineSegment(sketch, "E1163", {"start": v(-96.1, -33.46) * mm, "end": v(-95.53, -33.56) * mm});
            skLineSegment(sketch, "E1164", {"start": v(-95.53, -33.56) * mm, "end": v(-94.97, -33.66) * mm});
            skLineSegment(sketch, "E1165", {"start": v(-94.97, -33.66) * mm, "end": v(-94.42, -33.74) * mm});
            skLineSegment(sketch, "E1166", {"start": v(-94.42, -33.74) * mm, "end": v(-93.88, -33.82) * mm});
            skLineSegment(sketch, "E1167", {"start": v(-93.88, -33.82) * mm, "end": v(-93.36, -33.89) * mm});
            skLineSegment(sketch, "E1168", {"start": v(-93.36, -33.89) * mm, "end": v(-92.84, -33.95) * mm});
            skLineSegment(sketch, "E1169", {"start": v(-92.84, -33.95) * mm, "end": v(-92.33, -34) * mm});
            skLineSegment(sketch, "E1170", {"start": v(-92.33, -34) * mm, "end": v(-91.84, -34.05) * mm});
            skLineSegment(sketch, "E1171", {"start": v(-91.84, -34.05) * mm, "end": v(-91.36, -34.1) * mm});
            skLineSegment(sketch, "E1172", {"start": v(-91.36, -34.1) * mm, "end": v(-90.88, -34.13) * mm});
            skLineSegment(sketch, "E1173", {"start": v(-90.88, -34.13) * mm, "end": v(-90.43, -34.15) * mm});
            skLineSegment(sketch, "E1174", {"start": v(-90.43, -34.15) * mm, "end": v(-89.98, -34.18) * mm});
            skLineSegment(sketch, "E1175", {"start": v(-89.98, -34.18) * mm, "end": v(-89.54, -34.2) * mm});
            skLineSegment(sketch, "E1176", {"start": v(-89.54, -34.2) * mm, "end": v(-89.12, -34.2) * mm});
            skLineSegment(sketch, "E1177", {"start": v(-89.12, -34.2) * mm, "end": v(-88.7, -34.21) * mm});
            skLineSegment(sketch, "E1178", {"start": v(-88.7, -34.21) * mm, "end": v(-88.3, -34.21) * mm});
            skLineSegment(sketch, "E1179", {"start": v(-88.3, -34.21) * mm, "end": v(-87.91, -34.2) * mm});
            skLineSegment(sketch, "E1180", {"start": v(-87.91, -34.2) * mm, "end": v(-87.54, -34.2) * mm});
            skLineSegment(sketch, "E1181", {"start": v(-87.54, -34.2) * mm, "end": v(-87.17, -34.19) * mm});
            skLineSegment(sketch, "E1182", {"start": v(-87.17, -34.19) * mm, "end": v(-86.82, -34.17) * mm});
            skLineSegment(sketch, "E1183", {"start": v(-86.82, -34.17) * mm, "end": v(-86.48, -34.15) * mm});
            skLineSegment(sketch, "E1184", {"start": v(-86.48, -34.15) * mm, "end": v(-86.15, -34.13) * mm});
            skLineSegment(sketch, "E1185", {"start": v(-86.15, -34.13) * mm, "end": v(-85.83, -34.1) * mm});
            skLineSegment(sketch, "E1186", {"start": v(-85.83, -34.1) * mm, "end": v(-85.53, -34.08) * mm});
            skLineSegment(sketch, "E1187", {"start": v(-85.53, -34.08) * mm, "end": v(-85.24, -34.05) * mm});
            skLineSegment(sketch, "E1188", {"start": v(-85.24, -34.05) * mm, "end": v(-84.84, -34.58) * mm});
            skLineSegment(sketch, "E1189", {"start": v(-84.84, -34.58) * mm, "end": v(-83.7, -37.26) * mm});
            skLineSegment(sketch, "E1190", {"start": v(-83.7, -37.26) * mm, "end": v(-83.6, -37.91) * mm});
            skLineSegment(sketch, "E1191", {"start": v(-83.6, -37.91) * mm, "end": v(-83.81, -38.1) * mm});
            skLineSegment(sketch, "E1192", {"start": v(-83.81, -38.1) * mm, "end": v(-84.04, -38.3) * mm});
            skLineSegment(sketch, "E1193", {"start": v(-84.04, -38.3) * mm, "end": v(-84.28, -38.51) * mm});
            skLineSegment(sketch, "E1194", {"start": v(-84.28, -38.51) * mm, "end": v(-84.52, -38.74) * mm});
            skLineSegment(sketch, "E1195", {"start": v(-84.52, -38.74) * mm, "end": v(-84.77, -38.97) * mm});
            skLineSegment(sketch, "E1196", {"start": v(-84.77, -38.97) * mm, "end": v(-85.03, -39.21) * mm});
            skLineSegment(sketch, "E1197", {"start": v(-85.03, -39.21) * mm, "end": v(-85.3, -39.47) * mm});
            skLineSegment(sketch, "E1198", {"start": v(-85.3, -39.47) * mm, "end": v(-85.56, -39.73) * mm});
            skLineSegment(sketch, "E1199", {"start": v(-85.56, -39.73) * mm, "end": v(-85.83, -40.01) * mm});
            skLineSegment(sketch, "E1200", {"start": v(-85.83, -40.01) * mm, "end": v(-86.1, -40.3) * mm});
            skLineSegment(sketch, "E1201", {"start": v(-86.1, -40.3) * mm, "end": v(-86.39, -40.6) * mm});
            skLineSegment(sketch, "E1202", {"start": v(-86.39, -40.6) * mm, "end": v(-86.67, -40.92) * mm});
            skLineSegment(sketch, "E1203", {"start": v(-86.67, -40.92) * mm, "end": v(-86.96, -41.24) * mm});
            skLineSegment(sketch, "E1204", {"start": v(-86.96, -41.24) * mm, "end": v(-87.26, -41.58) * mm});
            skLineSegment(sketch, "E1205", {"start": v(-87.26, -41.58) * mm, "end": v(-87.56, -41.94) * mm});
            skLineSegment(sketch, "E1206", {"start": v(-87.56, -41.94) * mm, "end": v(-87.86, -42.3) * mm});
            skLineSegment(sketch, "E1207", {"start": v(-87.86, -42.3) * mm, "end": v(-88.16, -42.68) * mm});
            skLineSegment(sketch, "E1208", {"start": v(-88.16, -42.68) * mm, "end": v(-88.47, -43.07) * mm});
            skLineSegment(sketch, "E1209", {"start": v(-88.47, -43.07) * mm, "end": v(-88.78, -43.47) * mm});
            skLineSegment(sketch, "E1210", {"start": v(-88.78, -43.47) * mm, "end": v(-89.1, -43.88) * mm});
            skLineSegment(sketch, "E1211", {"start": v(-89.1, -43.88) * mm, "end": v(-89.41, -44.31) * mm});
            skLineSegment(sketch, "E1212", {"start": v(-89.41, -44.31) * mm, "end": v(-89.73, -44.76) * mm});
            skLineSegment(sketch, "E1213", {"start": v(-89.73, -44.76) * mm, "end": v(-90.05, -45.21) * mm});
            skLineSegment(sketch, "E1214", {"start": v(-90.05, -45.21) * mm, "end": v(-90.37, -45.68) * mm});
            skLineSegment(sketch, "E1215", {"start": v(-90.37, -45.68) * mm, "end": v(-90.7, -46.16) * mm});
            skLineSegment(sketch, "E1216", {"start": v(-90.7, -46.16) * mm, "end": v(-91.01, -46.66) * mm});
            skLineSegment(sketch, "E1217", {"start": v(-91.01, -46.66) * mm, "end": v(-91.34, -47.17) * mm});
            skLineSegment(sketch, "E1218", {"start": v(-91.34, -47.17) * mm, "end": v(-91.66, -47.7) * mm});
            skLineSegment(sketch, "E1219", {"start": v(-91.66, -47.7) * mm, "end": v(-91.98, -48.24) * mm});
            skLineSegment(sketch, "E1220", {"start": v(-91.98, -48.24) * mm, "end": v(-92.3, -48.79) * mm});
            skLineSegment(sketch, "E1221", {"start": v(-92.3, -48.79) * mm, "end": v(-92.63, -49.35) * mm});
            skLineSegment(sketch, "E1222", {"start": v(-92.63, -49.35) * mm, "end": v(-92.95, -49.93) * mm});
            skLineSegment(sketch, "E1223", {"start": v(-92.95, -49.93) * mm, "end": v(-93.05, -50.41) * mm});
            skLineSegment(sketch, "E1224", {"start": v(-93.05, -50.41) * mm, "end": v(-91.9, -52.48) * mm});
            skLineSegment(sketch, "E1225", {"start": v(-91.9, -52.48) * mm, "end": v(-91.45, -52.64) * mm});
            skLineSegment(sketch, "E1226", {"start": v(-91.45, -52.64) * mm, "end": v(-90.78, -52.68) * mm});
            skLineSegment(sketch, "E1227", {"start": v(-90.78, -52.68) * mm, "end": v(-90.13, -52.7) * mm});
            skLineSegment(sketch, "E1228", {"start": v(-90.13, -52.7) * mm, "end": v(-89.49, -52.72) * mm});
            skLineSegment(sketch, "E1229", {"start": v(-89.49, -52.72) * mm, "end": v(-88.86, -52.72) * mm});
            skLineSegment(sketch, "E1230", {"start": v(-88.86, -52.72) * mm, "end": v(-88.25, -52.73) * mm});
            skLineSegment(sketch, "E1231", {"start": v(-88.25, -52.73) * mm, "end": v(-87.64, -52.72) * mm});
            skLineSegment(sketch, "E1232", {"start": v(-87.64, -52.72) * mm, "end": v(-87.05, -52.71) * mm});
            skLineSegment(sketch, "E1233", {"start": v(-87.05, -52.71) * mm, "end": v(-86.47, -52.7) * mm});
            skLineSegment(sketch, "E1234", {"start": v(-86.47, -52.7) * mm, "end": v(-85.9, -52.67) * mm});
            skLineSegment(sketch, "E1235", {"start": v(-85.9, -52.67) * mm, "end": v(-85.34, -52.64) * mm});
            skLineSegment(sketch, "E1236", {"start": v(-85.34, -52.64) * mm, "end": v(-84.8, -52.6) * mm});
            skLineSegment(sketch, "E1237", {"start": v(-84.8, -52.6) * mm, "end": v(-84.27, -52.56) * mm});
            skLineSegment(sketch, "E1238", {"start": v(-84.27, -52.56) * mm, "end": v(-83.75, -52.51) * mm});
            skLineSegment(sketch, "E1239", {"start": v(-83.75, -52.51) * mm, "end": v(-83.25, -52.46) * mm});
            skLineSegment(sketch, "E1240", {"start": v(-83.25, -52.46) * mm, "end": v(-82.75, -52.4) * mm});
            skLineSegment(sketch, "E1241", {"start": v(-82.75, -52.4) * mm, "end": v(-82.27, -52.34) * mm});
            skLineSegment(sketch, "E1242", {"start": v(-82.27, -52.34) * mm, "end": v(-81.8, -52.28) * mm});
            skLineSegment(sketch, "E1243", {"start": v(-81.8, -52.28) * mm, "end": v(-81.35, -52.2) * mm});
            skLineSegment(sketch, "E1244", {"start": v(-81.35, -52.2) * mm, "end": v(-80.9, -52.14) * mm});
            skLineSegment(sketch, "E1245", {"start": v(-80.9, -52.14) * mm, "end": v(-80.47, -52.06) * mm});
            skLineSegment(sketch, "E1246", {"start": v(-80.47, -52.06) * mm, "end": v(-80.06, -51.99) * mm});
            skLineSegment(sketch, "E1247", {"start": v(-80.06, -51.99) * mm, "end": v(-79.65, -51.9) * mm});
            skLineSegment(sketch, "E1248", {"start": v(-79.65, -51.9) * mm, "end": v(-79.26, -51.82) * mm});
            skLineSegment(sketch, "E1249", {"start": v(-79.26, -51.82) * mm, "end": v(-78.88, -51.74) * mm});
            skLineSegment(sketch, "E1250", {"start": v(-78.88, -51.74) * mm, "end": v(-78.51, -51.65) * mm});
            skLineSegment(sketch, "E1251", {"start": v(-78.51, -51.65) * mm, "end": v(-78.16, -51.57) * mm});
            skLineSegment(sketch, "E1252", {"start": v(-78.16, -51.57) * mm, "end": v(-77.82, -51.48) * mm});
            skLineSegment(sketch, "E1253", {"start": v(-77.82, -51.48) * mm, "end": v(-77.49, -51.39) * mm});
            skLineSegment(sketch, "E1254", {"start": v(-77.49, -51.39) * mm, "end": v(-77.17, -51.3) * mm});
            skLineSegment(sketch, "E1255", {"start": v(-77.17, -51.3) * mm, "end": v(-76.87, -51.2) * mm});
            skLineSegment(sketch, "E1256", {"start": v(-76.87, -51.2) * mm, "end": v(-76.57, -51.12) * mm});
            skLineSegment(sketch, "E1257", {"start": v(-76.57, -51.12) * mm, "end": v(-76.3, -51.03) * mm});
            skLineSegment(sketch, "E1258", {"start": v(-76.3, -51.03) * mm, "end": v(-75.8, -51.46) * mm});
            skLineSegment(sketch, "E1259", {"start": v(-75.8, -51.46) * mm, "end": v(-74.12, -53.85) * mm});
            skLineSegment(sketch, "E1260", {"start": v(-74.12, -53.85) * mm, "end": v(-73.88, -54.46) * mm});
            skLineSegment(sketch, "E1261", {"start": v(-73.88, -54.46) * mm, "end": v(-74.06, -54.7) * mm});
            skLineSegment(sketch, "E1262", {"start": v(-74.06, -54.7) * mm, "end": v(-74.24, -54.94) * mm});
            skLineSegment(sketch, "E1263", {"start": v(-74.24, -54.94) * mm, "end": v(-74.43, -55.2) * mm});
            skLineSegment(sketch, "E1264", {"start": v(-74.43, -55.2) * mm, "end": v(-74.62, -55.46) * mm});
            skLineSegment(sketch, "E1265", {"start": v(-74.62, -55.46) * mm, "end": v(-74.82, -55.74) * mm});
            skLineSegment(sketch, "E1266", {"start": v(-74.82, -55.74) * mm, "end": v(-75.02, -56.04) * mm});
            skLineSegment(sketch, "E1267", {"start": v(-75.02, -56.04) * mm, "end": v(-75.22, -56.34) * mm});
            skLineSegment(sketch, "E1268", {"start": v(-75.22, -56.34) * mm, "end": v(-75.43, -56.65) * mm});
            skLineSegment(sketch, "E1269", {"start": v(-75.43, -56.65) * mm, "end": v(-75.63, -56.98) * mm});
            skLineSegment(sketch, "E1270", {"start": v(-75.63, -56.98) * mm, "end": v(-75.84, -57.32) * mm});
            skLineSegment(sketch, "E1271", {"start": v(-75.84, -57.32) * mm, "end": v(-76.06, -57.68) * mm});
            skLineSegment(sketch, "E1272", {"start": v(-76.06, -57.68) * mm, "end": v(-76.27, -58.05) * mm});
            skLineSegment(sketch, "E1273", {"start": v(-76.27, -58.05) * mm, "end": v(-76.49, -58.42) * mm});
            skLineSegment(sketch, "E1274", {"start": v(-76.49, -58.42) * mm, "end": v(-76.7, -58.82) * mm});
            skLineSegment(sketch, "E1275", {"start": v(-76.7, -58.82) * mm, "end": v(-76.92, -59.22) * mm});
            skLineSegment(sketch, "E1276", {"start": v(-76.92, -59.22) * mm, "end": v(-77.14, -59.64) * mm});
            skLineSegment(sketch, "E1277", {"start": v(-77.14, -59.64) * mm, "end": v(-77.36, -60.07) * mm});
            skLineSegment(sketch, "E1278", {"start": v(-77.36, -60.07) * mm, "end": v(-77.59, -60.52) * mm});
            skLineSegment(sketch, "E1279", {"start": v(-77.59, -60.52) * mm, "end": v(-77.8, -60.98) * mm});
            skLineSegment(sketch, "E1280", {"start": v(-77.8, -60.98) * mm, "end": v(-78.02, -61.45) * mm});
            skLineSegment(sketch, "E1281", {"start": v(-78.02, -61.45) * mm, "end": v(-78.24, -61.93) * mm});
            skLineSegment(sketch, "E1282", {"start": v(-78.24, -61.93) * mm, "end": v(-78.46, -62.43) * mm});
            skLineSegment(sketch, "E1283", {"start": v(-78.46, -62.43) * mm, "end": v(-78.68, -62.95) * mm});
            skLineSegment(sketch, "E1284", {"start": v(-78.68, -62.95) * mm, "end": v(-78.9, -63.47) * mm});
            skLineSegment(sketch, "E1285", {"start": v(-78.9, -63.47) * mm, "end": v(-79.11, -64.01) * mm});
            skLineSegment(sketch, "E1286", {"start": v(-79.11, -64.01) * mm, "end": v(-79.32, -64.56) * mm});
            skLineSegment(sketch, "E1287", {"start": v(-79.32, -64.56) * mm, "end": v(-79.53, -65.13) * mm});
            skLineSegment(sketch, "E1288", {"start": v(-79.53, -65.13) * mm, "end": v(-79.74, -65.71) * mm});
            skLineSegment(sketch, "E1289", {"start": v(-79.74, -65.71) * mm, "end": v(-79.94, -66.3) * mm});
            skLineSegment(sketch, "E1290", {"start": v(-79.94, -66.3) * mm, "end": v(-80.15, -66.91) * mm});
            skLineSegment(sketch, "E1291", {"start": v(-80.15, -66.91) * mm, "end": v(-80.34, -67.53) * mm});
            skLineSegment(sketch, "E1292", {"start": v(-80.34, -67.53) * mm, "end": v(-80.54, -68.17) * mm});
            skLineSegment(sketch, "E1293", {"start": v(-80.54, -68.17) * mm, "end": v(-80.54, -68.66) * mm});
            skLineSegment(sketch, "E1294", {"start": v(-80.54, -68.66) * mm, "end": v(-78.99, -70.44) * mm});
            skLineSegment(sketch, "E1295", {"start": v(-78.99, -70.44) * mm, "end": v(-78.5, -70.5) * mm});
            skLineSegment(sketch, "E1296", {"start": v(-78.5, -70.5) * mm, "end": v(-77.85, -70.4) * mm});
            skLineSegment(sketch, "E1297", {"start": v(-77.85, -70.4) * mm, "end": v(-77.2, -70.29) * mm});
            skLineSegment(sketch, "E1298", {"start": v(-77.2, -70.29) * mm, "end": v(-76.57, -70.17) * mm});
            skLineSegment(sketch, "E1299", {"start": v(-76.57, -70.17) * mm, "end": v(-75.96, -70.05) * mm});
            skLineSegment(sketch, "E1300", {"start": v(-75.96, -70.05) * mm, "end": v(-75.36, -69.92) * mm});
            skLineSegment(sketch, "E1301", {"start": v(-75.36, -69.92) * mm, "end": v(-74.76, -69.8) * mm});
            skLineSegment(sketch, "E1302", {"start": v(-74.76, -69.8) * mm, "end": v(-74.19, -69.66) * mm});
            skLineSegment(sketch, "E1303", {"start": v(-74.19, -69.66) * mm, "end": v(-73.62, -69.52) * mm});
            skLineSegment(sketch, "E1304", {"start": v(-73.62, -69.52) * mm, "end": v(-73.07, -69.37) * mm});
            skLineSegment(sketch, "E1305", {"start": v(-73.07, -69.37) * mm, "end": v(-72.54, -69.23) * mm});
            skLineSegment(sketch, "E1306", {"start": v(-72.54, -69.23) * mm, "end": v(-72.01, -69.08) * mm});
            skLineSegment(sketch, "E1307", {"start": v(-72.01, -69.08) * mm, "end": v(-71.5, -68.93) * mm});
            skLineSegment(sketch, "E1308", {"start": v(-71.5, -68.93) * mm, "end": v(-71, -68.78) * mm});
            skLineSegment(sketch, "E1309", {"start": v(-71, -68.78) * mm, "end": v(-70.52, -68.62) * mm});
            skLineSegment(sketch, "E1310", {"start": v(-70.52, -68.62) * mm, "end": v(-70.05, -68.46) * mm});
            skLineSegment(sketch, "E1311", {"start": v(-70.05, -68.46) * mm, "end": v(-69.6, -68.3) * mm});
            skLineSegment(sketch, "E1312", {"start": v(-69.6, -68.3) * mm, "end": v(-69.15, -68.14) * mm});
            skLineSegment(sketch, "E1313", {"start": v(-69.15, -68.14) * mm, "end": v(-68.71, -67.98) * mm});
            skLineSegment(sketch, "E1314", {"start": v(-68.71, -67.98) * mm, "end": v(-68.3, -67.82) * mm});
            skLineSegment(sketch, "E1315", {"start": v(-68.3, -67.82) * mm, "end": v(-67.9, -67.66) * mm});
            skLineSegment(sketch, "E1316", {"start": v(-67.9, -67.66) * mm, "end": v(-67.5, -67.5) * mm});
            skLineSegment(sketch, "E1317", {"start": v(-67.5, -67.5) * mm, "end": v(-67.12, -67.33) * mm});
            skLineSegment(sketch, "E1318", {"start": v(-67.12, -67.33) * mm, "end": v(-66.75, -67.17) * mm});
            skLineSegment(sketch, "E1319", {"start": v(-66.75, -67.17) * mm, "end": v(-66.4, -67) * mm});
            skLineSegment(sketch, "E1320", {"start": v(-66.4, -67) * mm, "end": v(-66.06, -66.85) * mm});
            skLineSegment(sketch, "E1321", {"start": v(-66.06, -66.85) * mm, "end": v(-65.73, -66.69) * mm});
            skLineSegment(sketch, "E1322", {"start": v(-65.73, -66.69) * mm, "end": v(-65.41, -66.53) * mm});
            skLineSegment(sketch, "E1323", {"start": v(-65.41, -66.53) * mm, "end": v(-65.1, -66.38) * mm});
            skLineSegment(sketch, "E1324", {"start": v(-65.1, -66.38) * mm, "end": v(-64.82, -66.22) * mm});
            skLineSegment(sketch, "E1325", {"start": v(-64.82, -66.22) * mm, "end": v(-64.54, -66.07) * mm});
            skLineSegment(sketch, "E1326", {"start": v(-64.54, -66.07) * mm, "end": v(-64.27, -65.92) * mm});
            skLineSegment(sketch, "E1327", {"start": v(-64.27, -65.92) * mm, "end": v(-64.02, -65.78) * mm});
            skLineSegment(sketch, "E1328", {"start": v(-64.02, -65.78) * mm, "end": v(-63.44, -66.1) * mm});
            skLineSegment(sketch, "E1329", {"start": v(-63.44, -66.1) * mm, "end": v(-61.3, -68.08) * mm});
            skLineSegment(sketch, "E1330", {"start": v(-61.3, -68.08) * mm, "end": v(-60.94, -68.64) * mm});
            skLineSegment(sketch, "E1331", {"start": v(-60.94, -68.64) * mm, "end": v(-61.07, -68.9) * mm});
            skLineSegment(sketch, "E1332", {"start": v(-61.07, -68.9) * mm, "end": v(-61.2, -69.18) * mm});
            skLineSegment(sketch, "E1333", {"start": v(-61.2, -69.18) * mm, "end": v(-61.33, -69.47) * mm});
            skLineSegment(sketch, "E1334", {"start": v(-61.33, -69.47) * mm, "end": v(-61.46, -69.77) * mm});
            skLineSegment(sketch, "E1335", {"start": v(-61.46, -69.77) * mm, "end": v(-61.6, -70.08) * mm});
            skLineSegment(sketch, "E1336", {"start": v(-61.6, -70.08) * mm, "end": v(-61.73, -70.4) * mm});
            skLineSegment(sketch, "E1337", {"start": v(-61.73, -70.4) * mm, "end": v(-61.86, -70.75) * mm});
            skLineSegment(sketch, "E1338", {"start": v(-61.86, -70.75) * mm, "end": v(-62, -71.1) * mm});
            skLineSegment(sketch, "E1339", {"start": v(-62, -71.1) * mm, "end": v(-62.13, -71.46) * mm});
            skLineSegment(sketch, "E1340", {"start": v(-62.13, -71.46) * mm, "end": v(-62.27, -71.84) * mm});
            skLineSegment(sketch, "E1341", {"start": v(-62.27, -71.84) * mm, "end": v(-62.4, -72.23) * mm});
            skLineSegment(sketch, "E1342", {"start": v(-62.4, -72.23) * mm, "end": v(-62.54, -72.64) * mm});
            skLineSegment(sketch, "E1343", {"start": v(-62.54, -72.64) * mm, "end": v(-62.67, -73.05) * mm});
            skLineSegment(sketch, "E1344", {"start": v(-62.67, -73.05) * mm, "end": v(-62.8, -73.48) * mm});
            skLineSegment(sketch, "E1345", {"start": v(-62.8, -73.48) * mm, "end": v(-62.93, -73.92) * mm});
            skLineSegment(sketch, "E1346", {"start": v(-62.93, -73.92) * mm, "end": v(-63.06, -74.38) * mm});
            skLineSegment(sketch, "E1347", {"start": v(-63.06, -74.38) * mm, "end": v(-63.18, -74.85) * mm});
            skLineSegment(sketch, "E1348", {"start": v(-63.18, -74.85) * mm, "end": v(-63.3, -75.33) * mm});
            skLineSegment(sketch, "E1349", {"start": v(-63.3, -75.33) * mm, "end": v(-63.43, -75.82) * mm});
            skLineSegment(sketch, "E1350", {"start": v(-63.43, -75.82) * mm, "end": v(-63.54, -76.33) * mm});
            skLineSegment(sketch, "E1351", {"start": v(-63.54, -76.33) * mm, "end": v(-63.66, -76.85) * mm});
            skLineSegment(sketch, "E1352", {"start": v(-63.66, -76.85) * mm, "end": v(-63.77, -77.38) * mm});
            skLineSegment(sketch, "E1353", {"start": v(-63.77, -77.38) * mm, "end": v(-63.87, -77.93) * mm});
            skLineSegment(sketch, "E1354", {"start": v(-63.87, -77.93) * mm, "end": v(-63.98, -78.49) * mm});
            skLineSegment(sketch, "E1355", {"start": v(-63.98, -78.49) * mm, "end": v(-64.07, -79.06) * mm});
            skLineSegment(sketch, "E1356", {"start": v(-64.07, -79.06) * mm, "end": v(-64.17, -79.65) * mm});
            skLineSegment(sketch, "E1357", {"start": v(-64.17, -79.65) * mm, "end": v(-64.25, -80.24) * mm});
            skLineSegment(sketch, "E1358", {"start": v(-64.25, -80.24) * mm, "end": v(-64.34, -80.85) * mm});
            skLineSegment(sketch, "E1359", {"start": v(-64.34, -80.85) * mm, "end": v(-64.41, -81.48) * mm});
            skLineSegment(sketch, "E1360", {"start": v(-64.41, -81.48) * mm, "end": v(-64.48, -82.11) * mm});
            skLineSegment(sketch, "E1361", {"start": v(-64.48, -82.11) * mm, "end": v(-64.55, -82.76) * mm});
            skLineSegment(sketch, "E1362", {"start": v(-64.55, -82.76) * mm, "end": v(-64.6, -83.43) * mm});
            skLineSegment(sketch, "E1363", {"start": v(-64.6, -83.43) * mm, "end": v(-64.5, -83.9) * mm});
            skLineSegment(sketch, "E1364", {"start": v(-64.5, -83.9) * mm, "end": v(-62.62, -85.32) * mm});
            skLineSegment(sketch, "E1365", {"start": v(-62.62, -85.32) * mm, "end": v(-62.13, -85.29) * mm});
            skLineSegment(sketch, "E1366", {"start": v(-62.13, -85.29) * mm, "end": v(-61.5, -85.05) * mm});
            skLineSegment(sketch, "E1367", {"start": v(-61.5, -85.05) * mm, "end": v(-60.9, -84.8) * mm});
            skLineSegment(sketch, "E1368", {"start": v(-60.9, -84.8) * mm, "end": v(-60.31, -84.56) * mm});
            skLineSegment(sketch, "E1369", {"start": v(-60.31, -84.56) * mm, "end": v(-59.73, -84.31) * mm});
            skLineSegment(sketch, "E1370", {"start": v(-59.73, -84.31) * mm, "end": v(-59.17, -84.06) * mm});
            skLineSegment(sketch, "E1371", {"start": v(-59.17, -84.06) * mm, "end": v(-58.62, -83.81) * mm});
            skLineSegment(sketch, "E1372", {"start": v(-58.62, -83.81) * mm, "end": v(-58.08, -83.56) * mm});
            skLineSegment(sketch, "E1373", {"start": v(-58.08, -83.56) * mm, "end": v(-57.56, -83.3) * mm});
            skLineSegment(sketch, "E1374", {"start": v(-57.56, -83.3) * mm, "end": v(-57.05, -83.05) * mm});
            skLineSegment(sketch, "E1375", {"start": v(-57.05, -83.05) * mm, "end": v(-56.56, -82.8) * mm});
            skLineSegment(sketch, "E1376", {"start": v(-56.56, -82.8) * mm, "end": v(-56.08, -82.54) * mm});
            skLineSegment(sketch, "E1377", {"start": v(-56.08, -82.54) * mm, "end": v(-55.6, -82.29) * mm});
            skLineSegment(sketch, "E1378", {"start": v(-55.6, -82.29) * mm, "end": v(-55.15, -82.04) * mm});
            skLineSegment(sketch, "E1379", {"start": v(-55.15, -82.04) * mm, "end": v(-54.71, -81.78) * mm});
            skLineSegment(sketch, "E1380", {"start": v(-54.71, -81.78) * mm, "end": v(-54.29, -81.53) * mm});
            skLineSegment(sketch, "E1381", {"start": v(-54.29, -81.53) * mm, "end": v(-53.87, -81.28) * mm});
            skLineSegment(sketch, "E1382", {"start": v(-53.87, -81.28) * mm, "end": v(-53.47, -81.03) * mm});
            skLineSegment(sketch, "E1383", {"start": v(-53.47, -81.03) * mm, "end": v(-53.08, -80.78) * mm});
            skLineSegment(sketch, "E1384", {"start": v(-53.08, -80.78) * mm, "end": v(-52.7, -80.54) * mm});
            skLineSegment(sketch, "E1385", {"start": v(-52.7, -80.54) * mm, "end": v(-52.34, -80.3) * mm});
            skLineSegment(sketch, "E1386", {"start": v(-52.34, -80.3) * mm, "end": v(-52, -80.05) * mm});
            skLineSegment(sketch, "E1387", {"start": v(-52, -80.05) * mm, "end": v(-51.65, -79.81) * mm});
            skLineSegment(sketch, "E1388", {"start": v(-51.65, -79.81) * mm, "end": v(-51.33, -79.58) * mm});
            skLineSegment(sketch, "E1389", {"start": v(-51.33, -79.58) * mm, "end": v(-51.01, -79.35) * mm});
            skLineSegment(sketch, "E1390", {"start": v(-51.01, -79.35) * mm, "end": v(-50.71, -79.12) * mm});
            skLineSegment(sketch, "E1391", {"start": v(-50.71, -79.12) * mm, "end": v(-50.43, -78.9) * mm});
            skLineSegment(sketch, "E1392", {"start": v(-50.43, -78.9) * mm, "end": v(-50.15, -78.68) * mm});
            skLineSegment(sketch, "E1393", {"start": v(-50.15, -78.68) * mm, "end": v(-49.89, -78.46) * mm});
            skLineSegment(sketch, "E1394", {"start": v(-49.89, -78.46) * mm, "end": v(-49.63, -78.25) * mm});
            skLineSegment(sketch, "E1395", {"start": v(-49.63, -78.25) * mm, "end": v(-49.4, -78.05) * mm});
            skLineSegment(sketch, "E1396", {"start": v(-49.4, -78.05) * mm, "end": v(-49.16, -77.84) * mm});
            skLineSegment(sketch, "E1397", {"start": v(-49.16, -77.84) * mm, "end": v(-48.94, -77.65) * mm});
            skLineSegment(sketch, "E1398", {"start": v(-48.94, -77.65) * mm, "end": v(-48.31, -77.84) * mm});
            skLineSegment(sketch, "E1399", {"start": v(-48.31, -77.84) * mm, "end": v(-45.8, -79.34) * mm});
            skLineSegment(sketch, "E1400", {"start": v(-45.8, -79.34) * mm, "end": v(-45.34, -79.8) * mm});
            skLineSegment(sketch, "E1401", {"start": v(-45.34, -79.8) * mm, "end": v(-45.41, -80.1) * mm});
            skLineSegment(sketch, "E1402", {"start": v(-45.41, -80.1) * mm, "end": v(-45.48, -80.39) * mm});
            skLineSegment(sketch, "E1403", {"start": v(-45.48, -80.39) * mm, "end": v(-45.55, -80.7) * mm});
            skLineSegment(sketch, "E1404", {"start": v(-45.55, -80.7) * mm, "end": v(-45.61, -81.02) * mm});
            skLineSegment(sketch, "E1405", {"start": v(-45.61, -81.02) * mm, "end": v(-45.68, -81.36) * mm});
            skLineSegment(sketch, "E1406", {"start": v(-45.68, -81.36) * mm, "end": v(-45.74, -81.7) * mm});
            skLineSegment(sketch, "E1407", {"start": v(-45.74, -81.7) * mm, "end": v(-45.8, -82.06) * mm});
            skLineSegment(sketch, "E1408", {"start": v(-45.8, -82.06) * mm, "end": v(-45.86, -82.44) * mm});
            skLineSegment(sketch, "E1409", {"start": v(-45.86, -82.44) * mm, "end": v(-45.92, -82.82) * mm});
            skLineSegment(sketch, "E1410", {"start": v(-45.92, -82.82) * mm, "end": v(-45.97, -83.22) * mm});
            skLineSegment(sketch, "E1411", {"start": v(-45.97, -83.22) * mm, "end": v(-46.02, -83.63) * mm});
            skLineSegment(sketch, "E1412", {"start": v(-46.02, -83.63) * mm, "end": v(-46.07, -84.05) * mm});
            skLineSegment(sketch, "E1413", {"start": v(-46.07, -84.05) * mm, "end": v(-46.11, -84.48) * mm});
            skLineSegment(sketch, "E1414", {"start": v(-46.11, -84.48) * mm, "end": v(-46.15, -84.93) * mm});
            skLineSegment(sketch, "E1415", {"start": v(-46.15, -84.93) * mm, "end": v(-46.19, -85.4) * mm});
            skLineSegment(sketch, "E1416", {"start": v(-46.19, -85.4) * mm, "end": v(-46.22, -85.86) * mm});
            skLineSegment(sketch, "E1417", {"start": v(-46.22, -85.86) * mm, "end": v(-46.24, -86.35) * mm});
            skLineSegment(sketch, "E1418", {"start": v(-46.24, -86.35) * mm, "end": v(-46.26, -86.84) * mm});
            skLineSegment(sketch, "E1419", {"start": v(-46.26, -86.84) * mm, "end": v(-46.28, -87.35) * mm});
            skLineSegment(sketch, "E1420", {"start": v(-46.28, -87.35) * mm, "end": v(-46.29, -87.87) * mm});
            skLineSegment(sketch, "E1421", {"start": v(-46.29, -87.87) * mm, "end": v(-46.29, -88.4) * mm});
            skLineSegment(sketch, "E1422", {"start": v(-46.29, -88.4) * mm, "end": v(-46.29, -88.95) * mm});
            skLineSegment(sketch, "E1423", {"start": v(-46.29, -88.95) * mm, "end": v(-46.28, -89.5) * mm});
            skLineSegment(sketch, "E1424", {"start": v(-46.28, -89.5) * mm, "end": v(-46.26, -90.07) * mm});
            skLineSegment(sketch, "E1425", {"start": v(-46.26, -90.07) * mm, "end": v(-46.24, -90.65) * mm});
            skLineSegment(sketch, "E1426", {"start": v(-46.24, -90.65) * mm, "end": v(-46.2, -91.25) * mm});
            skLineSegment(sketch, "E1427", {"start": v(-46.2, -91.25) * mm, "end": v(-46.17, -91.85) * mm});
            skLineSegment(sketch, "E1428", {"start": v(-46.17, -91.85) * mm, "end": v(-46.12, -92.46) * mm});
            skLineSegment(sketch, "E1429", {"start": v(-46.12, -92.46) * mm, "end": v(-46.07, -93.09) * mm});
            skLineSegment(sketch, "E1430", {"start": v(-46.07, -93.09) * mm, "end": v(-46, -93.73) * mm});
            skLineSegment(sketch, "E1431", {"start": v(-46, -93.73) * mm, "end": v(-45.93, -94.37) * mm});
            skLineSegment(sketch, "E1432", {"start": v(-45.93, -94.37) * mm, "end": v(-45.85, -95.03) * mm});
            skLineSegment(sketch, "E1433", {"start": v(-45.85, -95.03) * mm, "end": v(-45.65, -95.48) * mm});
            skLineSegment(sketch, "E1434", {"start": v(-45.65, -95.48) * mm, "end": v(-43.5, -96.48) * mm});
            skLineSegment(sketch, "E1435", {"start": v(-43.5, -96.48) * mm, "end": v(-43.04, -96.34) * mm});
            skLineSegment(sketch, "E1436", {"start": v(-43.04, -96.34) * mm, "end": v(-42.48, -95.98) * mm});
            skLineSegment(sketch, "E1437", {"start": v(-42.48, -95.98) * mm, "end": v(-41.94, -95.61) * mm});
            skLineSegment(sketch, "E1438", {"start": v(-41.94, -95.61) * mm, "end": v(-41.41, -95.25) * mm});
            skLineSegment(sketch, "E1439", {"start": v(-41.41, -95.25) * mm, "end": v(-40.9, -94.89) * mm});
            skLineSegment(sketch, "E1440", {"start": v(-40.9, -94.89) * mm, "end": v(-40.4, -94.53) * mm});
            skLineSegment(sketch, "E1441", {"start": v(-40.4, -94.53) * mm, "end": v(-39.91, -94.17) * mm});
            skLineSegment(sketch, "E1442", {"start": v(-39.91, -94.17) * mm, "end": v(-39.44, -93.8) * mm});
            skLineSegment(sketch, "E1443", {"start": v(-39.44, -93.8) * mm, "end": v(-38.98, -93.45) * mm});
            skLineSegment(sketch, "E1444", {"start": v(-38.98, -93.45) * mm, "end": v(-38.54, -93.1) * mm});
            skLineSegment(sketch, "E1445", {"start": v(-38.54, -93.1) * mm, "end": v(-38.1, -92.75) * mm});
            skLineSegment(sketch, "E1446", {"start": v(-38.1, -92.75) * mm, "end": v(-37.69, -92.4) * mm});
            skLineSegment(sketch, "E1447", {"start": v(-37.69, -92.4) * mm, "end": v(-37.28, -92.05) * mm});
            skLineSegment(sketch, "E1448", {"start": v(-37.28, -92.05) * mm, "end": v(-36.9, -91.7) * mm});
            skLineSegment(sketch, "E1449", {"start": v(-36.9, -91.7) * mm, "end": v(-36.51, -91.37) * mm});
            skLineSegment(sketch, "E1450", {"start": v(-36.51, -91.37) * mm, "end": v(-36.15, -91.03) * mm});
            skLineSegment(sketch, "E1451", {"start": v(-36.15, -91.03) * mm, "end": v(-35.8, -90.7) * mm});
            skLineSegment(sketch, "E1452", {"start": v(-35.8, -90.7) * mm, "end": v(-35.45, -90.38) * mm});
            skLineSegment(sketch, "E1453", {"start": v(-35.45, -90.38) * mm, "end": v(-35.12, -90.05) * mm});
            skLineSegment(sketch, "E1454", {"start": v(-35.12, -90.05) * mm, "end": v(-34.8, -89.74) * mm});
            skLineSegment(sketch, "E1455", {"start": v(-34.8, -89.74) * mm, "end": v(-34.5, -89.42) * mm});
            skLineSegment(sketch, "E1456", {"start": v(-34.5, -89.42) * mm, "end": v(-34.21, -89.11) * mm});
            skLineSegment(sketch, "E1457", {"start": v(-34.21, -89.11) * mm, "end": v(-33.93, -88.81) * mm});
            skLineSegment(sketch, "E1458", {"start": v(-33.93, -88.81) * mm, "end": v(-33.66, -88.51) * mm});
            skLineSegment(sketch, "E1459", {"start": v(-33.66, -88.51) * mm, "end": v(-33.4, -88.22) * mm});
            skLineSegment(sketch, "E1460", {"start": v(-33.4, -88.22) * mm, "end": v(-33.16, -87.94) * mm});
            skLineSegment(sketch, "E1461", {"start": v(-33.16, -87.94) * mm, "end": v(-32.92, -87.66) * mm});
            skLineSegment(sketch, "E1462", {"start": v(-32.92, -87.66) * mm, "end": v(-32.7, -87.39) * mm});
            skLineSegment(sketch, "E1463", {"start": v(-32.7, -87.39) * mm, "end": v(-32.48, -87.12) * mm});
            skLineSegment(sketch, "E1464", {"start": v(-32.48, -87.12) * mm, "end": v(-32.28, -86.86) * mm});
            skLineSegment(sketch, "E1465", {"start": v(-32.28, -86.86) * mm, "end": v(-32.09, -86.6) * mm});
            skLineSegment(sketch, "E1466", {"start": v(-32.09, -86.6) * mm, "end": v(-31.9, -86.36) * mm});
            skLineSegment(sketch, "E1467", {"start": v(-31.9, -86.36) * mm, "end": v(-31.73, -86.13) * mm});
            skLineSegment(sketch, "E1468", {"start": v(-31.73, -86.13) * mm, "end": v(-31.07, -86.18) * mm});
            skLineSegment(sketch, "E1469", {"start": v(-31.07, -86.18) * mm, "end": v(-28.3, -87.13) * mm});
            skLineSegment(sketch, "E1470", {"start": v(-28.3, -87.13) * mm, "end": v(-27.76, -87.49) * mm});
            skLineSegment(sketch, "E1471", {"start": v(-27.76, -87.49) * mm, "end": v(-27.77, -87.78) * mm});
            skLineSegment(sketch, "E1472", {"start": v(-27.77, -87.78) * mm, "end": v(-27.77, -88.09) * mm});
            skLineSegment(sketch, "E1473", {"start": v(-27.77, -88.09) * mm, "end": v(-27.77, -88.4) * mm});
            skLineSegment(sketch, "E1474", {"start": v(-27.77, -88.4) * mm, "end": v(-27.77, -88.73) * mm});
            skLineSegment(sketch, "E1475", {"start": v(-27.77, -88.73) * mm, "end": v(-27.76, -89.08) * mm});
            skLineSegment(sketch, "E1476", {"start": v(-27.76, -89.08) * mm, "end": v(-27.76, -89.43) * mm});
            skLineSegment(sketch, "E1477", {"start": v(-27.76, -89.43) * mm, "end": v(-27.74, -89.8) * mm});
            skLineSegment(sketch, "E1478", {"start": v(-27.74, -89.8) * mm, "end": v(-27.72, -90.17) * mm});
            skLineSegment(sketch, "E1479", {"start": v(-27.72, -90.17) * mm, "end": v(-27.7, -90.56) * mm});
            skLineSegment(sketch, "E1480", {"start": v(-27.7, -90.56) * mm, "end": v(-27.67, -90.96) * mm});
            skLineSegment(sketch, "E1481", {"start": v(-27.67, -90.96) * mm, "end": v(-27.63, -91.37) * mm});
            skLineSegment(sketch, "E1482", {"start": v(-27.63, -91.37) * mm, "end": v(-27.59, -91.8) * mm});
            skLineSegment(sketch, "E1483", {"start": v(-27.59, -91.8) * mm, "end": v(-27.54, -92.23) * mm});
            skLineSegment(sketch, "E1484", {"start": v(-27.54, -92.23) * mm, "end": v(-27.48, -92.67) * mm});
            skLineSegment(sketch, "E1485", {"start": v(-27.48, -92.67) * mm, "end": v(-27.42, -93.13) * mm});
            skLineSegment(sketch, "E1486", {"start": v(-27.42, -93.13) * mm, "end": v(-27.35, -93.6) * mm});
            skLineSegment(sketch, "E1487", {"start": v(-27.35, -93.6) * mm, "end": v(-27.28, -94.07) * mm});
            skLineSegment(sketch, "E1488", {"start": v(-27.28, -94.07) * mm, "end": v(-27.2, -94.56) * mm});
            skLineSegment(sketch, "E1489", {"start": v(-27.2, -94.56) * mm, "end": v(-27.1, -95.06) * mm});
            skLineSegment(sketch, "E1490", {"start": v(-27.1, -95.06) * mm, "end": v(-27, -95.58) * mm});
            skLineSegment(sketch, "E1491", {"start": v(-27, -95.58) * mm, "end": v(-26.9, -96.1) * mm});
            skLineSegment(sketch, "E1492", {"start": v(-26.9, -96.1) * mm, "end": v(-26.78, -96.63) * mm});
            skLineSegment(sketch, "E1493", {"start": v(-26.78, -96.63) * mm, "end": v(-26.66, -97.17) * mm});
            skLineSegment(sketch, "E1494", {"start": v(-26.66, -97.17) * mm, "end": v(-26.52, -97.72) * mm});
            skLineSegment(sketch, "E1495", {"start": v(-26.52, -97.72) * mm, "end": v(-26.38, -98.29) * mm});
            skLineSegment(sketch, "E1496", {"start": v(-26.38, -98.29) * mm, "end": v(-26.22, -98.86) * mm});
            skLineSegment(sketch, "E1497", {"start": v(-26.22, -98.86) * mm, "end": v(-26.06, -99.44) * mm});
            skLineSegment(sketch, "E1498", {"start": v(-26.06, -99.44) * mm, "end": v(-25.89, -100.03) * mm});
            skLineSegment(sketch, "E1499", {"start": v(-25.89, -100.03) * mm, "end": v(-25.7, -100.63) * mm});
            skLineSegment(sketch, "E1500", {"start": v(-25.7, -100.63) * mm, "end": v(-25.5, -101.24) * mm});
            skLineSegment(sketch, "E1501", {"start": v(-25.5, -101.24) * mm, "end": v(-25.3, -101.86) * mm});
            skLineSegment(sketch, "E1502", {"start": v(-25.3, -101.86) * mm, "end": v(-25.09, -102.5) * mm});
            skLineSegment(sketch, "E1503", {"start": v(-25.09, -102.5) * mm, "end": v(-24.8, -102.89) * mm});
            skLineSegment(sketch, "E1504", {"start": v(-24.8, -102.89) * mm, "end": v(-22.5, -103.41) * mm});
            skLineSegment(sketch, "E1505", {"start": v(-22.5, -103.41) * mm, "end": v(-22.07, -103.18) * mm});
            skLineSegment(sketch, "E1506", {"start": v(-22.07, -103.18) * mm, "end": v(-21.6, -102.71) * mm});
            skLineSegment(sketch, "E1507", {"start": v(-21.6, -102.71) * mm, "end": v(-21.15, -102.24) * mm});
            skLineSegment(sketch, "E1508", {"start": v(-21.15, -102.24) * mm, "end": v(-20.7, -101.78) * mm});
            skLineSegment(sketch, "E1509", {"start": v(-20.7, -101.78) * mm, "end": v(-20.28, -101.32) * mm});
            skLineSegment(sketch, "E1510", {"start": v(-20.28, -101.32) * mm, "end": v(-19.86, -100.86) * mm});
            skLineSegment(sketch, "E1511", {"start": v(-19.86, -100.86) * mm, "end": v(-19.46, -100.4) * mm});
            skLineSegment(sketch, "E1512", {"start": v(-19.46, -100.4) * mm, "end": v(-19.08, -99.96) * mm});
            skLineSegment(sketch, "E1513", {"start": v(-19.08, -99.96) * mm, "end": v(-18.7, -99.52) * mm});
            skLineSegment(sketch, "E1514", {"start": v(-18.7, -99.52) * mm, "end": v(-18.34, -99.08) * mm});
            skLineSegment(sketch, "E1515", {"start": v(-18.34, -99.08) * mm, "end": v(-18, -98.64) * mm});
            skLineSegment(sketch, "E1516", {"start": v(-18, -98.64) * mm, "end": v(-17.65, -98.22) * mm});
            skLineSegment(sketch, "E1517", {"start": v(-17.65, -98.22) * mm, "end": v(-17.33, -97.8) * mm});
            skLineSegment(sketch, "E1518", {"start": v(-17.33, -97.8) * mm, "end": v(-17.02, -97.38) * mm});
            skLineSegment(sketch, "E1519", {"start": v(-17.02, -97.38) * mm, "end": v(-16.72, -96.97) * mm});
            skLineSegment(sketch, "E1520", {"start": v(-16.72, -96.97) * mm, "end": v(-16.43, -96.56) * mm});
            skLineSegment(sketch, "E1521", {"start": v(-16.43, -96.56) * mm, "end": v(-16.15, -96.16) * mm});
            skLineSegment(sketch, "E1522", {"start": v(-16.15, -96.16) * mm, "end": v(-15.89, -95.77) * mm});
            skLineSegment(sketch, "E1523", {"start": v(-15.89, -95.77) * mm, "end": v(-15.63, -95.39) * mm});
            skLineSegment(sketch, "E1524", {"start": v(-15.63, -95.39) * mm, "end": v(-15.4, -95.01) * mm});
            skLineSegment(sketch, "E1525", {"start": v(-15.4, -95.01) * mm, "end": v(-15.16, -94.64) * mm});
            skLineSegment(sketch, "E1526", {"start": v(-15.16, -94.64) * mm, "end": v(-14.94, -94.28) * mm});
            skLineSegment(sketch, "E1527", {"start": v(-14.94, -94.28) * mm, "end": v(-14.72, -93.92) * mm});
            skLineSegment(sketch, "E1528", {"start": v(-14.72, -93.92) * mm, "end": v(-14.52, -93.58) * mm});
            skLineSegment(sketch, "E1529", {"start": v(-14.52, -93.58) * mm, "end": v(-14.33, -93.24) * mm});
            skLineSegment(sketch, "E1530", {"start": v(-14.33, -93.24) * mm, "end": v(-14.15, -92.9) * mm});
            skLineSegment(sketch, "E1531", {"start": v(-14.15, -92.9) * mm, "end": v(-13.98, -92.59) * mm});
            skLineSegment(sketch, "E1532", {"start": v(-13.98, -92.59) * mm, "end": v(-13.81, -92.27) * mm});
            skLineSegment(sketch, "E1533", {"start": v(-13.81, -92.27) * mm, "end": v(-13.66, -91.97) * mm});
            skLineSegment(sketch, "E1534", {"start": v(-13.66, -91.97) * mm, "end": v(-13.51, -91.67) * mm});
            skLineSegment(sketch, "E1535", {"start": v(-13.51, -91.67) * mm, "end": v(-13.38, -91.39) * mm});
            skLineSegment(sketch, "E1536", {"start": v(-13.38, -91.39) * mm, "end": v(-13.25, -91.11) * mm});
            skLineSegment(sketch, "E1537", {"start": v(-13.25, -91.11) * mm, "end": v(-13.13, -90.84) * mm});
            skLineSegment(sketch, "E1538", {"start": v(-13.13, -90.84) * mm, "end": v(-12.48, -90.76) * mm});
            skLineSegment(sketch, "E1539", {"start": v(-12.48, -90.76) * mm, "end": v(-9.58, -91.11) * mm});
            skLineSegment(sketch, "E1540", {"start": v(-9.58, -91.11) * mm, "end": v(-8.96, -91.35) * mm});
            skLineSegment(sketch, "E1541", {"start": v(-8.96, -91.35) * mm, "end": v(-8.9, -91.64) * mm});
            skLineSegment(sketch, "E1542", {"start": v(-8.9, -91.64) * mm, "end": v(-8.85, -91.94) * mm});
            skLineSegment(sketch, "E1543", {"start": v(-8.85, -91.94) * mm, "end": v(-8.79, -92.25) * mm});
            skLineSegment(sketch, "E1544", {"start": v(-8.79, -92.25) * mm, "end": v(-8.72, -92.57) * mm});
            skLineSegment(sketch, "E1545", {"start": v(-8.72, -92.57) * mm, "end": v(-8.64, -92.9) * mm});
            skLineSegment(sketch, "E1546", {"start": v(-8.64, -92.9) * mm, "end": v(-8.55, -93.24) * mm});
            skLineSegment(sketch, "E1547", {"start": v(-8.55, -93.24) * mm, "end": v(-8.47, -93.6) * mm});
            skLineSegment(sketch, "E1548", {"start": v(-8.47, -93.6) * mm, "end": v(-8.37, -93.96) * mm});
            skLineSegment(sketch, "E1549", {"start": v(-8.37, -93.96) * mm, "end": v(-8.26, -94.34) * mm});
            skLineSegment(sketch, "E1550", {"start": v(-8.26, -94.34) * mm, "end": v(-8.15, -94.72) * mm});
            skLineSegment(sketch, "E1551", {"start": v(-8.15, -94.72) * mm, "end": v(-8.03, -95.12) * mm});
            skLineSegment(sketch, "E1552", {"start": v(-8.03, -95.12) * mm, "end": v(-7.9, -95.52) * mm});
            skLineSegment(sketch, "E1553", {"start": v(-7.9, -95.52) * mm, "end": v(-7.76, -95.93) * mm});
            skLineSegment(sketch, "E1554", {"start": v(-7.76, -95.93) * mm, "end": v(-7.62, -96.36) * mm});
            skLineSegment(sketch, "E1555", {"start": v(-7.62, -96.36) * mm, "end": v(-7.46, -96.8) * mm});
            skLineSegment(sketch, "E1556", {"start": v(-7.46, -96.8) * mm, "end": v(-7.3, -97.24) * mm});
            skLineSegment(sketch, "E1557", {"start": v(-7.3, -97.24) * mm, "end": v(-7.12, -97.69) * mm});
            skLineSegment(sketch, "E1558", {"start": v(-7.12, -97.69) * mm, "end": v(-6.94, -98.15) * mm});
            skLineSegment(sketch, "E1559", {"start": v(-6.94, -98.15) * mm, "end": v(-6.75, -98.62) * mm});
            skLineSegment(sketch, "E1560", {"start": v(-6.75, -98.62) * mm, "end": v(-6.54, -99.1) * mm});
            skLineSegment(sketch, "E1561", {"start": v(-6.54, -99.1) * mm, "end": v(-6.33, -99.59) * mm});
            skLineSegment(sketch, "E1562", {"start": v(-6.33, -99.59) * mm, "end": v(-6.1, -100.09) * mm});
            skLineSegment(sketch, "E1563", {"start": v(-6.1, -100.09) * mm, "end": v(-5.87, -100.59) * mm});
            skLineSegment(sketch, "E1564", {"start": v(-5.87, -100.59) * mm, "end": v(-5.62, -101.1) * mm});
            skLineSegment(sketch, "E1565", {"start": v(-5.62, -101.1) * mm, "end": v(-5.37, -101.62) * mm});
            skLineSegment(sketch, "E1566", {"start": v(-5.37, -101.62) * mm, "end": v(-5.1, -102.15) * mm});
            skLineSegment(sketch, "E1567", {"start": v(-5.1, -102.15) * mm, "end": v(-4.82, -102.69) * mm});
            skLineSegment(sketch, "E1568", {"start": v(-4.82, -102.69) * mm, "end": v(-4.52, -103.23) * mm});
            skLineSegment(sketch, "E1569", {"start": v(-4.52, -103.23) * mm, "end": v(-4.22, -103.78) * mm});
            skLineSegment(sketch, "E1570", {"start": v(-4.22, -103.78) * mm, "end": v(-3.9, -104.33) * mm});
            skLineSegment(sketch, "E1571", {"start": v(-3.9, -104.33) * mm, "end": v(-3.57, -104.9) * mm});
            skLineSegment(sketch, "E1572", {"start": v(-3.57, -104.9) * mm, "end": v(-3.23, -105.47) * mm});
            skLineSegment(sketch, "E1573", {"start": v(-3.23, -105.47) * mm, "end": v(-2.87, -105.8) * mm});
            skLineSegment(sketch, "E1574", {"start": v(-2.87, -105.8) * mm, "end": v(-0.5, -105.83) * mm});
            skLineSegment(sketch, "E1575", {"start": v(-0.5, -105.83) * mm, "end": v(-0.13, -105.52) * mm});
            skLineSegment(sketch, "E1576", {"start": v(-0.13, -105.52) * mm, "end": v(0.23, -104.96) * mm});
            skLineSegment(sketch, "E1577", {"start": v(0.23, -104.96) * mm, "end": v(0.57, -104.4) * mm});
            skLineSegment(sketch, "E1578", {"start": v(0.57, -104.4) * mm, "end": v(0.9, -103.86) * mm});
            skLineSegment(sketch, "E1579", {"start": v(0.9, -103.86) * mm, "end": v(1.23, -103.32) * mm});
            skLineSegment(sketch, "E1580", {"start": v(1.23, -103.32) * mm, "end": v(1.54, -102.79) * mm});
            skLineSegment(sketch, "E1581", {"start": v(1.54, -102.79) * mm, "end": v(1.84, -102.26) * mm});
            skLineSegment(sketch, "E1582", {"start": v(1.84, -102.26) * mm, "end": v(2.12, -101.74) * mm});
            skLineSegment(sketch, "E1583", {"start": v(2.12, -101.74) * mm, "end": v(2.4, -101.23) * mm});
            skLineSegment(sketch, "E1584", {"start": v(2.4, -101.23) * mm, "end": v(2.66, -100.72) * mm});
            skLineSegment(sketch, "E1585", {"start": v(2.66, -100.72) * mm, "end": v(2.91, -100.23) * mm});
            skLineSegment(sketch, "E1586", {"start": v(2.91, -100.23) * mm, "end": v(3.15, -99.74) * mm});
            skLineSegment(sketch, "E1587", {"start": v(3.15, -99.74) * mm, "end": v(3.38, -99.26) * mm});
            skLineSegment(sketch, "E1588", {"start": v(3.38, -99.26) * mm, "end": v(3.6, -98.79) * mm});
            skLineSegment(sketch, "E1589", {"start": v(3.6, -98.79) * mm, "end": v(3.8, -98.32) * mm});
            skLineSegment(sketch, "E1590", {"start": v(3.8, -98.32) * mm, "end": v(4, -97.87) * mm});
            skLineSegment(sketch, "E1591", {"start": v(4, -97.87) * mm, "end": v(4.2, -97.42) * mm});
            skLineSegment(sketch, "E1592", {"start": v(4.2, -97.42) * mm, "end": v(4.37, -96.98) * mm});
            skLineSegment(sketch, "E1593", {"start": v(4.37, -96.98) * mm, "end": v(4.54, -96.55) * mm});
            skLineSegment(sketch, "E1594", {"start": v(4.54, -96.55) * mm, "end": v(4.7, -96.13) * mm});
            skLineSegment(sketch, "E1595", {"start": v(4.7, -96.13) * mm, "end": v(4.85, -95.72) * mm});
            skLineSegment(sketch, "E1596", {"start": v(4.85, -95.72) * mm, "end": v(5, -95.32) * mm});
            skLineSegment(sketch, "E1597", {"start": v(5, -95.32) * mm, "end": v(5.13, -94.93) * mm});
            skLineSegment(sketch, "E1598", {"start": v(5.13, -94.93) * mm, "end": v(5.25, -94.55) * mm});
            skLineSegment(sketch, "E1599", {"start": v(5.25, -94.55) * mm, "end": v(5.37, -94.18) * mm});
            skLineSegment(sketch, "E1600", {"start": v(5.37, -94.18) * mm, "end": v(5.48, -93.82) * mm});
            skLineSegment(sketch, "E1601", {"start": v(5.48, -93.82) * mm, "end": v(5.58, -93.47) * mm});
            skLineSegment(sketch, "E1602", {"start": v(5.58, -93.47) * mm, "end": v(5.67, -93.13) * mm});
            skLineSegment(sketch, "E1603", {"start": v(5.67, -93.13) * mm, "end": v(5.76, -92.8) * mm});
            skLineSegment(sketch, "E1604", {"start": v(5.76, -92.8) * mm, "end": v(5.84, -92.48) * mm});
            skLineSegment(sketch, "E1605", {"start": v(5.84, -92.48) * mm, "end": v(5.91, -92.17) * mm});
            skLineSegment(sketch, "E1606", {"start": v(5.91, -92.17) * mm, "end": v(5.98, -91.87) * mm});
            skLineSegment(sketch, "E1607", {"start": v(5.98, -91.87) * mm, "end": v(6.04, -91.59) * mm});
            skLineSegment(sketch, "E1608", {"start": v(6.04, -91.59) * mm, "end": v(6.67, -91.37) * mm});
            skLineSegment(sketch, "E1609", {"start": v(6.67, -91.37) * mm, "end": v(9.58, -91.11) * mm});
            skLineSegment(sketch, "E1610", {"start": v(9.58, -91.11) * mm, "end": v(10.23, -91.22) * mm});
            skLineSegment(sketch, "E1611", {"start": v(10.23, -91.22) * mm, "end": v(10.34, -91.49) * mm});
            skLineSegment(sketch, "E1612", {"start": v(10.34, -91.49) * mm, "end": v(10.46, -91.77) * mm});
            skLineSegment(sketch, "E1613", {"start": v(10.46, -91.77) * mm, "end": v(10.58, -92.06) * mm});
            skLineSegment(sketch, "E1614", {"start": v(10.58, -92.06) * mm, "end": v(10.72, -92.36) * mm});
            skLineSegment(sketch, "E1615", {"start": v(10.72, -92.36) * mm, "end": v(10.87, -92.67) * mm});
            skLineSegment(sketch, "E1616", {"start": v(10.87, -92.67) * mm, "end": v(11.02, -92.98) * mm});
            skLineSegment(sketch, "E1617", {"start": v(11.02, -92.98) * mm, "end": v(11.18, -93.31) * mm});
            skLineSegment(sketch, "E1618", {"start": v(11.18, -93.31) * mm, "end": v(11.35, -93.65) * mm});
            skLineSegment(sketch, "E1619", {"start": v(11.35, -93.65) * mm, "end": v(11.53, -94) * mm});
            skLineSegment(sketch, "E1620", {"start": v(11.53, -94) * mm, "end": v(11.72, -94.35) * mm});
            skLineSegment(sketch, "E1621", {"start": v(11.72, -94.35) * mm, "end": v(11.92, -94.7) * mm});
            skLineSegment(sketch, "E1622", {"start": v(11.92, -94.7) * mm, "end": v(12.13, -95.08) * mm});
            skLineSegment(sketch, "E1623", {"start": v(12.13, -95.08) * mm, "end": v(12.35, -95.45) * mm});
            skLineSegment(sketch, "E1624", {"start": v(12.35, -95.45) * mm, "end": v(12.58, -95.84) * mm});
            skLineSegment(sketch, "E1625", {"start": v(12.58, -95.84) * mm, "end": v(12.83, -96.23) * mm});
            skLineSegment(sketch, "E1626", {"start": v(12.83, -96.23) * mm, "end": v(13.08, -96.63) * mm});
            skLineSegment(sketch, "E1627", {"start": v(13.08, -96.63) * mm, "end": v(13.34, -97.04) * mm});
            skLineSegment(sketch, "E1628", {"start": v(13.34, -97.04) * mm, "end": v(13.62, -97.45) * mm});
            skLineSegment(sketch, "E1629", {"start": v(13.62, -97.45) * mm, "end": v(13.9, -97.87) * mm});
            skLineSegment(sketch, "E1630", {"start": v(13.9, -97.87) * mm, "end": v(14.2, -98.3) * mm});
            skLineSegment(sketch, "E1631", {"start": v(14.2, -98.3) * mm, "end": v(14.51, -98.73) * mm});
            skLineSegment(sketch, "E1632", {"start": v(14.51, -98.73) * mm, "end": v(14.84, -99.17) * mm});
            skLineSegment(sketch, "E1633", {"start": v(14.84, -99.17) * mm, "end": v(15.17, -99.61) * mm});
            skLineSegment(sketch, "E1634", {"start": v(15.17, -99.61) * mm, "end": v(15.52, -100.06) * mm});
            skLineSegment(sketch, "E1635", {"start": v(15.52, -100.06) * mm, "end": v(15.88, -100.52) * mm});
            skLineSegment(sketch, "E1636", {"start": v(15.88, -100.52) * mm, "end": v(16.25, -100.98) * mm});
            skLineSegment(sketch, "E1637", {"start": v(16.25, -100.98) * mm, "end": v(16.64, -101.44) * mm});
            skLineSegment(sketch, "E1638", {"start": v(16.64, -101.44) * mm, "end": v(17.04, -101.91) * mm});
            skLineSegment(sketch, "E1639", {"start": v(17.04, -101.91) * mm, "end": v(17.45, -102.39) * mm});
            skLineSegment(sketch, "E1640", {"start": v(17.45, -102.39) * mm, "end": v(17.88, -102.87) * mm});
            skLineSegment(sketch, "E1641", {"start": v(17.88, -102.87) * mm, "end": v(18.31, -103.35) * mm});
            skLineSegment(sketch, "E1642", {"start": v(18.31, -103.35) * mm, "end": v(18.77, -103.83) * mm});
            skLineSegment(sketch, "E1643", {"start": v(18.77, -103.83) * mm, "end": v(19.19, -104.08) * mm});
            skLineSegment(sketch, "E1644", {"start": v(19.19, -104.08) * mm, "end": v(21.5, -103.62) * mm});
            skLineSegment(sketch, "E1645", {"start": v(21.5, -103.62) * mm, "end": v(21.8, -103.24) * mm});
            skLineSegment(sketch, "E1646", {"start": v(21.8, -103.24) * mm, "end": v(22.04, -102.62) * mm});
            skLineSegment(sketch, "E1647", {"start": v(22.04, -102.62) * mm, "end": v(22.27, -102) * mm});
            skLineSegment(sketch, "E1648", {"start": v(22.27, -102) * mm, "end": v(22.48, -101.4) * mm});
            skLineSegment(sketch, "E1649", {"start": v(22.48, -101.4) * mm, "end": v(22.69, -100.8) * mm});
            skLineSegment(sketch, "E1650", {"start": v(22.69, -100.8) * mm, "end": v(22.88, -100.22) * mm});
            skLineSegment(sketch, "E1651", {"start": v(22.88, -100.22) * mm, "end": v(23.06, -99.64) * mm});
            skLineSegment(sketch, "E1652", {"start": v(23.06, -99.64) * mm, "end": v(23.23, -99.08) * mm});
            skLineSegment(sketch, "E1653", {"start": v(23.23, -99.08) * mm, "end": v(23.4, -98.52) * mm});
            skLineSegment(sketch, "E1654", {"start": v(23.4, -98.52) * mm, "end": v(23.54, -97.97) * mm});
            skLineSegment(sketch, "E1655", {"start": v(23.54, -97.97) * mm, "end": v(23.69, -97.43) * mm});
            skLineSegment(sketch, "E1656", {"start": v(23.69, -97.43) * mm, "end": v(23.82, -96.9) * mm});
            skLineSegment(sketch, "E1657", {"start": v(23.82, -96.9) * mm, "end": v(23.94, -96.39) * mm});
            skLineSegment(sketch, "E1658", {"start": v(23.94, -96.39) * mm, "end": v(24.06, -95.88) * mm});
            skLineSegment(sketch, "E1659", {"start": v(24.06, -95.88) * mm, "end": v(24.17, -95.38) * mm});
            skLineSegment(sketch, "E1660", {"start": v(24.17, -95.38) * mm, "end": v(24.27, -94.9) * mm});
            skLineSegment(sketch, "E1661", {"start": v(24.27, -94.9) * mm, "end": v(24.36, -94.42) * mm});
            skLineSegment(sketch, "E1662", {"start": v(24.36, -94.42) * mm, "end": v(24.44, -93.95) * mm});
            skLineSegment(sketch, "E1663", {"start": v(24.44, -93.95) * mm, "end": v(24.52, -93.5) * mm});
            skLineSegment(sketch, "E1664", {"start": v(24.52, -93.5) * mm, "end": v(24.59, -93.06) * mm});
            skLineSegment(sketch, "E1665", {"start": v(24.59, -93.06) * mm, "end": v(24.65, -92.62) * mm});
            skLineSegment(sketch, "E1666", {"start": v(24.65, -92.62) * mm, "end": v(24.7, -92.2) * mm});
            skLineSegment(sketch, "E1667", {"start": v(24.7, -92.2) * mm, "end": v(24.75, -91.8) * mm});
            skLineSegment(sketch, "E1668", {"start": v(24.75, -91.8) * mm, "end": v(24.8, -91.4) * mm});
            skLineSegment(sketch, "E1669", {"start": v(24.8, -91.4) * mm, "end": v(24.83, -91) * mm});
            skLineSegment(sketch, "E1670", {"start": v(24.83, -91) * mm, "end": v(24.86, -90.63) * mm});
            skLineSegment(sketch, "E1671", {"start": v(24.86, -90.63) * mm, "end": v(24.9, -90.27) * mm});
            skLineSegment(sketch, "E1672", {"start": v(24.9, -90.27) * mm, "end": v(24.91, -89.91) * mm});
            skLineSegment(sketch, "E1673", {"start": v(24.91, -89.91) * mm, "end": v(24.93, -89.57) * mm});
            skLineSegment(sketch, "E1674", {"start": v(24.93, -89.57) * mm, "end": v(24.94, -89.24) * mm});
            skLineSegment(sketch, "E1675", {"start": v(24.94, -89.24) * mm, "end": v(24.95, -88.93) * mm});
            skLineSegment(sketch, "E1676", {"start": v(24.95, -88.93) * mm, "end": v(24.95, -88.62) * mm});
            skLineSegment(sketch, "E1677", {"start": v(24.95, -88.62) * mm, "end": v(24.95, -88.33) * mm});
            skLineSegment(sketch, "E1678", {"start": v(24.95, -88.33) * mm, "end": v(25.52, -87.99) * mm});
            skLineSegment(sketch, "E1679", {"start": v(25.52, -87.99) * mm, "end": v(28.3, -87.13) * mm});
            skLineSegment(sketch, "E1680", {"start": v(28.3, -87.13) * mm, "end": v(28.97, -87.1) * mm});
            skLineSegment(sketch, "E1681", {"start": v(28.97, -87.1) * mm, "end": v(29.13, -87.34) * mm});
            skLineSegment(sketch, "E1682", {"start": v(29.13, -87.34) * mm, "end": v(29.3, -87.59) * mm});
            skLineSegment(sketch, "E1683", {"start": v(29.3, -87.59) * mm, "end": v(29.5, -87.85) * mm});
            skLineSegment(sketch, "E1684", {"start": v(29.5, -87.85) * mm, "end": v(29.69, -88.11) * mm});
            skLineSegment(sketch, "E1685", {"start": v(29.69, -88.11) * mm, "end": v(29.9, -88.38) * mm});
            skLineSegment(sketch, "E1686", {"start": v(29.9, -88.38) * mm, "end": v(30.11, -88.66) * mm});
            skLineSegment(sketch, "E1687", {"start": v(30.11, -88.66) * mm, "end": v(30.34, -88.95) * mm});
            skLineSegment(sketch, "E1688", {"start": v(30.34, -88.95) * mm, "end": v(30.57, -89.24) * mm});
            skLineSegment(sketch, "E1689", {"start": v(30.57, -89.24) * mm, "end": v(30.82, -89.54) * mm});
            skLineSegment(sketch, "E1690", {"start": v(30.82, -89.54) * mm, "end": v(31.08, -89.85) * mm});
            skLineSegment(sketch, "E1691", {"start": v(31.08, -89.85) * mm, "end": v(31.35, -90.16) * mm});
            skLineSegment(sketch, "E1692", {"start": v(31.35, -90.16) * mm, "end": v(31.63, -90.48) * mm});
            skLineSegment(sketch, "E1693", {"start": v(31.63, -90.48) * mm, "end": v(31.93, -90.8) * mm});
            skLineSegment(sketch, "E1694", {"start": v(31.93, -90.8) * mm, "end": v(32.23, -91.13) * mm});
            skLineSegment(sketch, "E1695", {"start": v(32.23, -91.13) * mm, "end": v(32.55, -91.46) * mm});
            skLineSegment(sketch, "E1696", {"start": v(32.55, -91.46) * mm, "end": v(32.88, -91.8) * mm});
            skLineSegment(sketch, "E1697", {"start": v(32.88, -91.8) * mm, "end": v(33.23, -92.14) * mm});
            skLineSegment(sketch, "E1698", {"start": v(33.23, -92.14) * mm, "end": v(33.58, -92.49) * mm});
            skLineSegment(sketch, "E1699", {"start": v(33.58, -92.49) * mm, "end": v(33.95, -92.84) * mm});
            skLineSegment(sketch, "E1700", {"start": v(33.95, -92.84) * mm, "end": v(34.33, -93.2) * mm});
            skLineSegment(sketch, "E1701", {"start": v(34.33, -93.2) * mm, "end": v(34.72, -93.55) * mm});
            skLineSegment(sketch, "E1702", {"start": v(34.72, -93.55) * mm, "end": v(35.13, -93.91) * mm});
            skLineSegment(sketch, "E1703", {"start": v(35.13, -93.91) * mm, "end": v(35.55, -94.28) * mm});
            skLineSegment(sketch, "E1704", {"start": v(35.55, -94.28) * mm, "end": v(35.98, -94.65) * mm});
            skLineSegment(sketch, "E1705", {"start": v(35.98, -94.65) * mm, "end": v(36.43, -95.02) * mm});
            skLineSegment(sketch, "E1706", {"start": v(36.43, -95.02) * mm, "end": v(36.9, -95.4) * mm});
            skLineSegment(sketch, "E1707", {"start": v(36.9, -95.4) * mm, "end": v(37.37, -95.77) * mm});
            skLineSegment(sketch, "E1708", {"start": v(37.37, -95.77) * mm, "end": v(37.85, -96.14) * mm});
            skLineSegment(sketch, "E1709", {"start": v(37.85, -96.14) * mm, "end": v(38.36, -96.52) * mm});
            skLineSegment(sketch, "E1710", {"start": v(38.36, -96.52) * mm, "end": v(38.87, -96.9) * mm});
            skLineSegment(sketch, "E1711", {"start": v(38.87, -96.9) * mm, "end": v(39.4, -97.28) * mm});
            skLineSegment(sketch, "E1712", {"start": v(39.4, -97.28) * mm, "end": v(39.95, -97.66) * mm});
            skLineSegment(sketch, "E1713", {"start": v(39.95, -97.66) * mm, "end": v(40.4, -97.81) * mm});
            skLineSegment(sketch, "E1714", {"start": v(40.4, -97.81) * mm, "end": v(42.58, -96.89) * mm});
            skLineSegment(sketch, "E1715", {"start": v(42.58, -96.89) * mm, "end": v(42.8, -96.45) * mm});
            skLineSegment(sketch, "E1716", {"start": v(42.8, -96.45) * mm, "end": v(42.9, -95.8) * mm});
            skLineSegment(sketch, "E1717", {"start": v(42.9, -95.8) * mm, "end": v(42.99, -95.15) * mm});
            skLineSegment(sketch, "E1718", {"start": v(42.99, -95.15) * mm, "end": v(43.07, -94.5) * mm});
            skLineSegment(sketch, "E1719", {"start": v(43.07, -94.5) * mm, "end": v(43.15, -93.89) * mm});
            skLineSegment(sketch, "E1720", {"start": v(43.15, -93.89) * mm, "end": v(43.21, -93.27) * mm});
            skLineSegment(sketch, "E1721", {"start": v(43.21, -93.27) * mm, "end": v(43.27, -92.67) * mm});
            skLineSegment(sketch, "E1722", {"start": v(43.27, -92.67) * mm, "end": v(43.32, -92.08) * mm});
            skLineSegment(sketch, "E1723", {"start": v(43.32, -92.08) * mm, "end": v(43.36, -91.5) * mm});
            skLineSegment(sketch, "E1724", {"start": v(43.36, -91.5) * mm, "end": v(43.4, -90.94) * mm});
            skLineSegment(sketch, "E1725", {"start": v(43.4, -90.94) * mm, "end": v(43.43, -90.38) * mm});
            skLineSegment(sketch, "E1726", {"start": v(43.43, -90.38) * mm, "end": v(43.45, -89.84) * mm});
            skLineSegment(sketch, "E1727", {"start": v(43.45, -89.84) * mm, "end": v(43.46, -89.3) * mm});
            skLineSegment(sketch, "E1728", {"start": v(43.46, -89.3) * mm, "end": v(43.47, -88.78) * mm});
            skLineSegment(sketch, "E1729", {"start": v(43.47, -88.78) * mm, "end": v(43.47, -88.27) * mm});
            skLineSegment(sketch, "E1730", {"start": v(43.47, -88.27) * mm, "end": v(43.46, -87.78) * mm});
            skLineSegment(sketch, "E1731", {"start": v(43.46, -87.78) * mm, "end": v(43.46, -87.3) * mm});
            skLineSegment(sketch, "E1732", {"start": v(43.46, -87.3) * mm, "end": v(43.44, -86.82) * mm});
            skLineSegment(sketch, "E1733", {"start": v(43.44, -86.82) * mm, "end": v(43.42, -86.36) * mm});
            skLineSegment(sketch, "E1734", {"start": v(43.42, -86.36) * mm, "end": v(43.4, -85.91) * mm});
            skLineSegment(sketch, "E1735", {"start": v(43.4, -85.91) * mm, "end": v(43.37, -85.48) * mm});
            skLineSegment(sketch, "E1736", {"start": v(43.37, -85.48) * mm, "end": v(43.33, -85.05) * mm});
            skLineSegment(sketch, "E1737", {"start": v(43.33, -85.05) * mm, "end": v(43.3, -84.64) * mm});
            skLineSegment(sketch, "E1738", {"start": v(43.3, -84.64) * mm, "end": v(43.26, -84.24) * mm});
            skLineSegment(sketch, "E1739", {"start": v(43.26, -84.24) * mm, "end": v(43.21, -83.86) * mm});
            skLineSegment(sketch, "E1740", {"start": v(43.21, -83.86) * mm, "end": v(43.16, -83.48) * mm});
            skLineSegment(sketch, "E1741", {"start": v(43.16, -83.48) * mm, "end": v(43.11, -83.12) * mm});
            skLineSegment(sketch, "E1742", {"start": v(43.11, -83.12) * mm, "end": v(43.06, -82.77) * mm});
            skLineSegment(sketch, "E1743", {"start": v(43.06, -82.77) * mm, "end": v(43, -82.43) * mm});
            skLineSegment(sketch, "E1744", {"start": v(43, -82.43) * mm, "end": v(42.95, -82.1) * mm});
            skLineSegment(sketch, "E1745", {"start": v(42.95, -82.1) * mm, "end": v(42.9, -81.8) * mm});
            skLineSegment(sketch, "E1746", {"start": v(42.9, -81.8) * mm, "end": v(42.83, -81.5) * mm});
            skLineSegment(sketch, "E1747", {"start": v(42.83, -81.5) * mm, "end": v(42.77, -81.21) * mm});
            skLineSegment(sketch, "E1748", {"start": v(42.77, -81.21) * mm, "end": v(43.25, -80.76) * mm});
            skLineSegment(sketch, "E1749", {"start": v(43.25, -80.76) * mm, "end": v(45.8, -79.34) * mm});
            skLineSegment(sketch, "E1750", {"start": v(45.8, -79.34) * mm, "end": v(46.44, -79.17) * mm});
            skLineSegment(sketch, "E1751", {"start": v(46.44, -79.17) * mm, "end": v(46.66, -79.37) * mm});
            skLineSegment(sketch, "E1752", {"start": v(46.66, -79.37) * mm, "end": v(46.88, -79.58) * mm});
            skLineSegment(sketch, "E1753", {"start": v(46.88, -79.58) * mm, "end": v(47.11, -79.8) * mm});
            skLineSegment(sketch, "E1754", {"start": v(47.11, -79.8) * mm, "end": v(47.36, -80.01) * mm});
            skLineSegment(sketch, "E1755", {"start": v(47.36, -80.01) * mm, "end": v(47.62, -80.24) * mm});
            skLineSegment(sketch, "E1756", {"start": v(47.62, -80.24) * mm, "end": v(47.89, -80.47) * mm});
            skLineSegment(sketch, "E1757", {"start": v(47.89, -80.47) * mm, "end": v(48.17, -80.7) * mm});
            skLineSegment(sketch, "E1758", {"start": v(48.17, -80.7) * mm, "end": v(48.46, -80.93) * mm});
            skLineSegment(sketch, "E1759", {"start": v(48.46, -80.93) * mm, "end": v(48.76, -81.18) * mm});
            skLineSegment(sketch, "E1760", {"start": v(48.76, -81.18) * mm, "end": v(49.08, -81.42) * mm});
            skLineSegment(sketch, "E1761", {"start": v(49.08, -81.42) * mm, "end": v(49.41, -81.67) * mm});
            skLineSegment(sketch, "E1762", {"start": v(49.41, -81.67) * mm, "end": v(49.75, -81.92) * mm});
            skLineSegment(sketch, "E1763", {"start": v(49.75, -81.92) * mm, "end": v(50.1, -82.18) * mm});
            skLineSegment(sketch, "E1764", {"start": v(50.1, -82.18) * mm, "end": v(50.48, -82.43) * mm});
            skLineSegment(sketch, "E1765", {"start": v(50.48, -82.43) * mm, "end": v(50.86, -82.7) * mm});
            skLineSegment(sketch, "E1766", {"start": v(50.86, -82.7) * mm, "end": v(51.25, -82.96) * mm});
            skLineSegment(sketch, "E1767", {"start": v(51.25, -82.96) * mm, "end": v(51.66, -83.22) * mm});
            skLineSegment(sketch, "E1768", {"start": v(51.66, -83.22) * mm, "end": v(52.08, -83.49) * mm});
            skLineSegment(sketch, "E1769", {"start": v(52.08, -83.49) * mm, "end": v(52.51, -83.75) * mm});
            skLineSegment(sketch, "E1770", {"start": v(52.51, -83.75) * mm, "end": v(52.96, -84.02) * mm});
            skLineSegment(sketch, "E1771", {"start": v(52.96, -84.02) * mm, "end": v(53.42, -84.29) * mm});
            skLineSegment(sketch, "E1772", {"start": v(53.42, -84.29) * mm, "end": v(53.89, -84.56) * mm});
            skLineSegment(sketch, "E1773", {"start": v(53.89, -84.56) * mm, "end": v(54.38, -84.83) * mm});
            skLineSegment(sketch, "E1774", {"start": v(54.38, -84.83) * mm, "end": v(54.88, -85.1) * mm});
            skLineSegment(sketch, "E1775", {"start": v(54.88, -85.1) * mm, "end": v(55.4, -85.37) * mm});
            skLineSegment(sketch, "E1776", {"start": v(55.4, -85.37) * mm, "end": v(55.92, -85.64) * mm});
            skLineSegment(sketch, "E1777", {"start": v(55.92, -85.64) * mm, "end": v(56.46, -85.9) * mm});
            skLineSegment(sketch, "E1778", {"start": v(56.46, -85.9) * mm, "end": v(57.02, -86.17) * mm});
            skLineSegment(sketch, "E1779", {"start": v(57.02, -86.17) * mm, "end": v(57.59, -86.44) * mm});
            skLineSegment(sketch, "E1780", {"start": v(57.59, -86.44) * mm, "end": v(58.17, -86.7) * mm});
            skLineSegment(sketch, "E1781", {"start": v(58.17, -86.7) * mm, "end": v(58.77, -86.96) * mm});
            skLineSegment(sketch, "E1782", {"start": v(58.77, -86.96) * mm, "end": v(59.38, -87.22) * mm});
            skLineSegment(sketch, "E1783", {"start": v(59.38, -87.22) * mm, "end": v(59.86, -87.28) * mm});
            skLineSegment(sketch, "E1784", {"start": v(59.86, -87.28) * mm, "end": v(61.8, -85.92) * mm});
            skLineSegment(sketch, "E1785", {"start": v(61.8, -85.92) * mm, "end": v(61.91, -85.44) * mm});
            skLineSegment(sketch, "E1786", {"start": v(61.91, -85.44) * mm, "end": v(61.88, -84.78) * mm});
            skLineSegment(sketch, "E1787", {"start": v(61.88, -84.78) * mm, "end": v(61.83, -84.13) * mm});
            skLineSegment(sketch, "E1788", {"start": v(61.83, -84.13) * mm, "end": v(61.78, -83.49) * mm});
            skLineSegment(sketch, "E1789", {"start": v(61.78, -83.49) * mm, "end": v(61.73, -82.86) * mm});
            skLineSegment(sketch, "E1790", {"start": v(61.73, -82.86) * mm, "end": v(61.66, -82.25) * mm});
            skLineSegment(sketch, "E1791", {"start": v(61.66, -82.25) * mm, "end": v(61.6, -81.65) * mm});
            skLineSegment(sketch, "E1792", {"start": v(61.6, -81.65) * mm, "end": v(61.52, -81.06) * mm});
            skLineSegment(sketch, "E1793", {"start": v(61.52, -81.06) * mm, "end": v(61.44, -80.49) * mm});
            skLineSegment(sketch, "E1794", {"start": v(61.44, -80.49) * mm, "end": v(61.36, -79.92) * mm});
            skLineSegment(sketch, "E1795", {"start": v(61.36, -79.92) * mm, "end": v(61.27, -79.37) * mm});
            skLineSegment(sketch, "E1796", {"start": v(61.27, -79.37) * mm, "end": v(61.18, -78.84) * mm});
            skLineSegment(sketch, "E1797", {"start": v(61.18, -78.84) * mm, "end": v(61.08, -78.32) * mm});
            skLineSegment(sketch, "E1798", {"start": v(61.08, -78.32) * mm, "end": v(60.98, -77.8) * mm});
            skLineSegment(sketch, "E1799", {"start": v(60.98, -77.8) * mm, "end": v(60.87, -77.3) * mm});
            skLineSegment(sketch, "E1800", {"start": v(60.87, -77.3) * mm, "end": v(60.77, -76.82) * mm});
            skLineSegment(sketch, "E1801", {"start": v(60.77, -76.82) * mm, "end": v(60.65, -76.35) * mm});
            skLineSegment(sketch, "E1802", {"start": v(60.65, -76.35) * mm, "end": v(60.54, -75.9) * mm});
            skLineSegment(sketch, "E1803", {"start": v(60.54, -75.9) * mm, "end": v(60.43, -75.44) * mm});
            skLineSegment(sketch, "E1804", {"start": v(60.43, -75.44) * mm, "end": v(60.3, -75.01) * mm});
            skLineSegment(sketch, "E1805", {"start": v(60.3, -75.01) * mm, "end": v(60.19, -74.6) * mm});
            skLineSegment(sketch, "E1806", {"start": v(60.19, -74.6) * mm, "end": v(60.07, -74.18) * mm});
            skLineSegment(sketch, "E1807", {"start": v(60.07, -74.18) * mm, "end": v(59.95, -73.79) * mm});
            skLineSegment(sketch, "E1808", {"start": v(59.95, -73.79) * mm, "end": v(59.82, -73.4) * mm});
            skLineSegment(sketch, "E1809", {"start": v(59.82, -73.4) * mm, "end": v(59.7, -73.04) * mm});
            skLineSegment(sketch, "E1810", {"start": v(59.7, -73.04) * mm, "end": v(59.58, -72.68) * mm});
            skLineSegment(sketch, "E1811", {"start": v(59.58, -72.68) * mm, "end": v(59.45, -72.34) * mm});
            skLineSegment(sketch, "E1812", {"start": v(59.45, -72.34) * mm, "end": v(59.33, -72) * mm});
            skLineSegment(sketch, "E1813", {"start": v(59.33, -72) * mm, "end": v(59.2, -71.7) * mm});
            skLineSegment(sketch, "E1814", {"start": v(59.2, -71.7) * mm, "end": v(59.08, -71.39) * mm});
            skLineSegment(sketch, "E1815", {"start": v(59.08, -71.39) * mm, "end": v(58.96, -71.1) * mm});
            skLineSegment(sketch, "E1816", {"start": v(58.96, -71.1) * mm, "end": v(58.84, -70.81) * mm});
            skLineSegment(sketch, "E1817", {"start": v(58.84, -70.81) * mm, "end": v(58.72, -70.54) * mm});
            skLineSegment(sketch, "E1818", {"start": v(58.72, -70.54) * mm, "end": v(59.1, -70) * mm});
            skLineSegment(sketch, "E1819", {"start": v(59.1, -70) * mm, "end": v(61.3, -68.08) * mm});
            skLineSegment(sketch, "E1820", {"start": v(61.3, -68.08) * mm, "end": v(61.89, -67.78) * mm});
            skLineSegment(sketch, "E1821", {"start": v(61.89, -67.78) * mm, "end": v(62.14, -67.94) * mm});
            skLineSegment(sketch, "E1822", {"start": v(62.14, -67.94) * mm, "end": v(62.4, -68.1) * mm});
            skLineSegment(sketch, "E1823", {"start": v(62.4, -68.1) * mm, "end": v(62.67, -68.25) * mm});
            skLineSegment(sketch, "E1824", {"start": v(62.67, -68.25) * mm, "end": v(62.96, -68.42) * mm});
            skLineSegment(sketch, "E1825", {"start": v(62.96, -68.42) * mm, "end": v(63.26, -68.58) * mm});
            skLineSegment(sketch, "E1826", {"start": v(63.26, -68.58) * mm, "end": v(63.57, -68.75) * mm});
            skLineSegment(sketch, "E1827", {"start": v(63.57, -68.75) * mm, "end": v(63.9, -68.92) * mm});
            skLineSegment(sketch, "E1828", {"start": v(63.9, -68.92) * mm, "end": v(64.23, -69.1) * mm});
            skLineSegment(sketch, "E1829", {"start": v(64.23, -69.1) * mm, "end": v(64.58, -69.26) * mm});
            skLineSegment(sketch, "E1830", {"start": v(64.58, -69.26) * mm, "end": v(64.94, -69.44) * mm});
            skLineSegment(sketch, "E1831", {"start": v(64.94, -69.44) * mm, "end": v(65.31, -69.61) * mm});
            skLineSegment(sketch, "E1832", {"start": v(65.31, -69.61) * mm, "end": v(65.7, -69.79) * mm});
            skLineSegment(sketch, "E1833", {"start": v(65.7, -69.79) * mm, "end": v(66.1, -69.96) * mm});
            skLineSegment(sketch, "E1834", {"start": v(66.1, -69.96) * mm, "end": v(66.51, -70.14) * mm});
            skLineSegment(sketch, "E1835", {"start": v(66.51, -70.14) * mm, "end": v(66.94, -70.31) * mm});
            skLineSegment(sketch, "E1836", {"start": v(66.94, -70.31) * mm, "end": v(67.38, -70.49) * mm});
            skLineSegment(sketch, "E1837", {"start": v(67.38, -70.49) * mm, "end": v(67.83, -70.66) * mm});
            skLineSegment(sketch, "E1838", {"start": v(67.83, -70.66) * mm, "end": v(68.3, -70.83) * mm});
            skLineSegment(sketch, "E1839", {"start": v(68.3, -70.83) * mm, "end": v(68.78, -71) * mm});
            skLineSegment(sketch, "E1840", {"start": v(68.78, -71) * mm, "end": v(69.27, -71.17) * mm});
            skLineSegment(sketch, "E1841", {"start": v(69.27, -71.17) * mm, "end": v(69.77, -71.34) * mm});
            skLineSegment(sketch, "E1842", {"start": v(69.77, -71.34) * mm, "end": v(70.3, -71.5) * mm});
            skLineSegment(sketch, "E1843", {"start": v(70.3, -71.5) * mm, "end": v(70.82, -71.67) * mm});
            skLineSegment(sketch, "E1844", {"start": v(70.82, -71.67) * mm, "end": v(71.37, -71.83) * mm});
            skLineSegment(sketch, "E1845", {"start": v(71.37, -71.83) * mm, "end": v(71.93, -71.99) * mm});
            skLineSegment(sketch, "E1846", {"start": v(71.93, -71.99) * mm, "end": v(72.5, -72.14) * mm});
            skLineSegment(sketch, "E1847", {"start": v(72.5, -72.14) * mm, "end": v(73.09, -72.29) * mm});
            skLineSegment(sketch, "E1848", {"start": v(73.09, -72.29) * mm, "end": v(73.69, -72.44) * mm});
            skLineSegment(sketch, "E1849", {"start": v(73.69, -72.44) * mm, "end": v(74.3, -72.58) * mm});
            skLineSegment(sketch, "E1850", {"start": v(74.3, -72.58) * mm, "end": v(74.92, -72.71) * mm});
            skLineSegment(sketch, "E1851", {"start": v(74.92, -72.71) * mm, "end": v(75.56, -72.84) * mm});
            skLineSegment(sketch, "E1852", {"start": v(75.56, -72.84) * mm, "end": v(76.21, -72.97) * mm});
            skLineSegment(sketch, "E1853", {"start": v(76.21, -72.97) * mm, "end": v(76.7, -72.92) * mm});
            skLineSegment(sketch, "E1854", {"start": v(76.7, -72.92) * mm, "end": v(78.31, -71.2) * mm});
            skLineSegment(sketch, "E1855", {"start": v(78.31, -71.2) * mm, "end": v(78.32, -70.7) * mm});
            skLineSegment(sketch, "E1856", {"start": v(78.32, -70.7) * mm, "end": v(78.15, -70.06) * mm});
            skLineSegment(sketch, "E1857", {"start": v(78.15, -70.06) * mm, "end": v(77.97, -69.43) * mm});
            skLineSegment(sketch, "E1858", {"start": v(77.97, -69.43) * mm, "end": v(77.8, -68.82) * mm});
            skLineSegment(sketch, "E1859", {"start": v(77.8, -68.82) * mm, "end": v(77.6, -68.22) * mm});
            skLineSegment(sketch, "E1860", {"start": v(77.6, -68.22) * mm, "end": v(77.42, -67.63) * mm});
            skLineSegment(sketch, "E1861", {"start": v(77.42, -67.63) * mm, "end": v(77.22, -67.06) * mm});
            skLineSegment(sketch, "E1862", {"start": v(77.22, -67.06) * mm, "end": v(77.03, -66.5) * mm});
            skLineSegment(sketch, "E1863", {"start": v(77.03, -66.5) * mm, "end": v(76.83, -65.95) * mm});
            skLineSegment(sketch, "E1864", {"start": v(76.83, -65.95) * mm, "end": v(76.63, -65.42) * mm});
            skLineSegment(sketch, "E1865", {"start": v(76.63, -65.42) * mm, "end": v(76.43, -64.9) * mm});
            skLineSegment(sketch, "E1866", {"start": v(76.43, -64.9) * mm, "end": v(76.23, -64.4) * mm});
            skLineSegment(sketch, "E1867", {"start": v(76.23, -64.4) * mm, "end": v(76.03, -63.9) * mm});
            skLineSegment(sketch, "E1868", {"start": v(76.03, -63.9) * mm, "end": v(75.82, -63.43) * mm});
            skLineSegment(sketch, "E1869", {"start": v(75.82, -63.43) * mm, "end": v(75.62, -62.96) * mm});
            skLineSegment(sketch, "E1870", {"start": v(75.62, -62.96) * mm, "end": v(75.4, -62.5) * mm});
            skLineSegment(sketch, "E1871", {"start": v(75.4, -62.5) * mm, "end": v(75.2, -62.07) * mm});
            skLineSegment(sketch, "E1872", {"start": v(75.2, -62.07) * mm, "end": v(75, -61.65) * mm});
            skLineSegment(sketch, "E1873", {"start": v(75, -61.65) * mm, "end": v(74.8, -61.23) * mm});
            skLineSegment(sketch, "E1874", {"start": v(74.8, -61.23) * mm, "end": v(74.59, -60.83) * mm});
            skLineSegment(sketch, "E1875", {"start": v(74.59, -60.83) * mm, "end": v(74.38, -60.45) * mm});
            skLineSegment(sketch, "E1876", {"start": v(74.38, -60.45) * mm, "end": v(74.18, -60.07) * mm});
            skLineSegment(sketch, "E1877", {"start": v(74.18, -60.07) * mm, "end": v(73.98, -59.71) * mm});
            skLineSegment(sketch, "E1878", {"start": v(73.98, -59.71) * mm, "end": v(73.78, -59.37) * mm});
            skLineSegment(sketch, "E1879", {"start": v(73.78, -59.37) * mm, "end": v(73.58, -59.03) * mm});
            skLineSegment(sketch, "E1880", {"start": v(73.58, -59.03) * mm, "end": v(73.39, -58.7) * mm});
            skLineSegment(sketch, "E1881", {"start": v(73.39, -58.7) * mm, "end": v(73.2, -58.4) * mm});
            skLineSegment(sketch, "E1882", {"start": v(73.2, -58.4) * mm, "end": v(73, -58.1) * mm});
            skLineSegment(sketch, "E1883", {"start": v(73, -58.1) * mm, "end": v(72.82, -57.81) * mm});
            skLineSegment(sketch, "E1884", {"start": v(72.82, -57.81) * mm, "end": v(72.64, -57.54) * mm});
            skLineSegment(sketch, "E1885", {"start": v(72.64, -57.54) * mm, "end": v(72.45, -57.28) * mm});
            skLineSegment(sketch, "E1886", {"start": v(72.45, -57.28) * mm, "end": v(72.28, -57.03) * mm});
            skLineSegment(sketch, "E1887", {"start": v(72.28, -57.03) * mm, "end": v(72.1, -56.8) * mm});
            skLineSegment(sketch, "E1888", {"start": v(72.1, -56.8) * mm, "end": v(72.36, -56.18) * mm});
            skLineSegment(sketch, "E1889", {"start": v(72.36, -56.18) * mm, "end": v(74.11, -53.85) * mm});
            skLineSegment(sketch, "E1890", {"start": v(74.11, -53.85) * mm, "end": v(74.63, -53.43) * mm});
            skLineSegment(sketch, "E1891", {"start": v(74.63, -53.43) * mm, "end": v(74.9, -53.53) * mm});
            skLineSegment(sketch, "E1892", {"start": v(74.9, -53.53) * mm, "end": v(75.2, -53.63) * mm});
            skLineSegment(sketch, "E1893", {"start": v(75.2, -53.63) * mm, "end": v(75.5, -53.73) * mm});
            skLineSegment(sketch, "E1894", {"start": v(75.5, -53.73) * mm, "end": v(75.8, -53.83) * mm});
            skLineSegment(sketch, "E1895", {"start": v(75.8, -53.83) * mm, "end": v(76.13, -53.93) * mm});
            skLineSegment(sketch, "E1896", {"start": v(76.13, -53.93) * mm, "end": v(76.47, -54.03) * mm});
            skLineSegment(sketch, "E1897", {"start": v(76.47, -54.03) * mm, "end": v(76.83, -54.13) * mm});
            skLineSegment(sketch, "E1898", {"start": v(76.83, -54.13) * mm, "end": v(77.19, -54.23) * mm});
            skLineSegment(sketch, "E1899", {"start": v(77.19, -54.23) * mm, "end": v(77.57, -54.32) * mm});
            skLineSegment(sketch, "E1900", {"start": v(77.57, -54.32) * mm, "end": v(77.96, -54.42) * mm});
            skLineSegment(sketch, "E1901", {"start": v(77.96, -54.42) * mm, "end": v(78.36, -54.51) * mm});
            skLineSegment(sketch, "E1902", {"start": v(78.36, -54.51) * mm, "end": v(78.77, -54.6) * mm});
            skLineSegment(sketch, "E1903", {"start": v(78.77, -54.6) * mm, "end": v(79.2, -54.7) * mm});
            skLineSegment(sketch, "E1904", {"start": v(79.2, -54.7) * mm, "end": v(79.64, -54.78) * mm});
            skLineSegment(sketch, "E1905", {"start": v(79.64, -54.78) * mm, "end": v(80.1, -54.86) * mm});
            skLineSegment(sketch, "E1906", {"start": v(80.1, -54.86) * mm, "end": v(80.56, -54.94) * mm});
            skLineSegment(sketch, "E1907", {"start": v(80.56, -54.94) * mm, "end": v(81.04, -55.01) * mm});
            skLineSegment(sketch, "E1908", {"start": v(81.04, -55.01) * mm, "end": v(81.53, -55.09) * mm});
            skLineSegment(sketch, "E1909", {"start": v(81.53, -55.09) * mm, "end": v(82.04, -55.15) * mm});
            skLineSegment(sketch, "E1910", {"start": v(82.04, -55.15) * mm, "end": v(82.55, -55.22) * mm});
            skLineSegment(sketch, "E1911", {"start": v(82.55, -55.22) * mm, "end": v(83.08, -55.28) * mm});
            skLineSegment(sketch, "E1912", {"start": v(83.08, -55.28) * mm, "end": v(83.62, -55.33) * mm});
            skLineSegment(sketch, "E1913", {"start": v(83.62, -55.33) * mm, "end": v(84.18, -55.38) * mm});
            skLineSegment(sketch, "E1914", {"start": v(84.18, -55.38) * mm, "end": v(84.75, -55.42) * mm});
            skLineSegment(sketch, "E1915", {"start": v(84.75, -55.42) * mm, "end": v(85.32, -55.46) * mm});
            skLineSegment(sketch, "E1916", {"start": v(85.32, -55.46) * mm, "end": v(85.92, -55.49) * mm});
            skLineSegment(sketch, "E1917", {"start": v(85.92, -55.49) * mm, "end": v(86.52, -55.51) * mm});
            skLineSegment(sketch, "E1918", {"start": v(86.52, -55.51) * mm, "end": v(87.14, -55.53) * mm});
            skLineSegment(sketch, "E1919", {"start": v(87.14, -55.53) * mm, "end": v(87.76, -55.54) * mm});
            skLineSegment(sketch, "E1920", {"start": v(87.76, -55.54) * mm, "end": v(88.4, -55.55) * mm});
            skLineSegment(sketch, "E1921", {"start": v(88.4, -55.55) * mm, "end": v(89.06, -55.54) * mm});
            skLineSegment(sketch, "E1922", {"start": v(89.06, -55.54) * mm, "end": v(89.72, -55.53) * mm});
            skLineSegment(sketch, "E1923", {"start": v(89.72, -55.53) * mm, "end": v(90.19, -55.38) * mm});
            skLineSegment(sketch, "E1924", {"start": v(90.19, -55.38) * mm, "end": v(91.4, -53.35) * mm});
            skLineSegment(sketch, "E1925", {"start": v(91.4, -53.35) * mm, "end": v(91.31, -52.87) * mm});
            skLineSegment(sketch, "E1926", {"start": v(91.31, -52.87) * mm, "end": v(91, -52.28) * mm});
            skLineSegment(sketch, "E1927", {"start": v(91, -52.28) * mm, "end": v(90.7, -51.7) * mm});
            skLineSegment(sketch, "E1928", {"start": v(90.7, -51.7) * mm, "end": v(90.4, -51.14) * mm});
            skLineSegment(sketch, "E1929", {"start": v(90.4, -51.14) * mm, "end": v(90.1, -50.6) * mm});
            skLineSegment(sketch, "E1930", {"start": v(90.1, -50.6) * mm, "end": v(89.79, -50.06) * mm});
            skLineSegment(sketch, "E1931", {"start": v(89.79, -50.06) * mm, "end": v(89.48, -49.54) * mm});
            skLineSegment(sketch, "E1932", {"start": v(89.48, -49.54) * mm, "end": v(89.17, -49.03) * mm});
            skLineSegment(sketch, "E1933", {"start": v(89.17, -49.03) * mm, "end": v(88.87, -48.54) * mm});
            skLineSegment(sketch, "E1934", {"start": v(88.87, -48.54) * mm, "end": v(88.56, -48.06) * mm});
            skLineSegment(sketch, "E1935", {"start": v(88.56, -48.06) * mm, "end": v(88.26, -47.6) * mm});
            skLineSegment(sketch, "E1936", {"start": v(88.26, -47.6) * mm, "end": v(87.95, -47.14) * mm});
            skLineSegment(sketch, "E1937", {"start": v(87.95, -47.14) * mm, "end": v(87.65, -46.7) * mm});
            skLineSegment(sketch, "E1938", {"start": v(87.65, -46.7) * mm, "end": v(87.35, -46.28) * mm});
            skLineSegment(sketch, "E1939", {"start": v(87.35, -46.28) * mm, "end": v(87.05, -45.86) * mm});
            skLineSegment(sketch, "E1940", {"start": v(87.05, -45.86) * mm, "end": v(86.76, -45.46) * mm});
            skLineSegment(sketch, "E1941", {"start": v(86.76, -45.46) * mm, "end": v(86.47, -45.08) * mm});
            skLineSegment(sketch, "E1942", {"start": v(86.47, -45.08) * mm, "end": v(86.18, -44.7) * mm});
            skLineSegment(sketch, "E1943", {"start": v(86.18, -44.7) * mm, "end": v(85.89, -44.34) * mm});
            skLineSegment(sketch, "E1944", {"start": v(85.89, -44.34) * mm, "end": v(85.6, -44) * mm});
            skLineSegment(sketch, "E1945", {"start": v(85.6, -44) * mm, "end": v(85.33, -43.66) * mm});
            skLineSegment(sketch, "E1946", {"start": v(85.33, -43.66) * mm, "end": v(85.05, -43.34) * mm});
            skLineSegment(sketch, "E1947", {"start": v(85.05, -43.34) * mm, "end": v(84.78, -43.03) * mm});
            skLineSegment(sketch, "E1948", {"start": v(84.78, -43.03) * mm, "end": v(84.5, -42.73) * mm});
            skLineSegment(sketch, "E1949", {"start": v(84.5, -42.73) * mm, "end": v(84.25, -42.44) * mm});
            skLineSegment(sketch, "E1950", {"start": v(84.25, -42.44) * mm, "end": v(83.99, -42.17) * mm});
            skLineSegment(sketch, "E1951", {"start": v(83.99, -42.17) * mm, "end": v(83.74, -41.9) * mm});
            skLineSegment(sketch, "E1952", {"start": v(83.74, -41.9) * mm, "end": v(83.49, -41.65) * mm});
            skLineSegment(sketch, "E1953", {"start": v(83.49, -41.65) * mm, "end": v(83.25, -41.41) * mm});
            skLineSegment(sketch, "E1954", {"start": v(83.25, -41.41) * mm, "end": v(83.01, -41.18) * mm});
            skLineSegment(sketch, "E1955", {"start": v(83.01, -41.18) * mm, "end": v(82.78, -40.96) * mm});
            skLineSegment(sketch, "E1956", {"start": v(82.78, -40.96) * mm, "end": v(82.56, -40.76) * mm});
            skLineSegment(sketch, "E1957", {"start": v(82.56, -40.76) * mm, "end": v(82.34, -40.56) * mm});
            skLineSegment(sketch, "E1958", {"start": v(82.34, -40.56) * mm, "end": v(82.46, -39.91) * mm});
            skLineSegment(sketch, "E1959", {"start": v(82.46, -39.91) * mm, "end": v(83.7, -37.26) * mm});
            skLineSegment(sketch, "E1960", {"start": v(83.7, -37.26) * mm, "end": v(84.1, -36.75) * mm});
            skLineSegment(sketch, "E1961", {"start": v(84.1, -36.75) * mm, "end": v(84.4, -36.79) * mm});
            skLineSegment(sketch, "E1962", {"start": v(84.4, -36.79) * mm, "end": v(84.7, -36.83) * mm});
            skLineSegment(sketch, "E1963", {"start": v(84.7, -36.83) * mm, "end": v(85.02, -36.86) * mm});
            skLineSegment(sketch, "E1964", {"start": v(85.02, -36.86) * mm, "end": v(85.34, -36.9) * mm});
            skLineSegment(sketch, "E1965", {"start": v(85.34, -36.9) * mm, "end": v(85.69, -36.92) * mm});
            skLineSegment(sketch, "E1966", {"start": v(85.69, -36.92) * mm, "end": v(86.04, -36.95) * mm});
            skLineSegment(sketch, "E1967", {"start": v(86.04, -36.95) * mm, "end": v(86.4, -36.97) * mm});
            skLineSegment(sketch, "E1968", {"start": v(86.4, -36.97) * mm, "end": v(86.78, -37) * mm});
            skLineSegment(sketch, "E1969", {"start": v(86.78, -37) * mm, "end": v(87.17, -37.01) * mm});
            skLineSegment(sketch, "E1970", {"start": v(87.17, -37.01) * mm, "end": v(87.57, -37.02) * mm});
            skLineSegment(sketch, "E1971", {"start": v(87.57, -37.02) * mm, "end": v(87.98, -37.03) * mm});
            skLineSegment(sketch, "E1972", {"start": v(87.98, -37.03) * mm, "end": v(88.4, -37.03) * mm});
            skLineSegment(sketch, "E1973", {"start": v(88.4, -37.03) * mm, "end": v(88.84, -37.03) * mm});
            skLineSegment(sketch, "E1974", {"start": v(88.84, -37.03) * mm, "end": v(89.29, -37.02) * mm});
            skLineSegment(sketch, "E1975", {"start": v(89.29, -37.02) * mm, "end": v(89.75, -37) * mm});
            skLineSegment(sketch, "E1976", {"start": v(89.75, -37) * mm, "end": v(90.22, -36.99) * mm});
            skLineSegment(sketch, "E1977", {"start": v(90.22, -36.99) * mm, "end": v(90.7, -36.96) * mm});
            skLineSegment(sketch, "E1978", {"start": v(90.7, -36.96) * mm, "end": v(91.2, -36.93) * mm});
            skLineSegment(sketch, "E1979", {"start": v(91.2, -36.93) * mm, "end": v(91.7, -36.9) * mm});
            skLineSegment(sketch, "E1980", {"start": v(91.7, -36.9) * mm, "end": v(92.23, -36.85) * mm});
            skLineSegment(sketch, "E1981", {"start": v(92.23, -36.85) * mm, "end": v(92.76, -36.8) * mm});
            skLineSegment(sketch, "E1982", {"start": v(92.76, -36.8) * mm, "end": v(93.3, -36.73) * mm});
            skLineSegment(sketch, "E1983", {"start": v(93.3, -36.73) * mm, "end": v(93.85, -36.67) * mm});
            skLineSegment(sketch, "E1984", {"start": v(93.85, -36.67) * mm, "end": v(94.42, -36.6) * mm});
            skLineSegment(sketch, "E1985", {"start": v(94.42, -36.6) * mm, "end": v(94.99, -36.5) * mm});
            skLineSegment(sketch, "E1986", {"start": v(94.99, -36.5) * mm, "end": v(95.58, -36.41) * mm});
            skLineSegment(sketch, "E1987", {"start": v(95.58, -36.41) * mm, "end": v(96.17, -36.31) * mm});
            skLineSegment(sketch, "E1988", {"start": v(96.17, -36.31) * mm, "end": v(96.78, -36.2) * mm});
            skLineSegment(sketch, "E1989", {"start": v(96.78, -36.2) * mm, "end": v(97.4, -36.08) * mm});
            skLineSegment(sketch, "E1990", {"start": v(97.4, -36.08) * mm, "end": v(98.02, -35.95) * mm});
            skLineSegment(sketch, "E1991", {"start": v(98.02, -35.95) * mm, "end": v(98.66, -35.81) * mm});
            skLineSegment(sketch, "E1992", {"start": v(98.66, -35.81) * mm, "end": v(99.3, -35.66) * mm});
            skLineSegment(sketch, "E1993", {"start": v(99.3, -35.66) * mm, "end": v(99.73, -35.42) * mm});
            skLineSegment(sketch, "E1994", {"start": v(99.73, -35.42) * mm, "end": v(100.5, -33.18) * mm});
            skLineSegment(sketch, "E1995", {"start": v(100.5, -33.18) * mm, "end": v(100.31, -32.73) * mm});
            skLineSegment(sketch, "E1996", {"start": v(100.31, -32.73) * mm, "end": v(99.89, -32.22) * mm});
            skLineSegment(sketch, "E1997", {"start": v(99.89, -32.22) * mm, "end": v(99.47, -31.72) * mm});
            skLineSegment(sketch, "E1998", {"start": v(99.47, -31.72) * mm, "end": v(99.06, -31.23) * mm});
            skLineSegment(sketch, "E1999", {"start": v(99.06, -31.23) * mm, "end": v(98.64, -30.76) * mm});
            skLineSegment(sketch, "E2000", {"start": v(98.64, -30.76) * mm, "end": v(98.23, -30.3) * mm});
            skLineSegment(sketch, "E2001", {"start": v(98.23, -30.3) * mm, "end": v(97.82, -29.85) * mm});
            skLineSegment(sketch, "E2002", {"start": v(97.82, -29.85) * mm, "end": v(97.42, -29.42) * mm});
            skLineSegment(sketch, "E2003", {"start": v(97.42, -29.42) * mm, "end": v(97.02, -29) * mm});
            skLineSegment(sketch, "E2004", {"start": v(97.02, -29) * mm, "end": v(96.62, -28.6) * mm});
            skLineSegment(sketch, "E2005", {"start": v(96.62, -28.6) * mm, "end": v(96.22, -28.2) * mm});
            skLineSegment(sketch, "E2006", {"start": v(96.22, -28.2) * mm, "end": v(95.83, -27.82) * mm});
            skLineSegment(sketch, "E2007", {"start": v(95.83, -27.82) * mm, "end": v(95.45, -27.46) * mm});
            skLineSegment(sketch, "E2008", {"start": v(95.45, -27.46) * mm, "end": v(95.06, -27.1) * mm});
            skLineSegment(sketch, "E2009", {"start": v(95.06, -27.1) * mm, "end": v(94.69, -26.76) * mm});
            skLineSegment(sketch, "E2010", {"start": v(94.69, -26.76) * mm, "end": v(94.31, -26.43) * mm});
            skLineSegment(sketch, "E2011", {"start": v(94.31, -26.43) * mm, "end": v(93.95, -26.12) * mm});
            skLineSegment(sketch, "E2012", {"start": v(93.95, -26.12) * mm, "end": v(93.59, -25.81) * mm});
            skLineSegment(sketch, "E2013", {"start": v(93.59, -25.81) * mm, "end": v(93.23, -25.52) * mm});
            skLineSegment(sketch, "E2014", {"start": v(93.23, -25.52) * mm, "end": v(92.88, -25.24) * mm});
            skLineSegment(sketch, "E2015", {"start": v(92.88, -25.24) * mm, "end": v(92.54, -24.97) * mm});
            skLineSegment(sketch, "E2016", {"start": v(92.54, -24.97) * mm, "end": v(92.2, -24.7) * mm});
            skLineSegment(sketch, "E2017", {"start": v(92.2, -24.7) * mm, "end": v(91.87, -24.46) * mm});
            skLineSegment(sketch, "E2018", {"start": v(91.87, -24.46) * mm, "end": v(91.55, -24.22) * mm});
            skLineSegment(sketch, "E2019", {"start": v(91.55, -24.22) * mm, "end": v(91.23, -24) * mm});
            skLineSegment(sketch, "E2020", {"start": v(91.23, -24) * mm, "end": v(90.92, -23.78) * mm});
            skLineSegment(sketch, "E2021", {"start": v(90.92, -23.78) * mm, "end": v(90.62, -23.58) * mm});
            skLineSegment(sketch, "E2022", {"start": v(90.62, -23.58) * mm, "end": v(90.32, -23.38) * mm});
            skLineSegment(sketch, "E2023", {"start": v(90.32, -23.38) * mm, "end": v(90.04, -23.2) * mm});
            skLineSegment(sketch, "E2024", {"start": v(90.04, -23.2) * mm, "end": v(89.76, -23.02) * mm});
            skLineSegment(sketch, "E2025", {"start": v(89.76, -23.02) * mm, "end": v(89.49, -22.86) * mm});
            skLineSegment(sketch, "E2026", {"start": v(89.49, -22.86) * mm, "end": v(89.23, -22.7) * mm});
            skLineSegment(sketch, "E2027", {"start": v(89.23, -22.7) * mm, "end": v(88.97, -22.55) * mm});
            skLineSegment(sketch, "E2028", {"start": v(88.97, -22.55) * mm, "end": v(88.96, -21.9) * mm});
            skLineSegment(sketch, "E2029", {"start": v(88.96, -21.9) * mm, "end": v(89.6, -19.05) * mm});
            skLineSegment(sketch, "E2030", {"start": v(89.6, -19.05) * mm, "end": v(89.91, -18.46) * mm});
            skLineSegment(sketch, "E2031", {"start": v(89.91, -18.46) * mm, "end": v(90.2, -18.44) * mm});
            skLineSegment(sketch, "E2032", {"start": v(90.2, -18.44) * mm, "end": v(90.5, -18.41) * mm});
            skLineSegment(sketch, "E2033", {"start": v(90.5, -18.41) * mm, "end": v(90.82, -18.38) * mm});
            skLineSegment(sketch, "E2034", {"start": v(90.82, -18.38) * mm, "end": v(91.15, -18.34) * mm});
            skLineSegment(sketch, "E2035", {"start": v(91.15, -18.34) * mm, "end": v(91.49, -18.3) * mm});
            skLineSegment(sketch, "E2036", {"start": v(91.49, -18.3) * mm, "end": v(91.84, -18.25) * mm});
            skLineSegment(sketch, "E2037", {"start": v(91.84, -18.25) * mm, "end": v(92.2, -18.2) * mm});
            skLineSegment(sketch, "E2038", {"start": v(92.2, -18.2) * mm, "end": v(92.57, -18.14) * mm});
            skLineSegment(sketch, "E2039", {"start": v(92.57, -18.14) * mm, "end": v(92.96, -18.08) * mm});
            skLineSegment(sketch, "E2040", {"start": v(92.96, -18.08) * mm, "end": v(93.35, -18) * mm});
            skLineSegment(sketch, "E2041", {"start": v(93.35, -18) * mm, "end": v(93.76, -17.93) * mm});
            skLineSegment(sketch, "E2042", {"start": v(93.76, -17.93) * mm, "end": v(94.17, -17.84) * mm});
            skLineSegment(sketch, "E2043", {"start": v(94.17, -17.84) * mm, "end": v(94.6, -17.75) * mm});
            skLineSegment(sketch, "E2044", {"start": v(94.6, -17.75) * mm, "end": v(95.04, -17.65) * mm});
            skLineSegment(sketch, "E2045", {"start": v(95.04, -17.65) * mm, "end": v(95.48, -17.54) * mm});
            skLineSegment(sketch, "E2046", {"start": v(95.48, -17.54) * mm, "end": v(95.94, -17.42) * mm});
            skLineSegment(sketch, "E2047", {"start": v(95.94, -17.42) * mm, "end": v(96.41, -17.3) * mm});
            skLineSegment(sketch, "E2048", {"start": v(96.41, -17.3) * mm, "end": v(96.89, -17.16) * mm});
            skLineSegment(sketch, "E2049", {"start": v(96.89, -17.16) * mm, "end": v(97.38, -17.02) * mm});
            skLineSegment(sketch, "E2050", {"start": v(97.38, -17.02) * mm, "end": v(97.87, -16.87) * mm});
            skLineSegment(sketch, "E2051", {"start": v(97.87, -16.87) * mm, "end": v(98.38, -16.7) * mm});
            skLineSegment(sketch, "E2052", {"start": v(98.38, -16.7) * mm, "end": v(98.9, -16.53) * mm});
            skLineSegment(sketch, "E2053", {"start": v(98.9, -16.53) * mm, "end": v(99.43, -16.35) * mm});
            skLineSegment(sketch, "E2054", {"start": v(99.43, -16.35) * mm, "end": v(99.96, -16.16) * mm});
            skLineSegment(sketch, "E2055", {"start": v(99.96, -16.16) * mm, "end": v(100.5, -15.96) * mm});
            skLineSegment(sketch, "E2056", {"start": v(100.5, -15.96) * mm, "end": v(101.06, -15.75) * mm});
            skLineSegment(sketch, "E2057", {"start": v(101.06, -15.75) * mm, "end": v(101.62, -15.52) * mm});
            skLineSegment(sketch, "E2058", {"start": v(101.62, -15.52) * mm, "end": v(102.19, -15.29) * mm});
            skLineSegment(sketch, "E2059", {"start": v(102.19, -15.29) * mm, "end": v(102.77, -15.04) * mm});
            skLineSegment(sketch, "E2060", {"start": v(102.77, -15.04) * mm, "end": v(103.35, -14.79) * mm});
            skLineSegment(sketch, "E2061", {"start": v(103.35, -14.79) * mm, "end": v(103.95, -14.52) * mm});
            skLineSegment(sketch, "E2062", {"start": v(103.95, -14.52) * mm, "end": v(104.55, -14.24) * mm});
            skLineSegment(sketch, "E2063", {"start": v(104.55, -14.24) * mm, "end": v(104.92, -13.91) * mm});
            skLineSegment(sketch, "E2064", {"start": v(104.92, -13.91) * mm, "end": v(105.2, -11.56) * mm});
            skLineSegment(sketch, "E2065", {"start": v(105.2, -11.56) * mm, "end": v(104.92, -11.16) * mm});
            skLineSegment(sketch, "E2066", {"start": v(104.92, -11.16) * mm, "end": v(104.4, -10.75) * mm});
            skLineSegment(sketch, "E2067", {"start": v(104.4, -10.75) * mm, "end": v(103.9, -10.34) * mm});
            skLineSegment(sketch, "E2068", {"start": v(103.9, -10.34) * mm, "end": v(103.38, -9.95) * mm});
            skLineSegment(sketch, "E2069", {"start": v(103.38, -9.95) * mm, "end": v(102.88, -9.58) * mm});
            skLineSegment(sketch, "E2070", {"start": v(102.88, -9.58) * mm, "end": v(102.38, -9.21) * mm});
            skLineSegment(sketch, "E2071", {"start": v(102.38, -9.21) * mm, "end": v(101.9, -8.86) * mm});
            skLineSegment(sketch, "E2072", {"start": v(101.9, -8.86) * mm, "end": v(101.4, -8.52) * mm});
            skLineSegment(sketch, "E2073", {"start": v(101.4, -8.52) * mm, "end": v(100.93, -8.2) * mm});
            skLineSegment(sketch, "E2074", {"start": v(100.93, -8.2) * mm, "end": v(100.45, -7.88) * mm});
            skLineSegment(sketch, "E2075", {"start": v(100.45, -7.88) * mm, "end": v(99.98, -7.58) * mm});
            skLineSegment(sketch, "E2076", {"start": v(99.98, -7.58) * mm, "end": v(99.52, -7.3) * mm});
            skLineSegment(sketch, "E2077", {"start": v(99.52, -7.3) * mm, "end": v(99.07, -7.01) * mm});
            skLineSegment(sketch, "E2078", {"start": v(99.07, -7.01) * mm, "end": v(98.62, -6.75) * mm});
            skLineSegment(sketch, "E2079", {"start": v(98.62, -6.75) * mm, "end": v(98.18, -6.5) * mm});
            skLineSegment(sketch, "E2080", {"start": v(98.18, -6.5) * mm, "end": v(97.75, -6.25) * mm});
            skLineSegment(sketch, "E2081", {"start": v(97.75, -6.25) * mm, "end": v(97.33, -6.01) * mm});
            skLineSegment(sketch, "E2082", {"start": v(97.33, -6.01) * mm, "end": v(96.9, -5.79) * mm});
            skLineSegment(sketch, "E2083", {"start": v(96.9, -5.79) * mm, "end": v(96.5, -5.58) * mm});
            skLineSegment(sketch, "E2084", {"start": v(96.5, -5.58) * mm, "end": v(96.1, -5.37) * mm});
            skLineSegment(sketch, "E2085", {"start": v(96.1, -5.37) * mm, "end": v(95.7, -5.18) * mm});
            skLineSegment(sketch, "E2086", {"start": v(95.7, -5.18) * mm, "end": v(95.32, -5) * mm});
            skLineSegment(sketch, "E2087", {"start": v(95.32, -5) * mm, "end": v(94.95, -4.83) * mm});
            skLineSegment(sketch, "E2088", {"start": v(94.95, -4.83) * mm, "end": v(94.58, -4.66) * mm});
            skLineSegment(sketch, "E2089", {"start": v(94.58, -4.66) * mm, "end": v(94.23, -4.5) * mm});
            skLineSegment(sketch, "E2090", {"start": v(94.23, -4.5) * mm, "end": v(93.88, -4.36) * mm});
            skLineSegment(sketch, "E2091", {"start": v(93.88, -4.36) * mm, "end": v(93.54, -4.22) * mm});
            skLineSegment(sketch, "E2092", {"start": v(93.54, -4.22) * mm, "end": v(93.21, -4.1) * mm});
            skLineSegment(sketch, "E2093", {"start": v(93.21, -4.1) * mm, "end": v(92.9, -3.97) * mm});
            skLineSegment(sketch, "E2094", {"start": v(92.9, -3.97) * mm, "end": v(92.58, -3.86) * mm});
            skLineSegment(sketch, "E2095", {"start": v(92.58, -3.86) * mm, "end": v(92.29, -3.75) * mm});
            skLineSegment(sketch, "E2096", {"start": v(92.29, -3.75) * mm, "end": v(92, -3.65) * mm});
            skLineSegment(sketch, "E2097", {"start": v(92, -3.65) * mm, "end": v(91.72, -3.56) * mm});
            skLineSegment(sketch, "E2098", {"start": v(91.72, -3.56) * mm, "end": v(91.57, -2.92) * mm});
            skLineSegment(sketch, "E2099", {"start": v(91.57, -2.92) * mm, "end": v(91.61, 0) * mm});
            skCircle(sketch, "E2100", {"center": v(0, 0) * mm, "radius": 3.84 * mm});
            skSolve(sketch);
        }
        {
            var Q0;
            Q0 = qSketchRegion(id + "F0", true);
            extrude(context, id + "F1", {"entities" : qUnion([Q0]), "oppositeDirection" : true, "depth" : 25.4 * mm, "offsetDistance" : 25.4 * mm});
        }
    });
